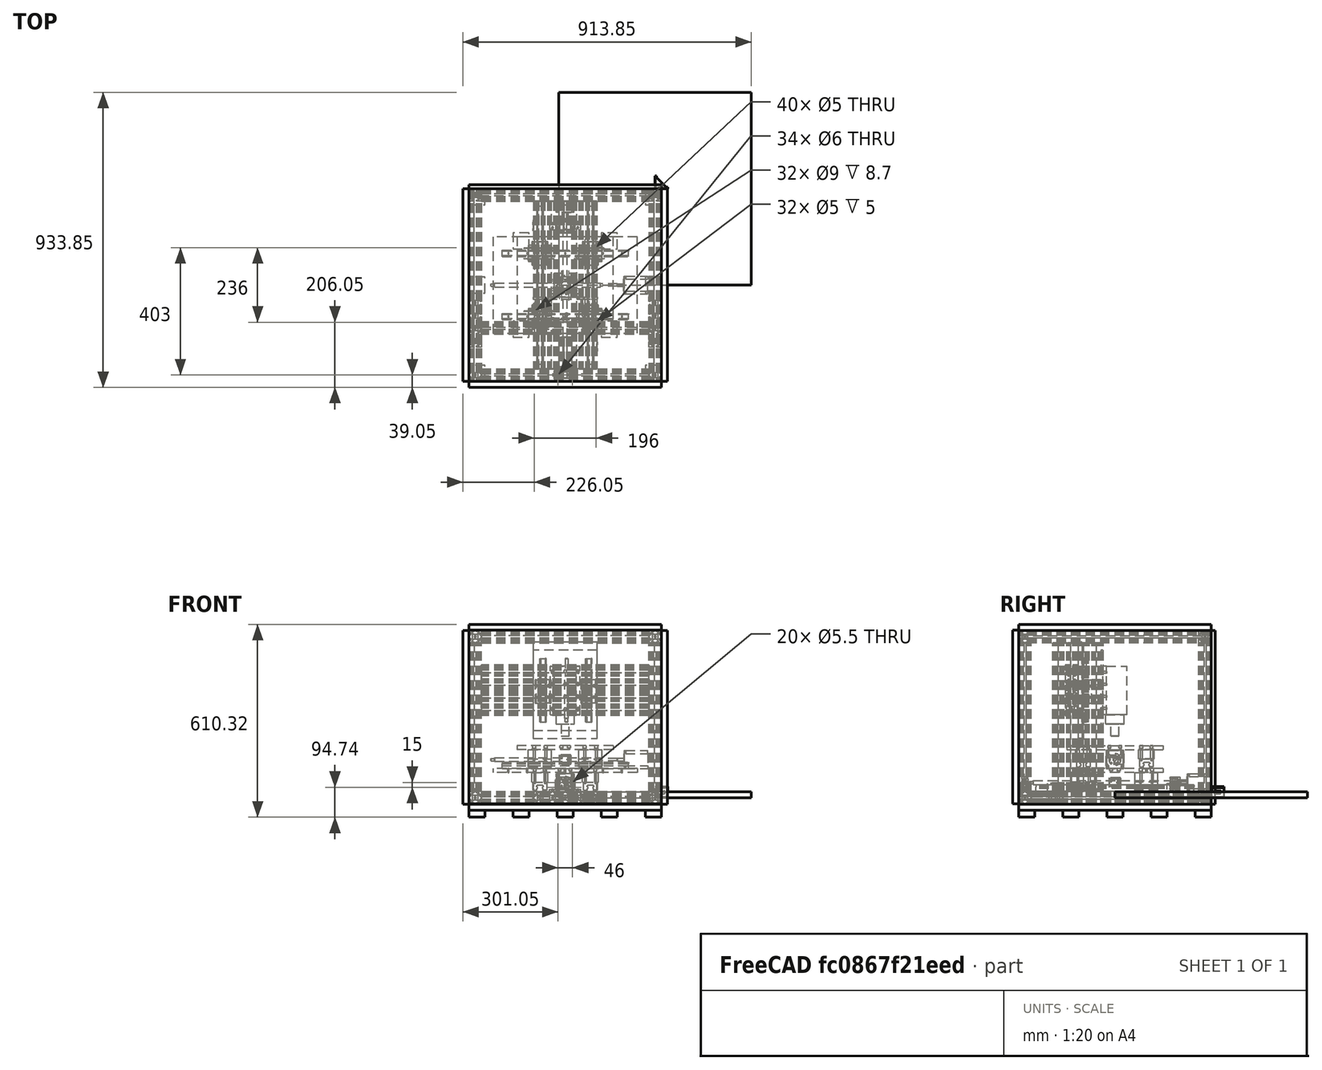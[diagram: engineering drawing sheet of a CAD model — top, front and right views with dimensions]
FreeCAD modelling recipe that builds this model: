
FCSTD DOCUMENT  (FreeCAD 1.0R39109 (Git))
Label: cnc
License: All rights reserved
LicenseURL: http://en.wikipedia.org/wiki/All_rights_reserved
objects: PartDesign::Body×118, PartDesign::FeatureBase×86, Sketcher::SketchObject×41, PartDesign::Pad×35, TechDraw::DrawViewDimension×35, PartDesign::Pocket×10, TechDraw::DrawViewBalloon×9, TechDraw::DrawProjGroupItem×8, App::DocumentObjectGroup×7, TechDraw::DrawViewAnnotation×5, Part::Extrusion×4, Part::Cut×4, TechDraw::DrawSVGTemplate×4, TechDraw::DrawPage×4, PartDesign::Revolution×3, Part::Box×1, Spreadsheet::Sheet×1, TechDraw::DrawProjGroup×1
note: 586 computed .brp shape members not serialized (recipe doc carries the construction recipe); baked Part::Feature solids carry a one-line shape summary decoded from their .brp

FEATURE [Sketcher::SketchObject] Sketch001
  ArcFitTolerance = 1e-06
  AttachmentSupport = -> [XY_Plane001]
  FullyConstrained = true
  MakeInternals = false
  MapMode = 5
  sketch-geometry (37):
    g0: LineSegment StartX=-20 StartY=4.065 StartZ=0 EndX=-20 EndY=20 EndZ=0
    g1: LineSegment StartX=-20 StartY=20 StartZ=0 EndX=-4.065 EndY=20 EndZ=0
    g2: LineSegment StartX=-4.065 StartY=20 StartZ=0 EndX=-4.065 EndY=15.68 EndZ=0
    g3: LineSegment StartX=-4.065 StartY=15.68 StartZ=0 EndX=-12.6253 EndY=15.68 EndZ=0
    g4: LineSegment StartX=-12.6253 StartY=15.68 StartZ=0 EndX=-5.22957 EndY=8.28427 EndZ=0
    g5: LineSegment StartX=-5.22957 StartY=8.28427 StartZ=0 EndX=5.22957 EndY=8.28427 EndZ=0
    g6: LineSegment StartX=5.22957 StartY=8.28427 StartZ=0 EndX=12.6253 EndY=15.68 EndZ=0
    g7: LineSegment StartX=12.6253 StartY=15.68 StartZ=0 EndX=4.065 EndY=15.68 EndZ=0
    g8: LineSegment StartX=4.065 StartY=15.68 StartZ=0 EndX=4.065 EndY=20 EndZ=0
    g9: LineSegment StartX=4.065 StartY=20 StartZ=0 EndX=20 EndY=20 EndZ=0
    g10: LineSegment StartX=20 StartY=20 StartZ=0 EndX=20 EndY=4.065 EndZ=0
    g11: LineSegment StartX=20 StartY=4.065 StartZ=0 EndX=15.68 EndY=4.065 EndZ=0
    g12: LineSegment StartX=15.68 StartY=4.065 StartZ=0 EndX=15.68 EndY=12.6253 EndZ=0
    g13: LineSegment StartX=15.68 StartY=12.6253 StartZ=0 EndX=8.28427 EndY=5.22957 EndZ=0
    g14: LineSegment StartX=8.28427 StartY=5.22957 StartZ=0 EndX=8.28427 EndY=-5.22957 EndZ=0
    g15: LineSegment StartX=8.28427 StartY=-5.22957 StartZ=0 EndX=15.68 EndY=-12.6253 EndZ=0
    g16: LineSegment StartX=15.68 StartY=-12.6253 StartZ=0 EndX=15.68 EndY=-4.065 EndZ=0
    g17: LineSegment StartX=15.68 StartY=-4.065 StartZ=0 EndX=20 EndY=-4.065 EndZ=0
    g18: LineSegment StartX=20 StartY=-4.065 StartZ=0 EndX=20 EndY=-20 EndZ=0
    g19: LineSegment StartX=20 StartY=-20 StartZ=0 EndX=4.065 EndY=-20 EndZ=0
    g20: LineSegment StartX=4.065 StartY=-20 StartZ=0 EndX=4.065 EndY=-15.68 EndZ=0
    g21: LineSegment StartX=4.065 StartY=-15.68 StartZ=0 EndX=12.6253 EndY=-15.68 EndZ=0
    g22: LineSegment StartX=12.6253 StartY=-15.68 StartZ=0 EndX=5.22957 EndY=-8.28427 EndZ=0
    g23: LineSegment StartX=5.22957 StartY=-8.28427 StartZ=0 EndX=-5.22957 EndY=-8.28427 EndZ=0
    g24: LineSegment StartX=-5.22957 StartY=-8.28427 StartZ=0 EndX=-12.6253 EndY=-15.68 EndZ=0
    g25: LineSegment StartX=-12.6253 StartY=-15.68 StartZ=0 EndX=-4.065 EndY=-15.68 EndZ=0
    g26: LineSegment StartX=-4.065 StartY=-15.68 StartZ=0 EndX=-4.065 EndY=-20 EndZ=0
    g27: LineSegment StartX=-4.065 StartY=-20 StartZ=0 EndX=-20 EndY=-20 EndZ=0
    g28: LineSegment StartX=-20 StartY=-20 StartZ=0 EndX=-20 EndY=-4.065 EndZ=0
    g29: LineSegment StartX=-20 StartY=-4.065 StartZ=0 EndX=-15.68 EndY=-4.065 EndZ=0
    g30: LineSegment StartX=-15.68 StartY=-4.065 StartZ=0 EndX=-15.68 EndY=-12.6253 EndZ=0
    g31: LineSegment StartX=-15.68 StartY=-12.6253 StartZ=0 EndX=-8.28427 EndY=-5.22957 EndZ=0
    g32: LineSegment StartX=-8.28427 StartY=-5.22957 StartZ=0 EndX=-8.28427 EndY=5.22957 EndZ=0
    g33: LineSegment StartX=-8.28427 StartY=5.22957 StartZ=0 EndX=-15.68 EndY=12.6253 EndZ=0
    g34: LineSegment StartX=-15.68 StartY=12.6253 StartZ=0 EndX=-15.68 EndY=4.065 EndZ=0
    g35: LineSegment StartX=-15.68 StartY=4.065 StartZ=0 EndX=-20 EndY=4.065 EndZ=0
    g36: Circle CenterX=0 CenterY=0 CenterZ=0 NormalX=0 NormalY=0 NormalZ=1 AngleXU=0 Radius=3.405
  constraints (100):
    c: Coincident(g24,g23)
    c: Coincident(g32,g31)
    c: Coincident(g30,g31)
    c: Coincident(g25,g24)
    c: Coincident(g25,g26)
    c: Coincident(g20,g21)
    c: Coincident(g19,g20)
    c: Coincident(g26,g27)
    c: Coincident(g28,g27)
    c: Coincident(g21,g22)
    c: Coincident(g19,g18)
    c: Coincident(g16,g15)
    c: Coincident(g14,g15)
    c: Coincident(g23,g22)
    c: Coincident(g16,g17)
    c: Coincident(g18,g17)
    c: Coincident(g12,g11)
    c: Coincident(g11,g10)
    c: Coincident(g10,g9)
    c: Coincident(g13,g12)
    c: Coincident(g13,g14)
    c: Coincident(g6,g5)
    c: Coincident(g7,g6)
    c: Coincident(g8,g7)
    c: Coincident(g9,g8)
    c: Coincident(g2,g1)
    c: Coincident(g2,g3)
    c: Coincident(g4,g3)
    c: Coincident(g34,g33)
    c: Coincident(g5,g4)
    c: Coincident(g33,g32)
    c: Coincident(g35,g34)
    c: Coincident(g35,g0)
    c: Coincident(g1,g0)
    c: Coincident(g30,g29)
    c: Coincident(g29,g28)
    c: Distance(g10,g0) = 40
    c: Distance(g27,g1) = 40
    c: Tangent(g1,g9)
    c: Tangent(g27,g19)
    c: Tangent(g0,g28)
    c: Tangent(g10,g18)
    c: Horizontal(g1)
    c: Vertical(g0)
    c: Equal(g2,g8)
    c: Equal(g8,g35)
    c: Equal(g35,g29)
    c: Equal(g29,g26)
    c: Equal(g26,g20)
    c: Equal(g20,g17)
    c: Equal(g17,g11)
    c: Vertical(g34)
    c: Vertical(g30)
    c: Vertical(g16)
    c: Vertical(g18)
    c: Vertical(g12)
    c: Vertical(g8)
    c: Vertical(g2)
    c: Vertical(g14)
    c: Vertical(g32)
    c: Horizontal(g35)
    c: Horizontal(g29)
    c: Horizontal(g23)
    c: Horizontal(g19)
    c: Horizontal(g25)
    c: Horizontal(g21)
    c: Horizontal(g7)
    c: Horizontal(g3)
    c: Parallel(g4,g33)
    c: Parallel(g33,g15)
    c: Parallel(g15,g22)
    c: Parallel(g6,g13)
    c: Parallel(g13,g24)
    c: Parallel(g24,g31)
    c: Equal(g23,g24)
    c: Equal(g24,g31)
    c: Equal(g4,g33)
    c: Equal(g6,g13)
    c: Equal(g15,g22)
    c: Angle(g25,g24) = 0.785398
    c: Distance(g8,g2) = 8.13
    c: Distance(g29,g35) = 8.13
    c: Tangent(g35,g11)
    c: Tangent(g17,g29)
    c: Tangent(g2,g26)
    c: Tangent(g8,g20)
    c: Distance(g22,g15) = 4.32
    c: Distance(g13,g6) = 4.32
    c: Distance(g33,g4) = 4.32
    c: Distance(g24,g31) = 4.32
    c: Equal(g32,g14)
    c: Equal(g5,g23)
    c: Equal(g25,g21)
    c: Equal(g34,g30)
    c: Distance(g35,g35) = 4.32
    c: Symmetric(g5,g22,g-1)
    c: Symmetric(g4,g5,g-2)
    c: Equal(g5,g32)
    c: Coincident(g36,g-1)
    c: Diameter(g36) = 6.81
FEATURE [Sketcher::SketchObject] Sketch002
  ArcFitTolerance = 1e-06
  AttachmentSupport = -> [XY_Plane003]
  FullyConstrained = true
  MakeInternals = false
  MapMode = 5
  sketch-geometry (37):
    g0: LineSegment StartX=-20 StartY=4.065 StartZ=0 EndX=-20 EndY=20 EndZ=0
    g1: LineSegment StartX=-20 StartY=20 StartZ=0 EndX=-4.065 EndY=20 EndZ=0
    g2: LineSegment StartX=-4.065 StartY=20 StartZ=0 EndX=-4.065 EndY=15.68 EndZ=0
    g3: LineSegment StartX=-4.065 StartY=15.68 StartZ=0 EndX=-12.6253 EndY=15.68 EndZ=0
    g4: LineSegment StartX=-12.6253 StartY=15.68 StartZ=0 EndX=-5.22957 EndY=8.28427 EndZ=0
    g5: LineSegment StartX=-5.22957 StartY=8.28427 StartZ=0 EndX=5.22957 EndY=8.28427 EndZ=0
    g6: LineSegment StartX=5.22957 StartY=8.28427 StartZ=0 EndX=12.6253 EndY=15.68 EndZ=0
    g7: LineSegment StartX=12.6253 StartY=15.68 StartZ=0 EndX=4.065 EndY=15.68 EndZ=0
    g8: LineSegment StartX=4.065 StartY=15.68 StartZ=0 EndX=4.065 EndY=20 EndZ=0
    g9: LineSegment StartX=4.065 StartY=20 StartZ=0 EndX=20 EndY=20 EndZ=0
    g10: LineSegment StartX=20 StartY=20 StartZ=0 EndX=20 EndY=4.065 EndZ=0
    g11: LineSegment StartX=20 StartY=4.065 StartZ=0 EndX=15.68 EndY=4.065 EndZ=0
    g12: LineSegment StartX=15.68 StartY=4.065 StartZ=0 EndX=15.68 EndY=12.6253 EndZ=0
    g13: LineSegment StartX=15.68 StartY=12.6253 StartZ=0 EndX=8.28427 EndY=5.22957 EndZ=0
    g14: LineSegment StartX=8.28427 StartY=5.22957 StartZ=0 EndX=8.28427 EndY=-5.22957 EndZ=0
    g15: LineSegment StartX=8.28427 StartY=-5.22957 StartZ=0 EndX=15.68 EndY=-12.6253 EndZ=0
    g16: LineSegment StartX=15.68 StartY=-12.6253 StartZ=0 EndX=15.68 EndY=-4.065 EndZ=0
    g17: LineSegment StartX=15.68 StartY=-4.065 StartZ=0 EndX=20 EndY=-4.065 EndZ=0
    g18: LineSegment StartX=20 StartY=-4.065 StartZ=0 EndX=20 EndY=-20 EndZ=0
    g19: LineSegment StartX=20 StartY=-20 StartZ=0 EndX=4.065 EndY=-20 EndZ=0
    g20: LineSegment StartX=4.065 StartY=-20 StartZ=0 EndX=4.065 EndY=-15.68 EndZ=0
    g21: LineSegment StartX=4.065 StartY=-15.68 StartZ=0 EndX=12.6253 EndY=-15.68 EndZ=0
    g22: LineSegment StartX=12.6253 StartY=-15.68 StartZ=0 EndX=5.22957 EndY=-8.28427 EndZ=0
    g23: LineSegment StartX=5.22957 StartY=-8.28427 StartZ=0 EndX=-5.22957 EndY=-8.28427 EndZ=0
    g24: LineSegment StartX=-5.22957 StartY=-8.28427 StartZ=0 EndX=-12.6253 EndY=-15.68 EndZ=0
    g25: LineSegment StartX=-12.6253 StartY=-15.68 StartZ=0 EndX=-4.065 EndY=-15.68 EndZ=0
    g26: LineSegment StartX=-4.065 StartY=-15.68 StartZ=0 EndX=-4.065 EndY=-20 EndZ=0
    g27: LineSegment StartX=-4.065 StartY=-20 StartZ=0 EndX=-20 EndY=-20 EndZ=0
    g28: LineSegment StartX=-20 StartY=-20 StartZ=0 EndX=-20 EndY=-4.065 EndZ=0
    g29: LineSegment StartX=-20 StartY=-4.065 StartZ=0 EndX=-15.68 EndY=-4.065 EndZ=0
    g30: LineSegment StartX=-15.68 StartY=-4.065 StartZ=0 EndX=-15.68 EndY=-12.6253 EndZ=0
    g31: LineSegment StartX=-15.68 StartY=-12.6253 StartZ=0 EndX=-8.28427 EndY=-5.22957 EndZ=0
    g32: LineSegment StartX=-8.28427 StartY=-5.22957 StartZ=0 EndX=-8.28427 EndY=5.22957 EndZ=0
    g33: LineSegment StartX=-8.28427 StartY=5.22957 StartZ=0 EndX=-15.68 EndY=12.6253 EndZ=0
    g34: LineSegment StartX=-15.68 StartY=12.6253 StartZ=0 EndX=-15.68 EndY=4.065 EndZ=0
    g35: LineSegment StartX=-15.68 StartY=4.065 StartZ=0 EndX=-20 EndY=4.065 EndZ=0
    g36: Circle CenterX=0 CenterY=0 CenterZ=0 NormalX=0 NormalY=0 NormalZ=1 AngleXU=0 Radius=3.405
  constraints (100):
    c: Coincident(g24,g23)
    c: Coincident(g32,g31)
    c: Coincident(g30,g31)
    c: Coincident(g25,g24)
    c: Coincident(g25,g26)
    c: Coincident(g20,g21)
    c: Coincident(g19,g20)
    c: Coincident(g26,g27)
    c: Coincident(g28,g27)
    c: Coincident(g21,g22)
    c: Coincident(g19,g18)
    c: Coincident(g16,g15)
    c: Coincident(g14,g15)
    c: Coincident(g23,g22)
    c: Coincident(g16,g17)
    c: Coincident(g18,g17)
    c: Coincident(g12,g11)
    c: Coincident(g11,g10)
    c: Coincident(g10,g9)
    c: Coincident(g13,g12)
    c: Coincident(g13,g14)
    c: Coincident(g6,g5)
    c: Coincident(g7,g6)
    c: Coincident(g8,g7)
    c: Coincident(g9,g8)
    c: Coincident(g2,g1)
    c: Coincident(g2,g3)
    c: Coincident(g4,g3)
    c: Coincident(g34,g33)
    c: Coincident(g5,g4)
    c: Coincident(g33,g32)
    c: Coincident(g35,g34)
    c: Coincident(g35,g0)
    c: Coincident(g1,g0)
    c: Coincident(g30,g29)
    c: Coincident(g29,g28)
    c: Distance(g10,g0) = 40
    c: Distance(g27,g1) = 40
    c: Tangent(g1,g9)
    c: Tangent(g27,g19)
    c: Tangent(g0,g28)
    c: Tangent(g10,g18)
    c: Horizontal(g1)
    c: Vertical(g0)
    c: Equal(g2,g8)
    c: Equal(g8,g35)
    c: Equal(g35,g29)
    c: Equal(g29,g26)
    c: Equal(g26,g20)
    c: Equal(g20,g17)
    c: Equal(g17,g11)
    c: Vertical(g34)
    c: Vertical(g30)
    c: Vertical(g16)
    c: Vertical(g18)
    c: Vertical(g12)
    c: Vertical(g8)
    c: Vertical(g2)
    c: Vertical(g14)
    c: Vertical(g32)
    c: Horizontal(g35)
    c: Horizontal(g29)
    c: Horizontal(g23)
    c: Horizontal(g19)
    c: Horizontal(g25)
    c: Horizontal(g21)
    c: Horizontal(g7)
    c: Horizontal(g3)
    c: Parallel(g4,g33)
    c: Parallel(g33,g15)
    c: Parallel(g15,g22)
    c: Parallel(g6,g13)
    c: Parallel(g13,g24)
    c: Parallel(g24,g31)
    c: Equal(g23,g24)
    c: Equal(g24,g31)
    c: Equal(g4,g33)
    c: Equal(g6,g13)
    c: Equal(g15,g22)
    c: Angle(g25,g24) = 0.785398
    c: Distance(g8,g2) = 8.13
    c: Distance(g29,g35) = 8.13
    c: Tangent(g35,g11)
    c: Tangent(g17,g29)
    c: Tangent(g2,g26)
    c: Tangent(g8,g20)
    c: Distance(g22,g15) = 4.32
    c: Distance(g13,g6) = 4.32
    c: Distance(g33,g4) = 4.32
    c: Distance(g24,g31) = 4.32
    c: Equal(g32,g14)
    c: Equal(g5,g23)
    c: Equal(g25,g21)
    c: Equal(g34,g30)
    c: Distance(g35,g35) = 4.32
    c: Symmetric(g5,g22,g-1)
    c: Symmetric(g4,g5,g-2)
    c: Equal(g5,g32)
    c: Coincident(g36,g-1)
    c: Diameter(g36) = 6.81
FEATURE [PartDesign::Pad] Pad
  Direction = (0,0,1)
  Length = 610
  Length2 = 10
  Profile = -> Sketch001
  ReferenceAxis = -> Sketch001 [N_Axis]
  Refine = true
  Suppressed = false
  Type = 0
FEATURE [PartDesign::Body] Body001  label="4040 extrusion @ 610"
  AllowCompound = false
  Group = -> [Sketch001,Pad]
  Origin = -> Origin001
  Tip = -> Pad
FEATURE [PartDesign::Pad] Pad001
  Direction = (0,0,1)
  Length = 530
  Length2 = 10
  Profile = -> Sketch002
  ReferenceAxis = -> Sketch002 [N_Axis]
  Refine = true
  Suppressed = false
  Type = 0
FEATURE [PartDesign::Body] Body002  label="4040 extrusion @ 530"
  AllowCompound = false
  Group = -> [Sketch002,Pad001]
  Origin = -> Origin003
  Tip = -> Pad001
FEATURE [Sketcher::SketchObject] Sketch003
  ArcFitTolerance = 1e-06
  AttachmentSupport = -> [XY_Plane005]
  FullyConstrained = true
  MakeInternals = false
  MapMode = 5
  sketch-geometry (37):
    g0: LineSegment StartX=-20 StartY=4.065 StartZ=0 EndX=-20 EndY=20 EndZ=0
    g1: LineSegment StartX=-20 StartY=20 StartZ=0 EndX=-4.065 EndY=20 EndZ=0
    g2: LineSegment StartX=-4.065 StartY=20 StartZ=0 EndX=-4.065 EndY=15.68 EndZ=0
    g3: LineSegment StartX=-4.065 StartY=15.68 StartZ=0 EndX=-12.6253 EndY=15.68 EndZ=0
    g4: LineSegment StartX=-12.6253 StartY=15.68 StartZ=0 EndX=-5.22957 EndY=8.28427 EndZ=0
    g5: LineSegment StartX=-5.22957 StartY=8.28427 StartZ=0 EndX=5.22957 EndY=8.28427 EndZ=0
    g6: LineSegment StartX=5.22957 StartY=8.28427 StartZ=0 EndX=12.6253 EndY=15.68 EndZ=0
    g7: LineSegment StartX=12.6253 StartY=15.68 StartZ=0 EndX=4.065 EndY=15.68 EndZ=0
    g8: LineSegment StartX=4.065 StartY=15.68 StartZ=0 EndX=4.065 EndY=20 EndZ=0
    g9: LineSegment StartX=4.065 StartY=20 StartZ=0 EndX=20 EndY=20 EndZ=0
    g10: LineSegment StartX=20 StartY=20 StartZ=0 EndX=20 EndY=4.065 EndZ=0
    g11: LineSegment StartX=20 StartY=4.065 StartZ=0 EndX=15.68 EndY=4.065 EndZ=0
    g12: LineSegment StartX=15.68 StartY=4.065 StartZ=0 EndX=15.68 EndY=12.6253 EndZ=0
    g13: LineSegment StartX=15.68 StartY=12.6253 StartZ=0 EndX=8.28427 EndY=5.22957 EndZ=0
    g14: LineSegment StartX=8.28427 StartY=5.22957 StartZ=0 EndX=8.28427 EndY=-5.22957 EndZ=0
    g15: LineSegment StartX=8.28427 StartY=-5.22957 StartZ=0 EndX=15.68 EndY=-12.6253 EndZ=0
    g16: LineSegment StartX=15.68 StartY=-12.6253 StartZ=0 EndX=15.68 EndY=-4.065 EndZ=0
    g17: LineSegment StartX=15.68 StartY=-4.065 StartZ=0 EndX=20 EndY=-4.065 EndZ=0
    g18: LineSegment StartX=20 StartY=-4.065 StartZ=0 EndX=20 EndY=-20 EndZ=0
    g19: LineSegment StartX=20 StartY=-20 StartZ=0 EndX=4.065 EndY=-20 EndZ=0
    g20: LineSegment StartX=4.065 StartY=-20 StartZ=0 EndX=4.065 EndY=-15.68 EndZ=0
    g21: LineSegment StartX=4.065 StartY=-15.68 StartZ=0 EndX=12.6253 EndY=-15.68 EndZ=0
    g22: LineSegment StartX=12.6253 StartY=-15.68 StartZ=0 EndX=5.22957 EndY=-8.28427 EndZ=0
    g23: LineSegment StartX=5.22957 StartY=-8.28427 StartZ=0 EndX=-5.22957 EndY=-8.28427 EndZ=0
    g24: LineSegment StartX=-5.22957 StartY=-8.28427 StartZ=0 EndX=-12.6253 EndY=-15.68 EndZ=0
    g25: LineSegment StartX=-12.6253 StartY=-15.68 StartZ=0 EndX=-4.065 EndY=-15.68 EndZ=0
    g26: LineSegment StartX=-4.065 StartY=-15.68 StartZ=0 EndX=-4.065 EndY=-20 EndZ=0
    g27: LineSegment StartX=-4.065 StartY=-20 StartZ=0 EndX=-20 EndY=-20 EndZ=0
    g28: LineSegment StartX=-20 StartY=-20 StartZ=0 EndX=-20 EndY=-4.065 EndZ=0
    g29: LineSegment StartX=-20 StartY=-4.065 StartZ=0 EndX=-15.68 EndY=-4.065 EndZ=0
    g30: LineSegment StartX=-15.68 StartY=-4.065 StartZ=0 EndX=-15.68 EndY=-12.6253 EndZ=0
    g31: LineSegment StartX=-15.68 StartY=-12.6253 StartZ=0 EndX=-8.28427 EndY=-5.22957 EndZ=0
    g32: LineSegment StartX=-8.28427 StartY=-5.22957 StartZ=0 EndX=-8.28427 EndY=5.22957 EndZ=0
    g33: LineSegment StartX=-8.28427 StartY=5.22957 StartZ=0 EndX=-15.68 EndY=12.6253 EndZ=0
    g34: LineSegment StartX=-15.68 StartY=12.6253 StartZ=0 EndX=-15.68 EndY=4.065 EndZ=0
    g35: LineSegment StartX=-15.68 StartY=4.065 StartZ=0 EndX=-20 EndY=4.065 EndZ=0
    g36: Circle CenterX=0 CenterY=0 CenterZ=0 NormalX=0 NormalY=0 NormalZ=1 AngleXU=0 Radius=3.405
  constraints (100):
    c: Coincident(g24,g23)
    c: Coincident(g32,g31)
    c: Coincident(g30,g31)
    c: Coincident(g25,g24)
    c: Coincident(g25,g26)
    c: Coincident(g20,g21)
    c: Coincident(g19,g20)
    c: Coincident(g26,g27)
    c: Coincident(g28,g27)
    c: Coincident(g21,g22)
    c: Coincident(g19,g18)
    c: Coincident(g16,g15)
    c: Coincident(g14,g15)
    c: Coincident(g23,g22)
    c: Coincident(g16,g17)
    c: Coincident(g18,g17)
    c: Coincident(g12,g11)
    c: Coincident(g11,g10)
    c: Coincident(g10,g9)
    c: Coincident(g13,g12)
    c: Coincident(g13,g14)
    c: Coincident(g6,g5)
    c: Coincident(g7,g6)
    c: Coincident(g8,g7)
    c: Coincident(g9,g8)
    c: Coincident(g2,g1)
    c: Coincident(g2,g3)
    c: Coincident(g4,g3)
    c: Coincident(g34,g33)
    c: Coincident(g5,g4)
    c: Coincident(g33,g32)
    c: Coincident(g35,g34)
    c: Coincident(g35,g0)
    c: Coincident(g1,g0)
    c: Coincident(g30,g29)
    c: Coincident(g29,g28)
    c: Distance(g10,g0) = 40
    c: Distance(g27,g1) = 40
    c: Tangent(g1,g9)
    c: Tangent(g27,g19)
    c: Tangent(g0,g28)
    c: Tangent(g10,g18)
    c: Horizontal(g1)
    c: Vertical(g0)
    c: Equal(g2,g8)
    c: Equal(g8,g35)
    c: Equal(g35,g29)
    c: Equal(g29,g26)
    c: Equal(g26,g20)
    c: Equal(g20,g17)
    c: Equal(g17,g11)
    c: Vertical(g34)
    c: Vertical(g30)
    c: Vertical(g16)
    c: Vertical(g18)
    c: Vertical(g12)
    c: Vertical(g8)
    c: Vertical(g2)
    c: Vertical(g14)
    c: Vertical(g32)
    c: Horizontal(g35)
    c: Horizontal(g29)
    c: Horizontal(g23)
    c: Horizontal(g19)
    c: Horizontal(g25)
    c: Horizontal(g21)
    c: Horizontal(g7)
    c: Horizontal(g3)
    c: Parallel(g4,g33)
    c: Parallel(g33,g15)
    c: Parallel(g15,g22)
    c: Parallel(g6,g13)
    c: Parallel(g13,g24)
    c: Parallel(g24,g31)
    c: Equal(g23,g24)
    c: Equal(g24,g31)
    c: Equal(g4,g33)
    c: Equal(g6,g13)
    c: Equal(g15,g22)
    c: Angle(g25,g24) = 0.785398
    c: Distance(g8,g2) = 8.13
    c: Distance(g29,g35) = 8.13
    c: Tangent(g35,g11)
    c: Tangent(g17,g29)
    c: Tangent(g2,g26)
    c: Tangent(g8,g20)
    c: Distance(g22,g15) = 4.32
    c: Distance(g13,g6) = 4.32
    c: Distance(g33,g4) = 4.32
    c: Distance(g24,g31) = 4.32
    c: Equal(g32,g14)
    c: Equal(g5,g23)
    c: Equal(g25,g21)
    c: Equal(g34,g30)
    c: Distance(g35,g35) = 4.32
    c: Symmetric(g5,g22,g-1)
    c: Symmetric(g4,g5,g-2)
    c: Equal(g5,g32)
    c: Coincident(g36,g-1)
    c: Diameter(g36) = 6.81
FEATURE [PartDesign::Pad] Pad002
  Direction = (0,0,1)
  Length = 470
  Length2 = 10
  Profile = -> Sketch003
  ReferenceAxis = -> Sketch003 [N_Axis]
  Refine = true
  Suppressed = false
  Type = 0
FEATURE [PartDesign::Body] Body003  label="4040 extrusion @ 470"
  AllowCompound = false
  Group = -> [Sketch003,Pad002]
  Origin = -> Origin005
  Tip = -> Pad002
FEATURE [Sketcher::SketchObject] Sketch004
  ArcFitTolerance = 1e-06
  AttachmentSupport = -> [XY_Plane006]
  FullyConstrained = true
  MakeInternals = false
  MapMode = 5
  sketch-geometry (70):
    g0: LineSegment StartX=-20 StartY=4.065 StartZ=0 EndX=-20 EndY=20 EndZ=0
    g1: LineSegment StartX=-20 StartY=20 StartZ=0 EndX=-4.065 EndY=20 EndZ=0
    g2: LineSegment StartX=-4.065 StartY=20 StartZ=0 EndX=-4.065 EndY=15.68 EndZ=0
    g3: LineSegment StartX=-4.065 StartY=15.68 StartZ=0 EndX=-12.6253 EndY=15.68 EndZ=0
    g4: LineSegment StartX=-12.6253 StartY=15.68 StartZ=0 EndX=-5.22957 EndY=8.28427 EndZ=0
    g5: LineSegment StartX=-5.22957 StartY=8.28427 StartZ=0 EndX=5.22957 EndY=8.28427 EndZ=0
    g6: LineSegment StartX=5.22957 StartY=8.28427 StartZ=0 EndX=12.6253 EndY=15.68 EndZ=0
    g7: LineSegment StartX=12.6253 StartY=15.68 StartZ=0 EndX=4.065 EndY=15.68 EndZ=0
    g8: LineSegment StartX=4.065 StartY=15.68 StartZ=0 EndX=4.065 EndY=20 EndZ=0
    g9: LineSegment StartX=4.065 StartY=20 StartZ=0 EndX=20 EndY=20 EndZ=0
    g10: LineSegment StartX=20 StartY=4.065 StartZ=0 EndX=15.68 EndY=4.065 EndZ=0
    g11: LineSegment StartX=15.68 StartY=4.065 StartZ=0 EndX=15.68 EndY=12.6253 EndZ=0
    g12: LineSegment StartX=15.68 StartY=12.6253 StartZ=0 EndX=8.28427 EndY=5.22957 EndZ=0
    g13: LineSegment StartX=8.28427 StartY=5.22957 StartZ=0 EndX=8.28427 EndY=-5.22957 EndZ=0
    g14: LineSegment StartX=8.28427 StartY=-5.22957 StartZ=0 EndX=15.68 EndY=-12.6253 EndZ=0
    g15: LineSegment StartX=15.68 StartY=-12.6253 StartZ=0 EndX=15.68 EndY=-4.065 EndZ=0
    g16: LineSegment StartX=15.68 StartY=-4.065 StartZ=0 EndX=20 EndY=-4.065 EndZ=0
    g17: LineSegment StartX=20 StartY=-20 StartZ=0 EndX=4.065 EndY=-20 EndZ=0
    g18: LineSegment StartX=4.065 StartY=-20 StartZ=0 EndX=4.065 EndY=-15.68 EndZ=0
    g19: LineSegment StartX=4.065 StartY=-15.68 StartZ=0 EndX=12.6253 EndY=-15.68 EndZ=0
    g20: LineSegment StartX=12.6253 StartY=-15.68 StartZ=0 EndX=5.22957 EndY=-8.28427 EndZ=0
    g21: LineSegment StartX=5.22957 StartY=-8.28427 StartZ=0 EndX=-5.22957 EndY=-8.28427 EndZ=0
    g22: LineSegment StartX=-5.22957 StartY=-8.28427 StartZ=0 EndX=-12.6253 EndY=-15.68 EndZ=0
    g23: LineSegment StartX=-12.6253 StartY=-15.68 StartZ=0 EndX=-4.065 EndY=-15.68 EndZ=0
    g24: LineSegment StartX=-4.065 StartY=-15.68 StartZ=0 EndX=-4.065 EndY=-20 EndZ=0
    g25: LineSegment StartX=-4.065 StartY=-20 StartZ=0 EndX=-20 EndY=-20 EndZ=0
    g26: LineSegment StartX=-20 StartY=-20 StartZ=0 EndX=-20 EndY=-4.065 EndZ=0
    g27: LineSegment StartX=-20 StartY=-4.065 StartZ=0 EndX=-15.68 EndY=-4.065 EndZ=0
    g28: LineSegment StartX=-15.68 StartY=-4.065 StartZ=0 EndX=-15.68 EndY=-12.6253 EndZ=0
    g29: LineSegment StartX=-15.68 StartY=-12.6253 StartZ=0 EndX=-8.28427 EndY=-5.22957 EndZ=0
    g30: LineSegment StartX=-8.28427 StartY=-5.22957 StartZ=0 EndX=-8.28427 EndY=5.22957 EndZ=0
    g31: LineSegment StartX=-8.28427 StartY=5.22957 StartZ=0 EndX=-15.68 EndY=12.6253 EndZ=0
    g32: LineSegment StartX=-15.68 StartY=12.6253 StartZ=0 EndX=-15.68 EndY=4.065 EndZ=0
    g33: LineSegment StartX=-15.68 StartY=4.065 StartZ=0 EndX=-20 EndY=4.065 EndZ=0
    g34: Circle CenterX=0 CenterY=0 CenterZ=0 NormalX=0 NormalY=0 NormalZ=1 AngleXU=0 Radius=3.405
    g35: LineSegment StartX=20 StartY=20 StartZ=0 EndX=35.935 EndY=20 EndZ=0
    g36: LineSegment StartX=35.935 StartY=20 StartZ=0 EndX=35.935 EndY=15.68 EndZ=0
    g37: LineSegment StartX=35.935 StartY=15.68 StartZ=0 EndX=27.3747 EndY=15.68 EndZ=0
    g38: LineSegment StartX=27.3747 StartY=15.68 StartZ=0 EndX=34.7704 EndY=8.28427 EndZ=0
    g39: LineSegment StartX=34.7704 StartY=8.28427 StartZ=0 EndX=45.2296 EndY=8.28427 EndZ=0
    g40: LineSegment StartX=45.2296 StartY=8.28427 StartZ=0 EndX=52.6253 EndY=15.68 EndZ=0
    g41: LineSegment StartX=52.6253 StartY=15.68 StartZ=0 EndX=44.065 EndY=15.68 EndZ=0
    g42: LineSegment StartX=44.065 StartY=15.68 StartZ=0 EndX=44.065 EndY=20 EndZ=0
    g43: LineSegment StartX=44.065 StartY=20 StartZ=0 EndX=60 EndY=20 EndZ=0
    g44: LineSegment StartX=60 StartY=20 StartZ=0 EndX=60 EndY=4.065 EndZ=0
    g45: LineSegment StartX=60 StartY=4.065 StartZ=0 EndX=55.68 EndY=4.065 EndZ=0
    g46: LineSegment StartX=55.68 StartY=4.065 StartZ=0 EndX=55.68 EndY=12.6253 EndZ=0
    g47: LineSegment StartX=55.68 StartY=12.6253 StartZ=0 EndX=48.2843 EndY=5.22957 EndZ=0
    g48: LineSegment StartX=48.2843 StartY=5.22957 StartZ=0 EndX=48.2843 EndY=-5.22957 EndZ=0
    g49: LineSegment StartX=48.2843 StartY=-5.22957 StartZ=0 EndX=55.68 EndY=-12.6253 EndZ=0
    g50: LineSegment StartX=55.68 StartY=-12.6253 StartZ=0 EndX=55.68 EndY=-4.065 EndZ=0
    g51: LineSegment StartX=55.68 StartY=-4.065 StartZ=0 EndX=60 EndY=-4.065 EndZ=0
    g52: LineSegment StartX=60 StartY=-4.065 StartZ=0 EndX=60 EndY=-20 EndZ=0
    g53: LineSegment StartX=60 StartY=-20 StartZ=0 EndX=44.065 EndY=-20 EndZ=0
    g54: LineSegment StartX=44.065 StartY=-20 StartZ=0 EndX=44.065 EndY=-15.68 EndZ=0
    g55: LineSegment StartX=44.065 StartY=-15.68 StartZ=0 EndX=52.6253 EndY=-15.68 EndZ=0
    g56: LineSegment StartX=52.6253 StartY=-15.68 StartZ=0 EndX=45.2296 EndY=-8.28427 EndZ=0
    g57: LineSegment StartX=45.2296 StartY=-8.28427 StartZ=0 EndX=34.7704 EndY=-8.28427 EndZ=0
    g58: LineSegment StartX=34.7704 StartY=-8.28427 StartZ=0 EndX=27.3747 EndY=-15.68 EndZ=0
    g59: LineSegment StartX=27.3747 StartY=-15.68 StartZ=0 EndX=35.935 EndY=-15.68 EndZ=0
    g60: LineSegment StartX=35.935 StartY=-15.68 StartZ=0 EndX=35.935 EndY=-20 EndZ=0
    g61: LineSegment StartX=35.935 StartY=-20 StartZ=0 EndX=20 EndY=-20 EndZ=0
    g62: LineSegment StartX=24.32 StartY=12.6253 StartZ=0 EndX=24.32 EndY=4.065 EndZ=0
    g63: LineSegment StartX=24.32 StartY=4.065 StartZ=0 EndX=20 EndY=4.065 EndZ=0
    g64: LineSegment StartX=20 StartY=-4.065 StartZ=0 EndX=24.32 EndY=-4.065 EndZ=0
    g65: LineSegment StartX=24.32 StartY=-4.065 StartZ=0 EndX=24.32 EndY=-12.6253 EndZ=0
    g66: LineSegment StartX=24.32 StartY=-12.6253 StartZ=0 EndX=31.7157 EndY=-5.22957 EndZ=0
    g67: LineSegment StartX=31.7157 StartY=-5.22957 StartZ=0 EndX=31.7157 EndY=5.22957 EndZ=0
    g68: LineSegment StartX=31.7157 StartY=5.22957 StartZ=0 EndX=24.32 EndY=12.6253 EndZ=0
    g69: Circle CenterX=40 CenterY=0 CenterZ=0 NormalX=0 NormalY=0 NormalZ=1 AngleXU=0 Radius=3.405
  constraints (200):
    c: Coincident(g22,g21)
    c: Coincident(g30,g29)
    c: Coincident(g28,g29)
    c: Coincident(g23,g22)
    c: Coincident(g23,g24)
    c: Coincident(g18,g19)
    c: Coincident(g17,g18)
    c: Coincident(g24,g25)
    c: Coincident(g26,g25)
    c: Coincident(g19,g20)
    c: Coincident(g15,g14)
    c: Coincident(g13,g14)
    c: Coincident(g21,g20)
    c: Coincident(g15,g16)
    c: Coincident(g11,g10)
    c: Coincident(g12,g11)
    c: Coincident(g12,g13)
    c: Coincident(g6,g5)
    c: Coincident(g7,g6)
    c: Coincident(g8,g7)
    c: Coincident(g9,g8)
    c: Coincident(g2,g1)
    c: Coincident(g2,g3)
    c: Coincident(g4,g3)
    c: Coincident(g32,g31)
    c: Coincident(g5,g4)
    c: Coincident(g31,g30)
    c: Coincident(g33,g32)
    c: Coincident(g33,g0)
    c: Coincident(g1,g0)
    c: Coincident(g28,g27)
    c: Coincident(g27,g26)
    c: Distance(g9,g0) = 40
    c: Distance(g25,g1) = 40
    c: Tangent(g1,g9)
    c: Tangent(g25,g17)
    c: Tangent(g0,g26)
    c: Horizontal(g1)
    c: Vertical(g0)
    c: Equal(g2,g8)
    c: Equal(g8,g33)
    c: Equal(g33,g27)
    c: Equal(g27,g24)
    c: Equal(g24,g18)
    c: Equal(g18,g16)
    c: Equal(g16,g10)
    c: Vertical(g32)
    c: Vertical(g28)
    c: Vertical(g15)
    c: Vertical(g11)
    c: Vertical(g8)
    c: Vertical(g2)
    c: Vertical(g13)
    c: Vertical(g30)
    c: Horizontal(g33)
    c: Horizontal(g27)
    c: Horizontal(g21)
    c: Horizontal(g17)
    c: Horizontal(g23)
    c: Horizontal(g19)
    c: Horizontal(g7)
    c: Horizontal(g3)
    c: Parallel(g4,g31)
    c: Parallel(g31,g14)
    c: Parallel(g14,g20)
    c: Parallel(g6,g12)
    c: Parallel(g12,g22)
    c: Parallel(g22,g29)
    c: Equal(g21,g22)
    c: Equal(g22,g29)
    c: Equal(g4,g31)
    c: Equal(g6,g12)
    c: Equal(g14,g20)
    c: Angle(g23,g22) = 0.785398
    c: Distance(g8,g2) = 8.13
    c: Distance(g27,g33) = 8.13
    c: Tangent(g33,g10)
    c: Tangent(g16,g27)
    c: Tangent(g2,g24)
    c: Tangent(g8,g18)
    c: Distance(g20,g14) = 4.32
    c: Distance(g12,g6) = 4.32
    c: Distance(g31,g4) = 4.32
    c: Distance(g22,g29) = 4.32
    c: Equal(g30,g13)
    c: Equal(g5,g21)
    c: Equal(g23,g19)
    c: Equal(g32,g28)
    c: Distance(g33,g33) = 4.32
    c: Symmetric(g5,g20,g-1)
    c: Symmetric(g4,g5,g-2)
    c: Equal(g5,g30)
    c: Coincident(g34,g-1)
    c: Diameter(g34) = 6.81
    c: Coincident(g35,g9)
    c: Coincident(g36,g35)
    c: Coincident(g37,g36)
    c: Horizontal(g37)
    c: Coincident(g38,g37)
    c: Coincident(g39,g38)
    c: Horizontal(g39)
    c: Coincident(g41,g40)
    c: Vertical(g44)
    c: Coincident(g45,g44)
    c: Coincident(g48,g47)
    c: Vertical(g48)
    c: Coincident(g49,g48)
    c: Vertical(g50)
    c: Horizontal(g51)
    c: Coincident(g52,g51)
    c: Vertical(g52)
    c: Coincident(g53,g52)
    c: Coincident(g55,g54)
    c: Coincident(g57,g56)
    c: Horizontal(g57)
    c: Coincident(g58,g57)
    c: Coincident(g59,g58)
    c: Horizontal(g59)
    c: Coincident(g61,g60)
    c: Coincident(g61,g17)
    c: Coincident(g63,g10)
    c: Coincident(g64,g16)
    c: Coincident(g65,g64)
    c: Coincident(g66,g65)
    c: Coincident(g67,g66)
    c: Coincident(g68,g67)
    c: Coincident(g68,g62)
    c: PointOnObject(g69,g-1)
    c: Coincident(g43,g42)
    c: Coincident(g43,g44)
    c: Coincident(g41,g42)
    c: Coincident(g39,g40)
    c: Coincident(g46,g47)
    c: Coincident(g46,g45)
    c: Coincident(g50,g51)
    c: Coincident(g49,g50)
    c: Coincident(g54,g53)
    c: Coincident(g56,g55)
    c: Coincident(g59,g60)
    c: Coincident(g62,g63)
    c: Equal(g34,g69)
    c: Equal(g39,g67)
    c: Equal(g67,g57)
    c: Equal(g57,g48)
    c: Equal(g48,g13)
    c: Equal(g38,g68)
    c: Equal(g68,g66)
    c: Equal(g66,g58)
    c: Equal(g58,g56)
    c: Equal(g56,g49)
    c: Equal(g49,g47)
    c: Equal(g47,g40)
    c: Equal(g40,g12)
    c: Equal(g10,g63)
    c: Equal(g16,g64)
    c: Equal(g64,g45)
    c: Equal(g45,g51)
    c: Equal(g51,g42)
    c: Equal(g42,g36)
    c: Equal(g36,g60)
    c: Equal(g60,g54)
    c: Parallel(g47,g40)
    c: Parallel(g38,g68)
    c: Parallel(g66,g58)
    c: Parallel(g49,g56)
    c: Parallel(g56,g68)
    c: Parallel(g40,g66)
    c: Horizontal(g35)
    c: Horizontal(g43)
    c: Horizontal(g45)
    c: Horizontal(g53)
    c: Horizontal(g61)
    c: Horizontal(g64)
    c: Horizontal(g63)
    c: Horizontal(g41)
    c: Vertical(g42)
    c: Vertical(g36)
    c: Vertical(g62)
    c: Vertical(g65)
    c: Vertical(g60)
    c: Vertical(g54)
    c: Vertical(g46)
    c: Horizontal(g55)
    c: Vertical(g67)
    c: Equal(g7,g37)
    c: Equal(g37,g41)
    c: Equal(g41,g46)
    c: Equal(g46,g55)
    c: Equal(g55,g59)
    c: Equal(g59,g65)
    c: Equal(g65,g62)
    c: Equal(g55,g50)
    c: Parallel(g40,g6)
    c: Distance(g9,g44) = 40
    c: DistanceX(g34,g69) = 40
    c: Equal(g35,g43)
    c: Equal(g43,g9)
    c: Equal(g44,g52)
    c: Equal(g53,g61)
    c: Equal(g61,g17)
FEATURE [PartDesign::Pad] Pad003
  Direction = (0,0,1)
  Length = 530
  Length2 = 10
  Profile = -> Sketch004
  ReferenceAxis = -> Sketch004 [N_Axis]
  Refine = true
  Suppressed = false
  Type = 0
FEATURE [PartDesign::Body] Body004  label="8040 extrusion @ 530"
  AllowCompound = false
  Group = -> [Sketch004,Pad003]
  Origin = -> Origin006
  Tip = -> Pad003
FEATURE [Sketcher::SketchObject] Sketch005
  ArcFitTolerance = 1e-06
  AttachmentSupport = -> [XY_Plane007]
  FullyConstrained = true
  MakeInternals = false
  MapMode = 5
  sketch-geometry (70):
    g0: LineSegment StartX=-20 StartY=4.065 StartZ=0 EndX=-20 EndY=20 EndZ=0
    g1: LineSegment StartX=-20 StartY=20 StartZ=0 EndX=-4.065 EndY=20 EndZ=0
    g2: LineSegment StartX=-4.065 StartY=20 StartZ=0 EndX=-4.065 EndY=15.68 EndZ=0
    g3: LineSegment StartX=-4.065 StartY=15.68 StartZ=0 EndX=-12.6253 EndY=15.68 EndZ=0
    g4: LineSegment StartX=-12.6253 StartY=15.68 StartZ=0 EndX=-5.22957 EndY=8.28427 EndZ=0
    g5: LineSegment StartX=-5.22957 StartY=8.28427 StartZ=0 EndX=5.22957 EndY=8.28427 EndZ=0
    g6: LineSegment StartX=5.22957 StartY=8.28427 StartZ=0 EndX=12.6253 EndY=15.68 EndZ=0
    g7: LineSegment StartX=12.6253 StartY=15.68 StartZ=0 EndX=4.065 EndY=15.68 EndZ=0
    g8: LineSegment StartX=4.065 StartY=15.68 StartZ=0 EndX=4.065 EndY=20 EndZ=0
    g9: LineSegment StartX=4.065 StartY=20 StartZ=0 EndX=20 EndY=20 EndZ=0
    g10: LineSegment StartX=20 StartY=4.065 StartZ=0 EndX=15.68 EndY=4.065 EndZ=0
    g11: LineSegment StartX=15.68 StartY=4.065 StartZ=0 EndX=15.68 EndY=12.6253 EndZ=0
    g12: LineSegment StartX=15.68 StartY=12.6253 StartZ=0 EndX=8.28427 EndY=5.22957 EndZ=0
    g13: LineSegment StartX=8.28427 StartY=5.22957 StartZ=0 EndX=8.28427 EndY=-5.22957 EndZ=0
    g14: LineSegment StartX=8.28427 StartY=-5.22957 StartZ=0 EndX=15.68 EndY=-12.6253 EndZ=0
    g15: LineSegment StartX=15.68 StartY=-12.6253 StartZ=0 EndX=15.68 EndY=-4.065 EndZ=0
    g16: LineSegment StartX=15.68 StartY=-4.065 StartZ=0 EndX=20 EndY=-4.065 EndZ=0
    g17: LineSegment StartX=20 StartY=-20 StartZ=0 EndX=4.065 EndY=-20 EndZ=0
    g18: LineSegment StartX=4.065 StartY=-20 StartZ=0 EndX=4.065 EndY=-15.68 EndZ=0
    g19: LineSegment StartX=4.065 StartY=-15.68 StartZ=0 EndX=12.6253 EndY=-15.68 EndZ=0
    g20: LineSegment StartX=12.6253 StartY=-15.68 StartZ=0 EndX=5.22957 EndY=-8.28427 EndZ=0
    g21: LineSegment StartX=5.22957 StartY=-8.28427 StartZ=0 EndX=-5.22957 EndY=-8.28427 EndZ=0
    g22: LineSegment StartX=-5.22957 StartY=-8.28427 StartZ=0 EndX=-12.6253 EndY=-15.68 EndZ=0
    g23: LineSegment StartX=-12.6253 StartY=-15.68 StartZ=0 EndX=-4.065 EndY=-15.68 EndZ=0
    g24: LineSegment StartX=-4.065 StartY=-15.68 StartZ=0 EndX=-4.065 EndY=-20 EndZ=0
    g25: LineSegment StartX=-4.065 StartY=-20 StartZ=0 EndX=-20 EndY=-20 EndZ=0
    g26: LineSegment StartX=-20 StartY=-20 StartZ=0 EndX=-20 EndY=-4.065 EndZ=0
    g27: LineSegment StartX=-20 StartY=-4.065 StartZ=0 EndX=-15.68 EndY=-4.065 EndZ=0
    g28: LineSegment StartX=-15.68 StartY=-4.065 StartZ=0 EndX=-15.68 EndY=-12.6253 EndZ=0
    g29: LineSegment StartX=-15.68 StartY=-12.6253 StartZ=0 EndX=-8.28427 EndY=-5.22957 EndZ=0
    g30: LineSegment StartX=-8.28427 StartY=-5.22957 StartZ=0 EndX=-8.28427 EndY=5.22957 EndZ=0
    g31: LineSegment StartX=-8.28427 StartY=5.22957 StartZ=0 EndX=-15.68 EndY=12.6253 EndZ=0
    g32: LineSegment StartX=-15.68 StartY=12.6253 StartZ=0 EndX=-15.68 EndY=4.065 EndZ=0
    g33: LineSegment StartX=-15.68 StartY=4.065 StartZ=0 EndX=-20 EndY=4.065 EndZ=0
    g34: Circle CenterX=0 CenterY=0 CenterZ=0 NormalX=0 NormalY=0 NormalZ=1 AngleXU=0 Radius=3.405
    g35: LineSegment StartX=20 StartY=20 StartZ=0 EndX=35.935 EndY=20 EndZ=0
    g36: LineSegment StartX=35.935 StartY=20 StartZ=0 EndX=35.935 EndY=15.68 EndZ=0
    g37: LineSegment StartX=35.935 StartY=15.68 StartZ=0 EndX=27.3747 EndY=15.68 EndZ=0
    g38: LineSegment StartX=27.3747 StartY=15.68 StartZ=0 EndX=34.7704 EndY=8.28427 EndZ=0
    g39: LineSegment StartX=34.7704 StartY=8.28427 StartZ=0 EndX=45.2296 EndY=8.28427 EndZ=0
    g40: LineSegment StartX=45.2296 StartY=8.28427 StartZ=0 EndX=52.6253 EndY=15.68 EndZ=0
    g41: LineSegment StartX=52.6253 StartY=15.68 StartZ=0 EndX=44.065 EndY=15.68 EndZ=0
    g42: LineSegment StartX=44.065 StartY=15.68 StartZ=0 EndX=44.065 EndY=20 EndZ=0
    g43: LineSegment StartX=44.065 StartY=20 StartZ=0 EndX=60 EndY=20 EndZ=0
    g44: LineSegment StartX=60 StartY=20 StartZ=0 EndX=60 EndY=4.065 EndZ=0
    g45: LineSegment StartX=60 StartY=4.065 StartZ=0 EndX=55.68 EndY=4.065 EndZ=0
    g46: LineSegment StartX=55.68 StartY=4.065 StartZ=0 EndX=55.68 EndY=12.6253 EndZ=0
    g47: LineSegment StartX=55.68 StartY=12.6253 StartZ=0 EndX=48.2843 EndY=5.22957 EndZ=0
    g48: LineSegment StartX=48.2843 StartY=5.22957 StartZ=0 EndX=48.2843 EndY=-5.22957 EndZ=0
    g49: LineSegment StartX=48.2843 StartY=-5.22957 StartZ=0 EndX=55.68 EndY=-12.6253 EndZ=0
    g50: LineSegment StartX=55.68 StartY=-12.6253 StartZ=0 EndX=55.68 EndY=-4.065 EndZ=0
    g51: LineSegment StartX=55.68 StartY=-4.065 StartZ=0 EndX=60 EndY=-4.065 EndZ=0
    g52: LineSegment StartX=60 StartY=-4.065 StartZ=0 EndX=60 EndY=-20 EndZ=0
    g53: LineSegment StartX=60 StartY=-20 StartZ=0 EndX=44.065 EndY=-20 EndZ=0
    g54: LineSegment StartX=44.065 StartY=-20 StartZ=0 EndX=44.065 EndY=-15.68 EndZ=0
    g55: LineSegment StartX=44.065 StartY=-15.68 StartZ=0 EndX=52.6253 EndY=-15.68 EndZ=0
    g56: LineSegment StartX=52.6253 StartY=-15.68 StartZ=0 EndX=45.2296 EndY=-8.28427 EndZ=0
    g57: LineSegment StartX=45.2296 StartY=-8.28427 StartZ=0 EndX=34.7704 EndY=-8.28427 EndZ=0
    g58: LineSegment StartX=34.7704 StartY=-8.28427 StartZ=0 EndX=27.3747 EndY=-15.68 EndZ=0
    g59: LineSegment StartX=27.3747 StartY=-15.68 StartZ=0 EndX=35.935 EndY=-15.68 EndZ=0
    g60: LineSegment StartX=35.935 StartY=-15.68 StartZ=0 EndX=35.935 EndY=-20 EndZ=0
    g61: LineSegment StartX=35.935 StartY=-20 StartZ=0 EndX=20 EndY=-20 EndZ=0
    g62: LineSegment StartX=24.32 StartY=12.6253 StartZ=0 EndX=24.32 EndY=4.065 EndZ=0
    g63: LineSegment StartX=24.32 StartY=4.065 StartZ=0 EndX=20 EndY=4.065 EndZ=0
    g64: LineSegment StartX=20 StartY=-4.065 StartZ=0 EndX=24.32 EndY=-4.065 EndZ=0
    g65: LineSegment StartX=24.32 StartY=-4.065 StartZ=0 EndX=24.32 EndY=-12.6253 EndZ=0
    g66: LineSegment StartX=24.32 StartY=-12.6253 StartZ=0 EndX=31.7157 EndY=-5.22957 EndZ=0
    g67: LineSegment StartX=31.7157 StartY=-5.22957 StartZ=0 EndX=31.7157 EndY=5.22957 EndZ=0
    g68: LineSegment StartX=31.7157 StartY=5.22957 StartZ=0 EndX=24.32 EndY=12.6253 EndZ=0
    g69: Circle CenterX=40 CenterY=0 CenterZ=0 NormalX=0 NormalY=0 NormalZ=1 AngleXU=0 Radius=3.405
  constraints (200):
    c: Coincident(g22,g21)
    c: Coincident(g30,g29)
    c: Coincident(g28,g29)
    c: Coincident(g23,g22)
    c: Coincident(g23,g24)
    c: Coincident(g18,g19)
    c: Coincident(g17,g18)
    c: Coincident(g24,g25)
    c: Coincident(g26,g25)
    c: Coincident(g19,g20)
    c: Coincident(g15,g14)
    c: Coincident(g13,g14)
    c: Coincident(g21,g20)
    c: Coincident(g15,g16)
    c: Coincident(g11,g10)
    c: Coincident(g12,g11)
    c: Coincident(g12,g13)
    c: Coincident(g6,g5)
    c: Coincident(g7,g6)
    c: Coincident(g8,g7)
    c: Coincident(g9,g8)
    c: Coincident(g2,g1)
    c: Coincident(g2,g3)
    c: Coincident(g4,g3)
    c: Coincident(g32,g31)
    c: Coincident(g5,g4)
    c: Coincident(g31,g30)
    c: Coincident(g33,g32)
    c: Coincident(g33,g0)
    c: Coincident(g1,g0)
    c: Coincident(g28,g27)
    c: Coincident(g27,g26)
    c: Distance(g9,g0) = 40
    c: Distance(g25,g1) = 40
    c: Tangent(g1,g9)
    c: Tangent(g25,g17)
    c: Tangent(g0,g26)
    c: Horizontal(g1)
    c: Vertical(g0)
    c: Equal(g2,g8)
    c: Equal(g8,g33)
    c: Equal(g33,g27)
    c: Equal(g27,g24)
    c: Equal(g24,g18)
    c: Equal(g18,g16)
    c: Equal(g16,g10)
    c: Vertical(g32)
    c: Vertical(g28)
    c: Vertical(g15)
    c: Vertical(g11)
    c: Vertical(g8)
    c: Vertical(g2)
    c: Vertical(g13)
    c: Vertical(g30)
    c: Horizontal(g33)
    c: Horizontal(g27)
    c: Horizontal(g21)
    c: Horizontal(g17)
    c: Horizontal(g23)
    c: Horizontal(g19)
    c: Horizontal(g7)
    c: Horizontal(g3)
    c: Parallel(g4,g31)
    c: Parallel(g31,g14)
    c: Parallel(g14,g20)
    c: Parallel(g6,g12)
    c: Parallel(g12,g22)
    c: Parallel(g22,g29)
    c: Equal(g21,g22)
    c: Equal(g22,g29)
    c: Equal(g4,g31)
    c: Equal(g6,g12)
    c: Equal(g14,g20)
    c: Angle(g23,g22) = 0.785398
    c: Distance(g8,g2) = 8.13
    c: Distance(g27,g33) = 8.13
    c: Tangent(g33,g10)
    c: Tangent(g16,g27)
    c: Tangent(g2,g24)
    c: Tangent(g8,g18)
    c: Distance(g20,g14) = 4.32
    c: Distance(g12,g6) = 4.32
    c: Distance(g31,g4) = 4.32
    c: Distance(g22,g29) = 4.32
    c: Equal(g30,g13)
    c: Equal(g5,g21)
    c: Equal(g23,g19)
    c: Equal(g32,g28)
    c: Distance(g33,g33) = 4.32
    c: Symmetric(g5,g20,g-1)
    c: Symmetric(g4,g5,g-2)
    c: Equal(g5,g30)
    c: Coincident(g34,g-1)
    c: Diameter(g34) = 6.81
    c: Coincident(g35,g9)
    c: Coincident(g36,g35)
    c: Coincident(g37,g36)
    c: Horizontal(g37)
    c: Coincident(g38,g37)
    c: Coincident(g39,g38)
    c: Horizontal(g39)
    c: Coincident(g41,g40)
    c: Vertical(g44)
    c: Coincident(g45,g44)
    c: Coincident(g48,g47)
    c: Vertical(g48)
    c: Coincident(g49,g48)
    c: Vertical(g50)
    c: Horizontal(g51)
    c: Coincident(g52,g51)
    c: Vertical(g52)
    c: Coincident(g53,g52)
    c: Coincident(g55,g54)
    c: Coincident(g57,g56)
    c: Horizontal(g57)
    c: Coincident(g58,g57)
    c: Coincident(g59,g58)
    c: Horizontal(g59)
    c: Coincident(g61,g60)
    c: Coincident(g61,g17)
    c: Coincident(g63,g10)
    c: Coincident(g64,g16)
    c: Coincident(g65,g64)
    c: Coincident(g66,g65)
    c: Coincident(g67,g66)
    c: Coincident(g68,g67)
    c: Coincident(g68,g62)
    c: PointOnObject(g69,g-1)
    c: Coincident(g43,g42)
    c: Coincident(g43,g44)
    c: Coincident(g41,g42)
    c: Coincident(g39,g40)
    c: Coincident(g46,g47)
    c: Coincident(g46,g45)
    c: Coincident(g50,g51)
    c: Coincident(g49,g50)
    c: Coincident(g54,g53)
    c: Coincident(g56,g55)
    c: Coincident(g59,g60)
    c: Coincident(g62,g63)
    c: Equal(g34,g69)
    c: Equal(g39,g67)
    c: Equal(g67,g57)
    c: Equal(g57,g48)
    c: Equal(g48,g13)
    c: Equal(g38,g68)
    c: Equal(g68,g66)
    c: Equal(g66,g58)
    c: Equal(g58,g56)
    c: Equal(g56,g49)
    c: Equal(g49,g47)
    c: Equal(g47,g40)
    c: Equal(g40,g12)
    c: Equal(g10,g63)
    c: Equal(g16,g64)
    c: Equal(g64,g45)
    c: Equal(g45,g51)
    c: Equal(g51,g42)
    c: Equal(g42,g36)
    c: Equal(g36,g60)
    c: Equal(g60,g54)
    c: Parallel(g47,g40)
    c: Parallel(g38,g68)
    c: Parallel(g66,g58)
    c: Parallel(g49,g56)
    c: Parallel(g56,g68)
    c: Parallel(g40,g66)
    c: Horizontal(g35)
    c: Horizontal(g43)
    c: Horizontal(g45)
    c: Horizontal(g53)
    c: Horizontal(g61)
    c: Horizontal(g64)
    c: Horizontal(g63)
    c: Horizontal(g41)
    c: Vertical(g42)
    c: Vertical(g36)
    c: Vertical(g62)
    c: Vertical(g65)
    c: Vertical(g60)
    c: Vertical(g54)
    c: Vertical(g46)
    c: Horizontal(g55)
    c: Vertical(g67)
    c: Equal(g7,g37)
    c: Equal(g37,g41)
    c: Equal(g41,g46)
    c: Equal(g46,g55)
    c: Equal(g55,g59)
    c: Equal(g59,g65)
    c: Equal(g65,g62)
    c: Equal(g55,g50)
    c: Parallel(g40,g6)
    c: Distance(g9,g44) = 40
    c: DistanceX(g34,g69) = 40
    c: Equal(g35,g43)
    c: Equal(g43,g9)
    c: Equal(g44,g52)
    c: Equal(g53,g61)
    c: Equal(g61,g17)
FEATURE [PartDesign::Pad] Pad004
  Direction = (0,0,1)
  Length = 470
  Length2 = 10
  Profile = -> Sketch005
  ReferenceAxis = -> Sketch005 [N_Axis]
  Refine = true
  Suppressed = false
  Type = 0
FEATURE [PartDesign::Body] Body005  label="8040 extrusion @ 470"
  AllowCompound = false
  Group = -> [Sketch005,Pad004]
  Origin = -> Origin007
  Tip = -> Pad004
FEATURE [Sketcher::SketchObject] Sketch006
  ArcFitTolerance = 1e-06
  AttachmentSupport = -> [XY_Plane008]
  FullyConstrained = true
  MakeInternals = false
  MapMode = 5
  sketch-geometry (37):
    g0: LineSegment StartX=-20 StartY=4.065 StartZ=0 EndX=-20 EndY=20 EndZ=0
    g1: LineSegment StartX=-20 StartY=20 StartZ=0 EndX=-4.065 EndY=20 EndZ=0
    g2: LineSegment StartX=-4.065 StartY=20 StartZ=0 EndX=-4.065 EndY=15.68 EndZ=0
    g3: LineSegment StartX=-4.065 StartY=15.68 StartZ=0 EndX=-12.6253 EndY=15.68 EndZ=0
    g4: LineSegment StartX=-12.6253 StartY=15.68 StartZ=0 EndX=-5.22957 EndY=8.28427 EndZ=0
    g5: LineSegment StartX=-5.22957 StartY=8.28427 StartZ=0 EndX=5.22957 EndY=8.28427 EndZ=0
    g6: LineSegment StartX=5.22957 StartY=8.28427 StartZ=0 EndX=12.6253 EndY=15.68 EndZ=0
    g7: LineSegment StartX=12.6253 StartY=15.68 StartZ=0 EndX=4.065 EndY=15.68 EndZ=0
    g8: LineSegment StartX=4.065 StartY=15.68 StartZ=0 EndX=4.065 EndY=20 EndZ=0
    g9: LineSegment StartX=4.065 StartY=20 StartZ=0 EndX=20 EndY=20 EndZ=0
    g10: LineSegment StartX=20 StartY=20 StartZ=0 EndX=20 EndY=4.065 EndZ=0
    g11: LineSegment StartX=20 StartY=4.065 StartZ=0 EndX=15.68 EndY=4.065 EndZ=0
    g12: LineSegment StartX=15.68 StartY=4.065 StartZ=0 EndX=15.68 EndY=12.6253 EndZ=0
    g13: LineSegment StartX=15.68 StartY=12.6253 StartZ=0 EndX=8.28427 EndY=5.22957 EndZ=0
    g14: LineSegment StartX=8.28427 StartY=5.22957 StartZ=0 EndX=8.28427 EndY=-5.22957 EndZ=0
    g15: LineSegment StartX=8.28427 StartY=-5.22957 StartZ=0 EndX=15.68 EndY=-12.6253 EndZ=0
    g16: LineSegment StartX=15.68 StartY=-12.6253 StartZ=0 EndX=15.68 EndY=-4.065 EndZ=0
    g17: LineSegment StartX=15.68 StartY=-4.065 StartZ=0 EndX=20 EndY=-4.065 EndZ=0
    g18: LineSegment StartX=20 StartY=-4.065 StartZ=0 EndX=20 EndY=-20 EndZ=0
    g19: LineSegment StartX=20 StartY=-20 StartZ=0 EndX=4.065 EndY=-20 EndZ=0
    g20: LineSegment StartX=4.065 StartY=-20 StartZ=0 EndX=4.065 EndY=-15.68 EndZ=0
    g21: LineSegment StartX=4.065 StartY=-15.68 StartZ=0 EndX=12.6253 EndY=-15.68 EndZ=0
    g22: LineSegment StartX=12.6253 StartY=-15.68 StartZ=0 EndX=5.22957 EndY=-8.28427 EndZ=0
    g23: LineSegment StartX=5.22957 StartY=-8.28427 StartZ=0 EndX=-5.22957 EndY=-8.28427 EndZ=0
    g24: LineSegment StartX=-5.22957 StartY=-8.28427 StartZ=0 EndX=-12.6253 EndY=-15.68 EndZ=0
    g25: LineSegment StartX=-12.6253 StartY=-15.68 StartZ=0 EndX=-4.065 EndY=-15.68 EndZ=0
    g26: LineSegment StartX=-4.065 StartY=-15.68 StartZ=0 EndX=-4.065 EndY=-20 EndZ=0
    g27: LineSegment StartX=-4.065 StartY=-20 StartZ=0 EndX=-20 EndY=-20 EndZ=0
    g28: LineSegment StartX=-20 StartY=-20 StartZ=0 EndX=-20 EndY=-4.065 EndZ=0
    g29: LineSegment StartX=-20 StartY=-4.065 StartZ=0 EndX=-15.68 EndY=-4.065 EndZ=0
    g30: LineSegment StartX=-15.68 StartY=-4.065 StartZ=0 EndX=-15.68 EndY=-12.6253 EndZ=0
    g31: LineSegment StartX=-15.68 StartY=-12.6253 StartZ=0 EndX=-8.28427 EndY=-5.22957 EndZ=0
    g32: LineSegment StartX=-8.28427 StartY=-5.22957 StartZ=0 EndX=-8.28427 EndY=5.22957 EndZ=0
    g33: LineSegment StartX=-8.28427 StartY=5.22957 StartZ=0 EndX=-15.68 EndY=12.6253 EndZ=0
    g34: LineSegment StartX=-15.68 StartY=12.6253 StartZ=0 EndX=-15.68 EndY=4.065 EndZ=0
    g35: LineSegment StartX=-15.68 StartY=4.065 StartZ=0 EndX=-20 EndY=4.065 EndZ=0
    g36: Circle CenterX=0 CenterY=0 CenterZ=0 NormalX=0 NormalY=0 NormalZ=1 AngleXU=0 Radius=3.405
  constraints (100):
    c: Coincident(g24,g23)
    c: Coincident(g32,g31)
    c: Coincident(g30,g31)
    c: Coincident(g25,g24)
    c: Coincident(g25,g26)
    c: Coincident(g20,g21)
    c: Coincident(g19,g20)
    c: Coincident(g26,g27)
    c: Coincident(g28,g27)
    c: Coincident(g21,g22)
    c: Coincident(g19,g18)
    c: Coincident(g16,g15)
    c: Coincident(g14,g15)
    c: Coincident(g23,g22)
    c: Coincident(g16,g17)
    c: Coincident(g18,g17)
    c: Coincident(g12,g11)
    c: Coincident(g11,g10)
    c: Coincident(g10,g9)
    c: Coincident(g13,g12)
    c: Coincident(g13,g14)
    c: Coincident(g6,g5)
    c: Coincident(g7,g6)
    c: Coincident(g8,g7)
    c: Coincident(g9,g8)
    c: Coincident(g2,g1)
    c: Coincident(g2,g3)
    c: Coincident(g4,g3)
    c: Coincident(g34,g33)
    c: Coincident(g5,g4)
    c: Coincident(g33,g32)
    c: Coincident(g35,g34)
    c: Coincident(g35,g0)
    c: Coincident(g1,g0)
    c: Coincident(g30,g29)
    c: Coincident(g29,g28)
    c: Distance(g10,g0) = 40
    c: Distance(g27,g1) = 40
    c: Tangent(g1,g9)
    c: Tangent(g27,g19)
    c: Tangent(g0,g28)
    c: Tangent(g10,g18)
    c: Horizontal(g1)
    c: Vertical(g0)
    c: Equal(g2,g8)
    c: Equal(g8,g35)
    c: Equal(g35,g29)
    c: Equal(g29,g26)
    c: Equal(g26,g20)
    c: Equal(g20,g17)
    c: Equal(g17,g11)
    c: Vertical(g34)
    c: Vertical(g30)
    c: Vertical(g16)
    c: Vertical(g18)
    c: Vertical(g12)
    c: Vertical(g8)
    c: Vertical(g2)
    c: Vertical(g14)
    c: Vertical(g32)
    c: Horizontal(g35)
    c: Horizontal(g29)
    c: Horizontal(g23)
    c: Horizontal(g19)
    c: Horizontal(g25)
    c: Horizontal(g21)
    c: Horizontal(g7)
    c: Horizontal(g3)
    c: Parallel(g4,g33)
    c: Parallel(g33,g15)
    c: Parallel(g15,g22)
    c: Parallel(g6,g13)
    c: Parallel(g13,g24)
    c: Parallel(g24,g31)
    c: Equal(g23,g24)
    c: Equal(g24,g31)
    c: Equal(g4,g33)
    c: Equal(g6,g13)
    c: Equal(g15,g22)
    c: Angle(g25,g24) = 0.785398
    c: Distance(g8,g2) = 8.13
    c: Distance(g29,g35) = 8.13
    c: Tangent(g35,g11)
    c: Tangent(g17,g29)
    c: Tangent(g2,g26)
    c: Tangent(g8,g20)
    c: Distance(g22,g15) = 4.32
    c: Distance(g13,g6) = 4.32
    c: Distance(g33,g4) = 4.32
    c: Distance(g24,g31) = 4.32
    c: Equal(g32,g14)
    c: Equal(g5,g23)
    c: Equal(g25,g21)
    c: Equal(g34,g30)
    c: Distance(g35,g35) = 4.32
    c: Symmetric(g5,g22,g-1)
    c: Symmetric(g4,g5,g-2)
    c: Equal(g5,g32)
    c: Coincident(g36,g-1)
    c: Diameter(g36) = 6.81
FEATURE [PartDesign::Pad] Pad005
  Direction = (0,0,1)
  Length = 100
  Length2 = 10
  Profile = -> Sketch006
  ReferenceAxis = -> Sketch006 [N_Axis]
  Refine = true
  Suppressed = false
  Type = 0
FEATURE [PartDesign::Body] Body006  label="4040 extrusion @ 100"
  AllowCompound = false
  Group = -> [Sketch006,Pad005]
  Origin = -> Origin008
  Tip = -> Pad005
FEATURE [Sketcher::SketchObject] Sketch010
  ArcFitTolerance = 1e-06
  AttachmentSupport = -> [XY_Plane]
  FullyConstrained = true
  MakeInternals = false
  MapMode = 5
  sketch-geometry (10):
    g0: LineSegment StartX=-10 StartY=0 StartZ=0 EndX=10 EndY=0 EndZ=0
    g1: LineSegment StartX=10 StartY=0 StartZ=0 EndX=10 EndY=8.5 EndZ=0
    g2: LineSegment StartX=-10 StartY=0 StartZ=0 EndX=-10 EndY=8.5 EndZ=0
    g3: LineSegment StartX=-10 StartY=14.5 StartZ=0 EndX=-10 EndY=17.7218 EndZ=0
    g4: LineSegment StartX=-10 StartY=17.7218 StartZ=0 EndX=-7.72183 EndY=20 EndZ=0
    g5: LineSegment StartX=-7.72183 StartY=20 StartZ=0 EndX=7.72183 EndY=20 EndZ=0
    g6: LineSegment StartX=7.72183 StartY=20 StartZ=0 EndX=10 EndY=17.7218 EndZ=0
    g7: LineSegment StartX=10 StartY=17.7218 StartZ=0 EndX=10 EndY=14.5 EndZ=0
    g8: ArcOfCircle CenterX=-10 CenterY=11.5 CenterZ=0 NormalX=0 NormalY=0 NormalZ=1 AngleXU=0 Radius=3 StartAngle=4.71239 EndAngle=7.85398
    g9: ArcOfCircle CenterX=9.99998 CenterY=11.5 CenterZ=0 NormalX=0 NormalY=0 NormalZ=1 AngleXU=0 Radius=3 StartAngle=1.57079 EndAngle=4.7124
  constraints (30):
    c: Coincident(g1,g0)
    c: Coincident(g2,g0)
    c: Coincident(g4,g3)
    c: Coincident(g5,g4)
    c: Horizontal(g5)
    c: Coincident(g6,g5)
    c: Coincident(g7,g6)
    c: Vertical(g7)
    c: Coincident(g8,g3)
    c: Coincident(g8,g2)
    c: Coincident(g9,g1)
    c: Coincident(g9,g7)
    c: Equal(g8,g9)
    c: Equal(g1,g2)
    c: Equal(g3,g7)
    c: Equal(g6,g4)
    c: Distance(g0,g0) = 20
    c: Symmetric(g0,g0,g-2)
    c: Vertical(g2)
    c: Vertical(g1)
    c: Tangent(g3,g2)
    c: PointOnObject(g7,g1)
    c: Radius(g8) = 3
    c: Angle(g4,g3) = 0.785398
    c: Angle(g6,g7) = 2.35619
    c: Distance(g0,g5) = 20
    c: PointOnObject(g8,g3)
    c: Distance(g8,g5) = 8.5
    c: PointOnObject(g-1,g0)
    c: Equal(g4,g3)
FEATURE [PartDesign::Pad] Pad006
  Direction = (0,0,1)
  Length = 500
  Length2 = 10
  Profile = -> Sketch010
  ReferenceAxis = -> Sketch010 [N_Axis]
  Refine = true
  Suppressed = false
  Type = 0
FEATURE [PartDesign::Body] Body  label="HGR20x500"
  AllowCompound = false
  Group = -> [Sketch010,Pad006]
  Origin = -> Origin
  Tip = -> Pad006
FEATURE [Sketcher::SketchObject] Sketch011
  ArcFitTolerance = 1e-06
  AttachmentSupport = -> [XY_Plane009]
  FullyConstrained = true
  MakeInternals = false
  MapMode = 5
  sketch-geometry (14):
    g0: LineSegment StartX=10 StartY=0 StartZ=0 EndX=10 EndY=3.9 EndZ=0
    g1: LineSegment StartX=-10 StartY=0 StartZ=0 EndX=-10 EndY=3.9 EndZ=0
    g2: LineSegment StartX=-10 StartY=9.9 StartZ=0 EndX=-10 EndY=13.1218 EndZ=0
    g3: LineSegment StartX=-10 StartY=13.1218 StartZ=0 EndX=-7.72183 EndY=15.4 EndZ=0
    g4: LineSegment StartX=-7.72183 StartY=15.4 StartZ=0 EndX=7.72183 EndY=15.4 EndZ=0
    g5: LineSegment StartX=7.72183 StartY=15.4 StartZ=0 EndX=10 EndY=13.1218 EndZ=0
    g6: LineSegment StartX=10 StartY=13.1218 StartZ=0 EndX=10 EndY=9.9 EndZ=0
    g7: ArcOfCircle CenterX=-10 CenterY=6.9 CenterZ=0 NormalX=0 NormalY=0 NormalZ=1 AngleXU=0 Radius=3 StartAngle=4.71239 EndAngle=7.85398
    g8: ArcOfCircle CenterX=10 CenterY=6.9 CenterZ=0 NormalX=0 NormalY=0 NormalZ=1 AngleXU=0 Radius=3 StartAngle=1.5708 EndAngle=4.71238
    g9: LineSegment StartX=-21 StartY=0 StartZ=0 EndX=-21 EndY=25.4 EndZ=0
    g10: LineSegment StartX=-21 StartY=25.4 StartZ=0 EndX=21 EndY=25.4 EndZ=0
    g11: LineSegment StartX=21 StartY=25.4 StartZ=0 EndX=21 EndY=0 EndZ=0
    g12: LineSegment StartX=21 StartY=0 StartZ=0 EndX=10 EndY=0 EndZ=0
    g13: LineSegment StartX=-21 StartY=0 StartZ=0 EndX=-10 EndY=0 EndZ=0
  constraints (42):
    c: Coincident(g3,g2)
    c: Coincident(g4,g3)
    c: Horizontal(g4)
    c: Coincident(g5,g4)
    c: Coincident(g6,g5)
    c: Vertical(g6)
    c: Coincident(g7,g2)
    c: Coincident(g7,g1)
    c: Coincident(g8,g0)
    c: Coincident(g8,g6)
    c: Equal(g7,g8)
    c: Equal(g0,g1)
    c: Equal(g2,g6)
    c: Equal(g5,g3)
    c: Distance(g1,g0) = 20
    c: Symmetric(g1,g0,g-2)
    c: Vertical(g1)
    c: Vertical(g0)
    c: Tangent(g2,g1)
    c: PointOnObject(g6,g0)
    c: Radius(g7) = 3
    c: Angle(g3,g2) = 0.785398
    c: Angle(g5,g6) = 2.35619
    c: PointOnObject(g7,g2)
    c: Distance(g7,g4) = 8.5
    c: Equal(g3,g2)
    c: Vertical(g9)
    c: Coincident(g10,g9)
    c: Horizontal(g10)
    c: Coincident(g11,g10)
    c: PointOnObject(g11,g-1)
    c: Vertical(g11)
    c: Coincident(g12,g11)
    c: DistanceX(g10,g10) = 42
    c: Coincident(g12,g0)
    c: DistanceY(g9,g9) = 25.4
    c: Coincident(g13,g9)
    c: Coincident(g13,g1)
    c: Horizontal(g13)
    c: Equal(g13,g12)
    c: Horizontal(g12)
    c: Distance(g10,g4) = 10
FEATURE [PartDesign::Pad] Pad007
  Direction = (0,0,1)
  Length = 73
  Length2 = 10
  Profile = -> Sketch011
  ReferenceAxis = -> Sketch011 [N_Axis]
  Refine = true
  Suppressed = false
  Type = 0
FEATURE [Sketcher::SketchObject] Sketch012
  ArcFitTolerance = 1e-06
  AttachmentSupport = -> [Pad007]
  FullyConstrained = true
  MakeInternals = false
  MapMode = 5
  Placement = pos=(0,25.4,0) rot=(0,0.707107,0.707107;3.14159rad)
  sketch-geometry (8):
    g0: Circle CenterX=-16 CenterY=54.5 CenterZ=0 NormalX=0 NormalY=0 NormalZ=1 AngleXU=0 Radius=2.5
    g1: Circle CenterX=16 CenterY=54.5 CenterZ=0 NormalX=0 NormalY=0 NormalZ=1 AngleXU=0 Radius=2.5
    g2: Circle CenterX=-16 CenterY=18.5 CenterZ=0 NormalX=0 NormalY=0 NormalZ=1 AngleXU=0 Radius=2.5
    g3: Circle CenterX=16 CenterY=18.5 CenterZ=0 NormalX=0 NormalY=0 NormalZ=1 AngleXU=0 Radius=2.5
    g4: LineSegment [constr] StartX=-16 StartY=54.5 StartZ=0 EndX=16 EndY=54.5 EndZ=0
    g5: LineSegment [constr] StartX=-16 StartY=18.5 StartZ=0 EndX=16 EndY=18.5 EndZ=0
    g6: LineSegment [constr] StartX=16 StartY=54.5 StartZ=0 EndX=16 EndY=18.5 EndZ=0
    g7: LineSegment [constr] StartX=-16 StartY=54.5 StartZ=0 EndX=-16 EndY=18.5 EndZ=0
  constraints (19):
    c: Equal(g1,g0)
    c: Equal(g0,g3)
    c: Equal(g3,g2)
    c: Diameter(g0) = 5
    c: DistanceY(g3,g1) = 36
    c: Coincident(g4,g0)
    c: Coincident(g4,g1)
    c: Coincident(g5,g2)
    c: Coincident(g5,g3)
    c: Horizontal(g5)
    c: Coincident(g6,g1)
    c: Coincident(g6,g3)
    c: Vertical(g6)
    c: Coincident(g7,g0)
    c: Coincident(g7,g2)
    c: Vertical(g7)
    c: DistanceX(g4,g4) = 32
    c: Symmetric(g0,g1,g-2)
    c: Distance(g-1,g5) = 18.5
FEATURE [Sketcher::SketchObject] Sketch013
  ArcFitTolerance = 1e-06
  AttachmentSupport = -> [XY_Plane010]
  FullyConstrained = true
  MakeInternals = false
  MapMode = 5
  sketch-geometry (56):
    g0: LineSegment StartX=-152.4 StartY=152.4 StartZ=0 EndX=-152.4 EndY=-152.4 EndZ=0
    g1: LineSegment StartX=-152.4 StartY=-152.4 StartZ=0 EndX=152.4 EndY=-152.4 EndZ=0
    g2: LineSegment StartX=152.4 StartY=-152.4 StartZ=0 EndX=152.4 EndY=152.4 EndZ=0
    g3: LineSegment StartX=152.4 StartY=152.4 StartZ=0 EndX=-152.4 EndY=152.4 EndZ=0
    g4: Circle CenterX=-98 CenterY=116 CenterZ=0 NormalX=0 NormalY=0 NormalZ=1 AngleXU=0 Radius=2.5
    g5: Circle CenterX=-62 CenterY=116 CenterZ=0 NormalX=0 NormalY=0 NormalZ=1 AngleXU=0 Radius=2.5
    g6: Circle CenterX=-98 CenterY=84 CenterZ=0 NormalX=0 NormalY=0 NormalZ=1 AngleXU=0 Radius=2.5
    g7: Circle CenterX=-62 CenterY=84 CenterZ=0 NormalX=0 NormalY=0 NormalZ=1 AngleXU=0 Radius=2.5
    g8: Circle CenterX=-98 CenterY=-84 CenterZ=0 NormalX=0 NormalY=0 NormalZ=1 AngleXU=0 Radius=2.5
    g9: Circle CenterX=-62 CenterY=-84 CenterZ=0 NormalX=0 NormalY=0 NormalZ=1 AngleXU=0 Radius=2.5
    g10: Circle CenterX=-98 CenterY=-116 CenterZ=0 NormalX=0 NormalY=0 NormalZ=1 AngleXU=0 Radius=2.5
    g11: Circle CenterX=-62 CenterY=-116 CenterZ=0 NormalX=0 NormalY=0 NormalZ=1 AngleXU=0 Radius=2.5
    g12: Circle CenterX=62 CenterY=116 CenterZ=0 NormalX=0 NormalY=0 NormalZ=1 AngleXU=0 Radius=2.5
    g13: Circle CenterX=98 CenterY=116 CenterZ=0 NormalX=0 NormalY=0 NormalZ=1 AngleXU=0 Radius=2.5
    g14: Circle CenterX=62 CenterY=84 CenterZ=0 NormalX=0 NormalY=0 NormalZ=1 AngleXU=0 Radius=2.5
    g15: Circle CenterX=98 CenterY=84 CenterZ=0 NormalX=0 NormalY=0 NormalZ=1 AngleXU=0 Radius=2.5
    g16: Circle CenterX=62 CenterY=-84 CenterZ=0 NormalX=0 NormalY=0 NormalZ=1 AngleXU=0 Radius=2.5
    g17: Circle CenterX=98 CenterY=-84 CenterZ=0 NormalX=0 NormalY=0 NormalZ=1 AngleXU=0 Radius=2.5
    g18: Circle CenterX=62 CenterY=-116 CenterZ=0 NormalX=0 NormalY=0 NormalZ=1 AngleXU=0 Radius=2.5
    g19: Circle CenterX=98 CenterY=-116 CenterZ=0 NormalX=0 NormalY=0 NormalZ=1 AngleXU=0 Radius=2.5
    g20: LineSegment [constr] StartX=-98 StartY=116 StartZ=0 EndX=98 EndY=116 EndZ=0
    g21: LineSegment [constr] StartX=98 StartY=116 StartZ=0 EndX=98 EndY=-116 EndZ=0
    g22: LineSegment [constr] StartX=98 StartY=-116 StartZ=0 EndX=-98 EndY=-116 EndZ=0
    g23: LineSegment [constr] StartX=-98 StartY=-116 StartZ=0 EndX=-98 EndY=116 EndZ=0
    g24: LineSegment [constr] StartX=-98 StartY=84 StartZ=0 EndX=98 EndY=84 EndZ=0
    g25: LineSegment [constr] StartX=-98 StartY=-84 StartZ=0 EndX=98 EndY=-84 EndZ=0
    g26: LineSegment [constr] StartX=62 StartY=116 StartZ=0 EndX=62 EndY=-116 EndZ=0
    g27: LineSegment [constr] StartX=-62 StartY=-116 StartZ=0 EndX=-62 EndY=116 EndZ=0
    g28: LineSegment [constr] StartX=-12 StartY=17.5 StartZ=0 EndX=-12 EndY=-17.5 EndZ=0
    g29: LineSegment [constr] StartX=-12 StartY=-17.5 StartZ=0 EndX=12 EndY=-17.5 EndZ=0
    g30: LineSegment [constr] StartX=12 StartY=-17.5 StartZ=0 EndX=12 EndY=17.5 EndZ=0
    g31: LineSegment [constr] StartX=12 StartY=17.5 StartZ=0 EndX=-12 EndY=17.5 EndZ=0
    g32: Circle CenterX=-12 CenterY=17.5 CenterZ=0 NormalX=0 NormalY=0 NormalZ=1 AngleXU=0 Radius=2.5
    g33: Circle CenterX=12 CenterY=17.5 CenterZ=0 NormalX=0 NormalY=0 NormalZ=1 AngleXU=0 Radius=2.5
    g34: Circle CenterX=12 CenterY=-17.5 CenterZ=0 NormalX=0 NormalY=0 NormalZ=1 AngleXU=0 Radius=2.5
    g35: Circle CenterX=-12 CenterY=-17.5 CenterZ=0 NormalX=0 NormalY=0 NormalZ=1 AngleXU=0 Radius=2.5
    g36: Circle CenterX=-98 CenterY=116 CenterZ=0 NormalX=0 NormalY=0 NormalZ=1 AngleXU=0 Radius=4.5
    g37: Circle CenterX=-62 CenterY=116 CenterZ=0 NormalX=0 NormalY=0 NormalZ=1 AngleXU=0 Radius=4.5
    g38: Circle CenterX=-62 CenterY=84 CenterZ=0 NormalX=0 NormalY=0 NormalZ=1 AngleXU=0 Radius=4.5
    g39: Circle CenterX=-98 CenterY=84 CenterZ=0 NormalX=0 NormalY=0 NormalZ=1 AngleXU=0 Radius=4.5
    g40: Circle CenterX=-98 CenterY=-84 CenterZ=0 NormalX=0 NormalY=0 NormalZ=1 AngleXU=0 Radius=4.5
    g41: Circle CenterX=-62 CenterY=-84 CenterZ=0 NormalX=0 NormalY=0 NormalZ=1 AngleXU=0 Radius=4.5
    g42: Circle CenterX=-62 CenterY=-116 CenterZ=0 NormalX=0 NormalY=0 NormalZ=1 AngleXU=0 Radius=4.5
    g43: Circle CenterX=-98 CenterY=-116 CenterZ=0 NormalX=0 NormalY=0 NormalZ=1 AngleXU=0 Radius=4.5
    g44: Circle CenterX=62 CenterY=-116 CenterZ=0 NormalX=0 NormalY=0 NormalZ=1 AngleXU=0 Radius=4.5
    g45: Circle CenterX=62 CenterY=-84 CenterZ=0 NormalX=0 NormalY=0 NormalZ=1 AngleXU=0 Radius=4.5
    g46: Circle CenterX=98 CenterY=-84 CenterZ=0 NormalX=0 NormalY=0 NormalZ=1 AngleXU=0 Radius=4.5
    g47: Circle CenterX=98 CenterY=-116 CenterZ=0 NormalX=0 NormalY=0 NormalZ=1 AngleXU=0 Radius=4.5
    g48: Circle CenterX=98 CenterY=116 CenterZ=0 NormalX=0 NormalY=0 NormalZ=1 AngleXU=0 Radius=4.5
    g49: Circle CenterX=98 CenterY=84 CenterZ=0 NormalX=0 NormalY=0 NormalZ=1 AngleXU=0 Radius=4.5
    g50: Circle CenterX=62 CenterY=116 CenterZ=0 NormalX=0 NormalY=0 NormalZ=1 AngleXU=0 Radius=4.5
    g51: Circle CenterX=62 CenterY=84 CenterZ=0 NormalX=0 NormalY=0 NormalZ=1 AngleXU=0 Radius=4.5
    g52: Circle CenterX=-12 CenterY=17.5 CenterZ=0 NormalX=0 NormalY=0 NormalZ=1 AngleXU=0 Radius=4.5
    g53: Circle CenterX=12 CenterY=17.5 CenterZ=0 NormalX=0 NormalY=0 NormalZ=1 AngleXU=0 Radius=4.5
    g54: Circle CenterX=-12 CenterY=-17.5 CenterZ=0 NormalX=0 NormalY=0 NormalZ=1 AngleXU=0 Radius=4.5
    g55: Circle CenterX=12 CenterY=-17.5 CenterZ=0 NormalX=0 NormalY=0 NormalZ=1 AngleXU=0 Radius=4.5
  constraints (130):
    c: Coincident(g0,g1)
    c: Coincident(g1,g2)
    c: Coincident(g2,g3)
    c: Coincident(g3,g0)
    c: Vertical(g2)
    c: Horizontal(g1)
    c: Equal(g17,g16)
    c: Equal(g16,g18)
    c: Equal(g18,g19)
    c: Equal(g19,g14)
    c: Equal(g14,g15)
    c: Equal(g15,g13)
    c: Equal(g13,g12)
    c: Equal(g12,g5)
    c: Equal(g5,g4)
    c: Equal(g4,g6)
    c: Equal(g6,g7)
    c: Equal(g7,g8)
    c: Equal(g8,g9)
    c: Equal(g9,g11)
    c: Equal(g11,g10)
    c: Diameter(g4) = 5
    c: Coincident(g20,g4)
    c: Coincident(g20,g13)
    c: Coincident(g21,g13)
    c: Coincident(g21,g19)
    c: Coincident(g22,g19)
    c: Coincident(g22,g10)
    c: Coincident(g23,g10)
    c: Coincident(g23,g4)
    c: PointOnObject(g6,g23)
    c: PointOnObject(g8,g23)
    c: PointOnObject(g11,g22)
    c: PointOnObject(g18,g22)
    c: PointOnObject(g17,g21)
    c: PointOnObject(g15,g21)
    c: PointOnObject(g12,g20)
    c: PointOnObject(g5,g20)
    c: Vertical(g21)
    c: Horizontal(g22)
    c: Coincident(g24,g6)
    c: Horizontal(g24)
    c: Coincident(g25,g8)
    c: Coincident(g25,g17)
    c: Coincident(g26,g12)
    c: Coincident(g26,g18)
    c: Vertical(g26)
    c: Coincident(g27,g11)
    c: Coincident(g27,g5)
    c: Vertical(g27)
    c: Horizontal(g25)
    c: PointOnObject(g9,g25)
    c: PointOnObject(g9,g27)
    c: PointOnObject(g7,g24)
    c: PointOnObject(g7,g27)
    c: PointOnObject(g14,g24)
    c: PointOnObject(g14,g26)
    c: Coincident(g15,g24)
    c: PointOnObject(g16,g26)
    c: PointOnObject(g16,g25)
    c: Distance(g24,g20) = 32
    c: Distance(g25,g22) = 32
    c: Distance(g27,g23) = 36
    c: Distance(g21,g26) = 36
    c: Distance(g1,g3) = 304.8
    c: Distance(g2,g0) = 304.8
    c: Symmetric(g5,g12,g-2)
    c: Symmetric(g10,g4,g-1)
    c: Symmetric(g0,g0,g-1)
    c: Symmetric(g0,g2,g-2)
    c: DistanceY(g9,g5) = 200
    c: Distance(g26,g23) = 160
    c: Coincident(g28,g29)
    c: Coincident(g29,g30)
    c: Coincident(g30,g31)
    c: Coincident(g31,g28)
    c: Vertical(g30)
    c: Horizontal(g29)
    c: DistanceY(g30,g30) = 35
    c: DistanceX(g31,g31) = 24
    c: Symmetric(g28,g30,g-2)
    c: Symmetric(g28,g28,g-1)
    c: Coincident(g32,g28)
    c: Coincident(g33,g30)
    c: Coincident(g34,g29)
    c: Coincident(g35,g28)
    c: Equal(g32,g33)
    c: Equal(g33,g35)
    c: Equal(g35,g34)
    c: Diameter(g32) = 5
    c: Coincident(g36,g4)
    c: Coincident(g37,g5)
    c: Coincident(g38,g7)
    c: Coincident(g39,g6)
    c: Coincident(g40,g8)
    c: Coincident(g41,g9)
    c: Coincident(g42,g11)
    c: Coincident(g43,g10)
    c: Coincident(g44,g18)
    c: Coincident(g45,g16)
    c: Coincident(g46,g17)
    c: Coincident(g47,g19)
    c: Coincident(g48,g13)
    c: Coincident(g49,g15)
    c: Coincident(g50,g12)
    c: Coincident(g51,g14)
    c: Coincident(g52,g28)
    c: Coincident(g53,g30)
    c: Coincident(g54,g28)
    c: Coincident(g55,g29)
    c: Equal(g55,g54)
    c: Equal(g54,g52)
    c: Equal(g52,g53)
    c: Equal(g53,g36)
    c: Equal(g36,g37)
    c: Equal(g37,g38)
    c: Equal(g38,g39)
    c: Equal(g39,g50)
    c: Equal(g50,g48)
    c: Equal(g48,g49)
    c: Equal(g49,g51)
    c: Equal(g51,g46)
    c: Equal(g46,g47)
    c: Equal(g47,g44)
    c: Equal(g44,g45)
    c: Equal(g45,g40)
    c: Equal(g40,g41)
    c: Equal(g41,g43)
    c: Equal(g43,g42)
    c: Diameter(g37) = 9
FEATURE [PartDesign::Pocket] Pocket
  BaseFeature = -> Pad007
  Direction = (0,-1,2e-16)
  Length = 5
  Length2 = 5
  Profile = -> Sketch012
  ReferenceAxis = -> Sketch012 [N_Axis]
  Refine = true
  Suppressed = false
  Type = 0
FEATURE [PartDesign::Body] Body007  label="HGR20 carriage"
  AllowCompound = false
  Group = -> [Sketch011,Pad007,Sketch012,Pocket]
  Origin = -> Origin009
  Tip = -> Pocket
FEATURE [Part::Box] Box001  label="gusset bracket001"
  AttacherType = Attacher::AttachEngine3D
  Height = 35
  Length = 40
  Width = 40
FEATURE [Sketcher::SketchObject] Sketch014
  ArcFitTolerance = 1e-06
  AttachmentSupport = -> [Box001]
  FullyConstrained = true
  MakeInternals = false
  MapMode = 5
  Placement = pos=(0,0,35) rot=(0,0,1;0rad)
  sketch-geometry (5):
    g0: LineSegment StartX=5 StartY=50 StartZ=0 EndX=5 EndY=35 EndZ=0
    g1: LineSegment StartX=5 StartY=35 StartZ=0 EndX=35 EndY=5 EndZ=0
    g2: LineSegment StartX=35 StartY=5 StartZ=0 EndX=50 EndY=5 EndZ=0
    g3: LineSegment StartX=50 StartY=5 StartZ=0 EndX=50 EndY=50 EndZ=0
    g4: LineSegment StartX=50 StartY=50 StartZ=0 EndX=5 EndY=50 EndZ=0
  constraints (15):
    c: Vertical(g0)
    c: Coincident(g0,g1)
    c: Coincident(g1,g2)
    c: Horizontal(g2)
    c: Coincident(g2,g3)
    c: Vertical(g3)
    c: Coincident(g3,g4)
    c: Coincident(g4,g0)
    c: Horizontal(g4)
    c: Distance(g-2,g0) = 5
    c: Distance(g-1,g2) = 5
    c: DistanceY(g-1,g0) = 35
    c: DistanceX(g-1,g1) = 35
    c: DistanceX(g1,g2) = 15
    c: Distance(g0,g4) = 15
FEATURE [Part::Extrusion] Extrude004
  Base = -> Sketch014
  Dir = (0,0,1)
  DirMode = 2
  FaceMakerClass = Part::FaceMakerBullseye
  FaceMakerMode = 3
  LengthFwd = 10
  LengthRev = 50
  Solid = true
  Symmetric = false
FEATURE [Part::Cut] Cut004
  Base = -> Box001
  Tool = -> Extrude004
FEATURE [Sketcher::SketchObject] Sketch021
  ArcFitTolerance = 1e-06
  AttachmentSupport = -> [Cut004]
  FullyConstrained = true
  MakeInternals = false
  MapMode = 5
  Placement = pos=(0,40,0) rot=(0,0.707107,0.707107;3.14159rad)
  sketch-geometry (4):
    g0: LineSegment StartX=-3 StartY=32 StartZ=0 EndX=-60 EndY=32 EndZ=0
    g1: LineSegment StartX=-60 StartY=32 StartZ=0 EndX=-60 EndY=3 EndZ=0
    g2: LineSegment StartX=-60 StartY=3 StartZ=0 EndX=-3 EndY=3 EndZ=0
    g3: LineSegment StartX=-3 StartY=3 StartZ=0 EndX=-3 EndY=32 EndZ=0
  constraints (12):
    c: Coincident(g0,g1)
    c: Coincident(g1,g2)
    c: Coincident(g2,g3)
    c: Coincident(g3,g0)
    c: Horizontal(g0)
    c: Horizontal(g2)
    c: Vertical(g1)
    c: Vertical(g3)
    c: Distance(g-1,g2) = 3
    c: Distance(g-1,g0) = 32
    c: Distance(g-2,g3) = 3
    c: Distance(g-2,g1) = 60
FEATURE [Part::Extrusion] Extrude005
  Base = -> Sketch021
  Dir = (0,1,-2e-16)
  DirMode = 2
  FaceMakerClass = Part::FaceMakerBullseye
  FaceMakerMode = 3
  LengthFwd = 5
  LengthRev = 37
  Solid = true
  Symmetric = false
FEATURE [Part::Cut] Cut005
  Base = -> Cut004
  Tool = -> Extrude005
FEATURE [Sketcher::SketchObject] Sketch022
  ArcFitTolerance = 1e-06
  AttachmentSupport = -> [Cut005]
  FullyConstrained = true
  MakeInternals = false
  MapMode = 5
  Placement = pos=(0,0,0) rot=(0.57735,-0.57735,-0.57735;2.0944rad)
  sketch-geometry (4):
    g0: ArcOfCircle CenterX=-12.5 CenterY=17.5 CenterZ=0 NormalX=0 NormalY=0 NormalZ=1 AngleXU=0 Radius=4.5 StartAngle=4.71239 EndAngle=7.85398
    g1: ArcOfCircle CenterX=-27.5 CenterY=17.5 CenterZ=0 NormalX=0 NormalY=0 NormalZ=1 AngleXU=0 Radius=4.5 StartAngle=1.5708 EndAngle=4.71239
    g2: LineSegment StartX=-12.5 StartY=13 StartZ=0 EndX=-27.5 EndY=13 EndZ=0
    g3: LineSegment StartX=-12.5 StartY=22 StartZ=0 EndX=-27.5 EndY=22 EndZ=0
  constraints (10):
    c: Tangent(g0,g2) = 1.5708
    c: Tangent(g0,g3) = -1.5708
    c: Tangent(g1,g2) = 1.5708
    c: Tangent(g1,g3) = -1.5708
    c: Equal(g0,g1)
    c: Horizontal(g2)
    c: DistanceX(g1,g0) = 15
    c: Distance(g2,g3) = 9
    c: Distance(g0,g-1) = 13
    c: Distance(g0,g-2) = 8
FEATURE [Part::Extrusion] Extrude006
  Base = -> Sketch022
  Dir = (-1,0,0)
  DirMode = 2
  FaceMakerClass = Part::FaceMakerBullseye
  FaceMakerMode = 3
  LengthFwd = 10
  LengthRev = 10
  Solid = true
  Symmetric = false
FEATURE [Part::Cut] Cut006
  Base = -> Cut005
  Tool = -> Extrude006
FEATURE [Sketcher::SketchObject] Sketch023
  ArcFitTolerance = 1e-06
  AttachmentSupport = -> [Cut006]
  FullyConstrained = true
  MakeInternals = false
  MapMode = 5
  Placement = pos=(0,0,0) rot=(1,0,0;1.5708rad)
  sketch-geometry (4):
    g0: ArcOfCircle CenterX=12.5 CenterY=17.5 CenterZ=0 NormalX=0 NormalY=0 NormalZ=1 AngleXU=0 Radius=4.5 StartAngle=1.5708 EndAngle=4.71239
    g1: ArcOfCircle CenterX=27.5 CenterY=17.5 CenterZ=0 NormalX=0 NormalY=0 NormalZ=1 AngleXU=0 Radius=4.5 StartAngle=4.71239 EndAngle=7.85398
    g2: LineSegment StartX=12.5 StartY=22 StartZ=0 EndX=27.5 EndY=22 EndZ=0
    g3: LineSegment StartX=12.5 StartY=13 StartZ=0 EndX=27.5 EndY=13 EndZ=0
  constraints (10):
    c: Tangent(g0,g2) = 1.5708
    c: Tangent(g0,g3) = -1.5708
    c: Tangent(g1,g2) = 1.5708
    c: Tangent(g1,g3) = -1.5708
    c: Equal(g0,g1)
    c: Horizontal(g2)
    c: Distance(g3,g2) = 9
    c: DistanceX(g0,g1) = 15
    c: Distance(g0,g-2) = 8
    c: Distance(g-1,g3) = 13
FEATURE [Part::Extrusion] Extrude007
  Base = -> Sketch023
  Dir = (0,-1,2e-16)
  DirMode = 2
  FaceMakerClass = Part::FaceMakerBullseye
  FaceMakerMode = 3
  LengthFwd = 10
  LengthRev = 10
  Solid = true
  Symmetric = false
FEATURE [Part::Cut] Cut007  label="corner gusset"
  Base = -> Cut006
  Tool = -> Extrude007
FEATURE [Sketcher::SketchObject] Sketch028
  ArcFitTolerance = 1e-06
  AttachmentSupport = -> [XY_Plane023]
  FullyConstrained = true
  MakeInternals = false
  MapMode = 5
  sketch-geometry (17):
    g0: LineSegment StartX=30 StartY=-35.75 StartZ=0 EndX=-30 EndY=-35.75 EndZ=0
    g1: LineSegment StartX=-30 StartY=-35.75 StartZ=0 EndX=-30 EndY=-3.25 EndZ=0
    g2: LineSegment StartX=-30 StartY=-3.25 StartZ=0 EndX=-18 EndY=-3.25 EndZ=0
    g3: LineSegment StartX=-18 StartY=-3.25 StartZ=0 EndX=-18 EndY=3.25 EndZ=0
    g4: LineSegment StartX=-18 StartY=3.25 StartZ=0 EndX=18 EndY=3.25 EndZ=0
    g5: LineSegment StartX=18 StartY=3.25 StartZ=0 EndX=18 EndY=-3.25 EndZ=0
    g6: LineSegment StartX=18 StartY=-3.25 StartZ=0 EndX=30 EndY=-3.25 EndZ=0
    g7: LineSegment StartX=30 StartY=-3.25 StartZ=0 EndX=30 EndY=-35.75 EndZ=0
    g8: Circle CenterX=-23 CenterY=-28.75 CenterZ=0 NormalX=0 NormalY=0 NormalZ=1 AngleXU=0 Radius=2.75
    g9: Circle CenterX=-23 CenterY=-13.75 CenterZ=0 NormalX=0 NormalY=0 NormalZ=1 AngleXU=0 Radius=2.75
    g10: Circle CenterX=23 CenterY=-13.75 CenterZ=0 NormalX=0 NormalY=0 NormalZ=1 AngleXU=0 Radius=2.75
    g11: Circle CenterX=23 CenterY=-28.75 CenterZ=0 NormalX=0 NormalY=0 NormalZ=1 AngleXU=0 Radius=2.75
    g12: LineSegment [constr] StartX=-23 StartY=-13.75 StartZ=0 EndX=23 EndY=-13.75 EndZ=0
    g13: LineSegment [constr] StartX=-23 StartY=-28.75 StartZ=0 EndX=23 EndY=-28.75 EndZ=0
    g14: LineSegment [constr] StartX=-23 StartY=-13.75 StartZ=0 EndX=-23 EndY=-28.75 EndZ=0
    g15: LineSegment [constr] StartX=23 StartY=-13.75 StartZ=0 EndX=23 EndY=-28.75 EndZ=0
    g16: Circle CenterX=-7e-16 CenterY=-13.75 CenterZ=0 NormalX=0 NormalY=0 NormalZ=1 AngleXU=0 Radius=5
  constraints (41):
    c: Horizontal(g0)
    c: Coincident(g1,g0)
    c: Coincident(g2,g1)
    c: Coincident(g3,g2)
    c: Vertical(g3)
    c: Coincident(g4,g3)
    c: Coincident(g5,g4)
    c: Coincident(g7,g0)
    c: Coincident(g6,g7)
    c: Coincident(g5,g6)
    c: Horizontal(g6)
    c: Vertical(g1)
    c: Vertical(g7)
    c: Tangent(g2,g6)
    c: Equal(g2,g6)
    c: DistanceX(g0,g0) = 60
    c: Symmetric(g3,g4,g-2)
    c: Symmetric(g5,g4,g-1)
    c: DistanceY(g7,g7) = 32.5
    c: Distance(g0,g4) = 39
    c: DistanceX(g2,g2) = 12
    c: Equal(g11,g10)
    c: Equal(g10,g9)
    c: Equal(g9,g8)
    c: Diameter(g8) = 5.5
    c: DistanceY(g8,g9) = 15
    c: Coincident(g12,g9)
    c: Coincident(g12,g10)
    c: Coincident(g13,g8)
    c: Coincident(g13,g11)
    c: Symmetric(g9,g10,g-2)
    c: Symmetric(g8,g11,g-2)
    c: Coincident(g14,g9)
    c: Coincident(g14,g8)
    c: Vertical(g14)
    c: Coincident(g15,g10)
    c: Coincident(g15,g11)
    c: Distance(g15,g14) = 46
    c: Symmetric(g12,g12,g16)
    c: Diameter(g16) = 10
    c: Distance(g0,g12) = 22
FEATURE [PartDesign::Pad] Pad018
  Direction = (0,0,1)
  Length = 20
  Length2 = 10
  Profile = -> Sketch028
  ReferenceAxis = -> Sketch028 [N_Axis]
  Refine = true
  Suppressed = false
  Type = 0
FEATURE [Sketcher::SketchObject] Sketch029
  ArcFitTolerance = 1e-06
  AttachmentSupport = -> [Pad018]
  FullyConstrained = true
  MakeInternals = false
  MapMode = 5
  Placement = pos=(-1.2316e-12,-3.25,0) rot=(0,0.707107,0.707107;3.14159rad)
  sketch-geometry (2):
    g0: Circle CenterX=-23 CenterY=10 CenterZ=0 NormalX=0 NormalY=0 NormalZ=1 AngleXU=0 Radius=3.3
    g1: Circle CenterX=23 CenterY=10 CenterZ=0 NormalX=0 NormalY=0 NormalZ=1 AngleXU=0 Radius=3.3
  constraints (5):
    c: Equal(g1,g0)
    c: Diameter(g0) = 6.6
    c: Symmetric(g0,g1,g-2)
    c: Distance(g0,g-1) = 10
    c: DistanceX(g0,g1) = 46
FEATURE [PartDesign::Pocket] Pocket002
  BaseFeature = -> Pad018
  Direction = (-3.79e-13,-1,2e-16)
  Length = 5
  Length2 = 5
  Profile = -> Sketch029
  ReferenceAxis = -> Sketch029 [N_Axis]
  Refine = true
  Suppressed = false
  Type = 1
FEATURE [PartDesign::Body] Body018  label="BF10"
  AllowCompound = false
  Group = -> [Sketch028,Pad018,Sketch029,Pocket002]
  Origin = -> Origin023
  Tip = -> Pocket002
FEATURE [Sketcher::SketchObject] Sketch030
  ArcFitTolerance = 1e-06
  AttachmentSupport = -> [XY_Plane024]
  FullyConstrained = true
  MakeInternals = false
  MapMode = 5
  sketch-geometry (18):
    g0: LineSegment StartX=0 StartY=0 StartZ=0 EndX=50 EndY=0 EndZ=0
    g1: LineSegment StartX=50 StartY=0 StartZ=0 EndX=50 EndY=73 EndZ=0
    g2: LineSegment StartX=50 StartY=73 StartZ=0 EndX=0 EndY=73 EndZ=0
    g3: LineSegment StartX=0 StartY=73 StartZ=0 EndX=0 EndY=0 EndZ=0
    g4: Circle CenterX=9 CenterY=54.5 CenterZ=0 NormalX=0 NormalY=0 NormalZ=1 AngleXU=0 Radius=3
    g5: Circle CenterX=9 CenterY=18.5 CenterZ=0 NormalX=0 NormalY=0 NormalZ=1 AngleXU=0 Radius=3
    g6: Circle CenterX=41 CenterY=54.5 CenterZ=0 NormalX=0 NormalY=0 NormalZ=1 AngleXU=0 Radius=3
    g7: Circle CenterX=41 CenterY=18.5 CenterZ=0 NormalX=0 NormalY=0 NormalZ=1 AngleXU=0 Radius=3
    g8: LineSegment [constr] StartX=9 StartY=54.5 StartZ=0 EndX=41 EndY=54.5 EndZ=0
    g9: LineSegment [constr] StartX=9 StartY=18.5 StartZ=0 EndX=41 EndY=18.5 EndZ=0
    g10: LineSegment [constr] StartX=9 StartY=54.5 StartZ=0 EndX=9 EndY=18.5 EndZ=0
    g11: LineSegment [constr] StartX=41 StartY=54.5 StartZ=0 EndX=41 EndY=18.5 EndZ=0
    g12: GeomPoint X=25 Y=54.5 Z=0
    g13: GeomPoint X=41 Y=36.5 Z=0
    g14: GeomPoint X=9 Y=36.5 Z=0
    g15: GeomPoint X=25 Y=18.5 Z=0
    g16: LineSegment [constr] StartX=9 StartY=36.5 StartZ=0 EndX=41 EndY=36.5 EndZ=0
    g17: LineSegment [constr] StartX=25 StartY=54.5 StartZ=0 EndX=25 EndY=18.5 EndZ=0
  constraints (37):
    c: Coincident(g0,g1)
    c: Coincident(g1,g2)
    c: Coincident(g2,g3)
    c: Coincident(g3,g0)
    c: Horizontal(g0)
    c: Horizontal(g2)
    c: Vertical(g1)
    c: Vertical(g3)
    c: Coincident(g0,g-1)
    c: DistanceY(g1,g1) = 73
    c: DistanceX(g2,g2) = 50
    c: Equal(g4,g6)
    c: Equal(g6,g7)
    c: Equal(g7,g5)
    c: Coincident(g8,g4)
    c: Coincident(g8,g6)
    c: Horizontal(g8)
    c: Coincident(g9,g5)
    c: Coincident(g9,g7)
    c: Coincident(g10,g4)
    c: Coincident(g10,g5)
    c: Vertical(g10)
    c: Coincident(g11,g6)
    c: Coincident(g11,g7)
    c: Diameter(g6) = 6
    c: DistanceY(g11,g11) = 36
    c: Distance(g8,g8) = 32
    c: Symmetric(g8,g8,g12)
    c: Symmetric(g11,g11,g13)
    c: Symmetric(g10,g10,g14)
    c: Symmetric(g9,g9,g15)
    c: Coincident(g16,g14)
    c: Coincident(g16,g13)
    c: Coincident(g17,g12)
    c: Coincident(g17,g15)
    c: Symmetric(g1,g0,g16)
    c: Symmetric(g2,g1,g17)
FEATURE [PartDesign::Pad] Pad019
  Direction = (0,0,1)
  Length = 30
  Length2 = 10
  Profile = -> Sketch030
  ReferenceAxis = -> Sketch030 [N_Axis]
  Refine = true
  Suppressed = false
  Type = 0
FEATURE [PartDesign::Body] Body019  label="hgr carriage spacer"
  AllowCompound = false
  Group = -> [Sketch030,Pad019]
  Origin = -> Origin024
  Tip = -> Pad019
FEATURE [Sketcher::SketchObject] Sketch031
  ArcFitTolerance = 1e-06
  AttachmentSupport = -> [XY_Plane025]
  FullyConstrained = true
  MakeInternals = false
  MapMode = 5
  sketch-geometry (8):
    g0: LineSegment StartX=0 StartY=0 StartZ=0 EndX=500 EndY=0 EndZ=0
    g1: LineSegment StartX=0 StartY=0 StartZ=0 EndX=0 EndY=4 EndZ=0
    g2: LineSegment StartX=0 StartY=4 StartZ=0 EndX=54 EndY=4 EndZ=0
    g3: LineSegment StartX=54 StartY=4 StartZ=0 EndX=54 EndY=6 EndZ=0
    g4: LineSegment StartX=500 StartY=0 StartZ=0 EndX=500 EndY=4 EndZ=0
    g5: LineSegment StartX=500 StartY=4 StartZ=0 EndX=489 EndY=4 EndZ=0
    g6: LineSegment StartX=489 StartY=4 StartZ=0 EndX=489 EndY=6 EndZ=0
    g7: LineSegment StartX=489 StartY=6 StartZ=0 EndX=54 EndY=6 EndZ=0
  constraints (23):
    c: Coincident(g0,g-1)
    c: Horizontal(g0)
    c: DistanceX(g0,g0) = 500
    c: Coincident(g1,g0)
    c: PointOnObject(g1,g-2)
    c: Distance(g1,g1) = 4
    c: Coincident(g2,g1)
    c: Horizontal(g2)
    c: DistanceX(g2,g2) = 54
    c: Coincident(g3,g2)
    c: Vertical(g3)
    c: Distance(g3,g3) = 2
    c: Coincident(g4,g0)
    c: Vertical(g4)
    c: DistanceY(g4,g4) = 4
    c: Coincident(g5,g4)
    c: Horizontal(g5)
    c: DistanceX(g5,g5) = 11
    c: Coincident(g6,g5)
    c: Vertical(g6)
    c: DistanceY(g6,g6) = 2
    c: Coincident(g7,g6)
    c: Coincident(g7,g3)
FEATURE [PartDesign::Revolution] Revolution
  Angle = 360
  Angle2 = 60
  Axis = (1,0,0)
  Base = (0,0,0)
  Profile = -> Sketch031
  ReferenceAxis = -> Sketch031 [H_Axis]
  Refine = true
  Suppressed = false
  Type = 0
FEATURE [PartDesign::Body] Body020  label="sfu1204x500mm"
  AllowCompound = false
  Group = -> [Sketch031,Revolution]
  Origin = -> Origin025
  Tip = -> Revolution
FEATURE [PartDesign::FeatureBase] Clone
  BaseFeature = -> Body001
  Suppressed = false
FEATURE [PartDesign::Body] Body021  label="4040@610 bottom left"
  AllowCompound = false
  Group = -> [Clone]
  Origin = -> Origin026
  Placement = pos=(0,0,0) rot=(1,0,0;1.5708rad)
  Tip = -> Clone
FEATURE [PartDesign::FeatureBase] Clone001
  BaseFeature = -> Body001
  Suppressed = false
FEATURE [PartDesign::Body] Body022  label="4040@610 bottom right"
  AllowCompound = false
  Group = -> [Clone001]
  Origin = -> Origin027
  Placement = pos=(-570,0,0) rot=(1,0,0;1.5708rad)
  Tip = -> Clone001
FEATURE [PartDesign::FeatureBase] Clone002
  BaseFeature = -> Body001
  Suppressed = false
FEATURE [PartDesign::Body] Body023  label="4040@610 top left"
  AllowCompound = false
  Group = -> [Clone002]
  Origin = -> Origin028
  Placement = pos=(0,0,510) rot=(1,0,0;1.5708rad)
  Tip = -> Clone002
FEATURE [PartDesign::FeatureBase] Clone003
  BaseFeature = -> Body001
  Suppressed = false
FEATURE [PartDesign::Body] Body024  label="4040@610 top right"
  AllowCompound = false
  Group = -> [Clone003]
  Origin = -> Origin029
  Placement = pos=(-570,0,510) rot=(1,0,0;1.5708rad)
  Tip = -> Clone003
FEATURE [PartDesign::FeatureBase] Clone004
  BaseFeature = -> Body002
  Suppressed = false
FEATURE [PartDesign::Body] Body025  label="4040@530 bottom front"
  AllowCompound = false
  Group = -> [Clone004]
  Origin = -> Origin030
  Placement = pos=(-550,-20,0) rot=(0,1,0;1.5708rad)
  Tip = -> Clone004
FEATURE [PartDesign::FeatureBase] Clone005
  BaseFeature = -> Body002
  Suppressed = false
FEATURE [PartDesign::Body] Body026  label="4040@530 top front"
  AllowCompound = false
  Group = -> [Clone005]
  Origin = -> Origin031
  Placement = pos=(-550,-20,510) rot=(0,1,0;1.5708rad)
  Tip = -> Clone005
FEATURE [PartDesign::FeatureBase] Clone006
  BaseFeature = -> Body002
  Suppressed = false
FEATURE [PartDesign::Body] Body027  label="4040@530 bottom back"
  AllowCompound = false
  Group = -> [Clone006]
  Origin = -> Origin032
  Placement = pos=(-550,-590,0) rot=(0,1,0;1.5708rad)
  Tip = -> Clone006
FEATURE [PartDesign::FeatureBase] Clone007
  BaseFeature = -> Body002
  Suppressed = false
FEATURE [PartDesign::Body] Body028  label="4040@530 top back"
  AllowCompound = false
  Group = -> [Clone007]
  Origin = -> Origin033
  Placement = pos=(-550,-590,510) rot=(0,1,0;1.5708rad)
  Tip = -> Clone007
FEATURE [PartDesign::FeatureBase] Clone008
  BaseFeature = -> Body003
  Suppressed = false
FEATURE [PartDesign::Body] Body029  label="4040@470 front left"
  AllowCompound = false
  Group = -> [Clone008]
  Origin = -> Origin034
  Placement = pos=(0,-20,20) rot=(0,0,1;0rad)
  Tip = -> Clone008
FEATURE [PartDesign::FeatureBase] Clone009
  BaseFeature = -> Body003
  Suppressed = false
FEATURE [PartDesign::Body] Body030  label="4040@470 front right"
  AllowCompound = false
  Group = -> [Clone009]
  Origin = -> Origin035
  Placement = pos=(-570,-20,20) rot=(0,0,1;0rad)
  Tip = -> Clone009
FEATURE [PartDesign::FeatureBase] Clone010
  BaseFeature = -> Body003
  Suppressed = false
FEATURE [PartDesign::Body] Body031  label="4040@470 back left"
  AllowCompound = false
  Group = -> [Clone010]
  Origin = -> Origin036
  Placement = pos=(0,-590,20) rot=(0,0,1;0rad)
  Tip = -> Clone010
FEATURE [PartDesign::FeatureBase] Clone011
  BaseFeature = -> Body003
  Suppressed = false
FEATURE [PartDesign::Body] Body032  label="4040@470 back right"
  AllowCompound = false
  Group = -> [Clone011]
  Origin = -> Origin037
  Placement = pos=(-570,-590,20) rot=(0,0,1;0rad)
  Tip = -> Clone011
FEATURE [PartDesign::FeatureBase] Clone012
  BaseFeature = -> Body004
  Suppressed = false
FEATURE [PartDesign::Body] Body033  label="8040@530 bottom left"
  AllowCompound = false
  Group = -> [Clone012]
  Origin = -> Origin038
  Placement = pos=(-245,-40,0) rot=(1,0,0;1.5708rad)
  Tip = -> Clone012
FEATURE [PartDesign::FeatureBase] Clone013
  BaseFeature = -> Body004
  Suppressed = false
FEATURE [PartDesign::Body] Body034  label="8040@530 bottom right"
  AllowCompound = false
  Group = -> [Clone013]
  Origin = -> Origin039
  Placement = pos=(-365,-40,0) rot=(1,0,0;1.5708rad)
  Tip = -> Clone013
FEATURE [PartDesign::FeatureBase] Clone014
  BaseFeature = -> Body006
  Placement = pos=(-290,0,0) rot=(0,0,1;0rad)
  Suppressed = false
FEATURE [PartDesign::Body] Body035  label="4040@100 bottom front"
  AllowCompound = false
  Group = -> [Clone014]
  Origin = -> Origin040
  Placement = pos=(5,-40,0) rot=(1,0,0;1.5708rad)
  Tip = -> Clone014
FEATURE [PartDesign::FeatureBase] Clone015
  BaseFeature = -> Body006
  Suppressed = false
FEATURE [PartDesign::Body] Body036  label="4040@100 bottom back"
  AllowCompound = false
  Group = -> [Clone015]
  Origin = -> Origin041
  Placement = pos=(-285,-470,0) rot=(1,0,0;1.5708rad)
  Tip = -> Clone015
FEATURE [PartDesign::FeatureBase] Clone016
  BaseFeature = -> Body005
  Suppressed = false
FEATURE [PartDesign::Body] Body037  label="8040@470 back left"
  AllowCompound = false
  Group = -> [Clone016]
  Origin = -> Origin042
  Placement = pos=(0,-481.84,20) rot=(0,0,1;1.5708rad)
  Tip = -> Clone016
  expr: .Placement.Base.y = -Group001.Base_Z_gantry_depth - 40 mm
FEATURE [PartDesign::FeatureBase] Clone017
  BaseFeature = -> Body005
  Suppressed = false
FEATURE [PartDesign::Body] Body038  label="8040@470 front left"
  AllowCompound = false
  Group = -> [Clone017]
  Origin = -> Origin043
  Placement = pos=(0,-401.84,20) rot=(0,0,1;1.5708rad)
  Tip = -> Clone017
  expr: .Placement.Base.y = -Group001.Base_Z_gantry_depth + 40 mm
FEATURE [PartDesign::FeatureBase] Clone018
  BaseFeature = -> Body005
  Suppressed = false
FEATURE [PartDesign::Body] Body039  label="8040@470 back right"
  AllowCompound = false
  Group = -> [Clone018]
  Origin = -> Origin044
  Placement = pos=(-570,-481.84,20) rot=(0,0,1;1.5708rad)
  Tip = -> Clone018
  expr: .Placement.Base.y = -Group001.Base_Z_gantry_depth - 40 mm
FEATURE [PartDesign::FeatureBase] Clone019
  BaseFeature = -> Body005
  Suppressed = false
FEATURE [PartDesign::Body] Body040  label="8040@470 front right"
  AllowCompound = false
  Group = -> [Clone019]
  Origin = -> Origin045
  Placement = pos=(-570,-401.84,20) rot=(0,0,1;1.5708rad)
  Tip = -> Clone019
  expr: .Placement.Base.y = -Group001.Base_Z_gantry_depth + 40 mm
FEATURE [PartDesign::FeatureBase] Clone020
  BaseFeature = -> Body004
  Suppressed = false
FEATURE [PartDesign::Body] Body041  label="8040@530 top middle"
  AllowCompound = false
  Group = -> [Clone020]
  Origin = -> Origin046
  Placement = pos=(-20,-441.84,360) rot=(0,1,0;-1.5708rad)
  Tip = -> Clone020
  expr: .Placement.Base.y = -Group001.Base_Z_gantry_depth
FEATURE [PartDesign::FeatureBase] Clone021
  BaseFeature = -> Body004
  Suppressed = false
FEATURE [PartDesign::Body] Body042  label="8040@530 bottom middle"
  AllowCompound = false
  Group = -> [Clone021]
  Origin = -> Origin047
  Placement = pos=(-20,-441.84,280) rot=(0,1,0;-1.5708rad)
  Tip = -> Clone021
  expr: .Placement.Base.y = -Group001.Base_Z_gantry_depth
FEATURE [App::DocumentObjectGroup] Group001  label="Parameters"
  Base_Z_gantry_depth = 441.84
  Base_x_coord = 0
  Base_y_coord = 0
  Base_z_coord = 0
FEATURE [Sketcher::SketchObject] Sketch
  ArcFitTolerance = 1e-06
  AttachmentSupport = -> [XZ_Plane048]
  FullyConstrained = true
  MakeInternals = false
  MapMode = 5
  Placement = pos=(0,0,0) rot=(1,0,0;1.5708rad)
  sketch-geometry (22):
    g0: LineSegment StartX=-101.6 StartY=152.4 StartZ=0 EndX=-101.6 EndY=-152.4 EndZ=0
    g1: LineSegment StartX=-101.6 StartY=-152.4 StartZ=0 EndX=101.6 EndY=-152.4 EndZ=0
    g2: LineSegment StartX=101.6 StartY=-152.4 StartZ=0 EndX=101.6 EndY=152.4 EndZ=0
    g3: LineSegment StartX=101.6 StartY=152.4 StartZ=0 EndX=-101.6 EndY=152.4 EndZ=0
    g4: LineSegment [constr] StartX=-40 StartY=60 StartZ=0 EndX=-40 EndY=-60 EndZ=0
    g5: LineSegment [constr] StartX=-40 StartY=-60 StartZ=0 EndX=40 EndY=-60 EndZ=0
    g6: LineSegment [constr] StartX=40 StartY=-60 StartZ=0 EndX=40 EndY=60 EndZ=0
    g7: LineSegment [constr] StartX=40 StartY=60 StartZ=0 EndX=-40 EndY=60 EndZ=0
    g8: LineSegment [constr] StartX=-40 StartY=20 StartZ=0 EndX=40 EndY=20 EndZ=0
    g9: LineSegment [constr] StartX=-40 StartY=-20 StartZ=0 EndX=40 EndY=-20 EndZ=0
    g10: Circle CenterX=-40 CenterY=60 CenterZ=0 NormalX=0 NormalY=0 NormalZ=1 AngleXU=0 Radius=4.5
    g11: Circle CenterX=40 CenterY=60 CenterZ=0 NormalX=0 NormalY=0 NormalZ=1 AngleXU=0 Radius=4.5
    g12: Circle CenterX=40 CenterY=20 CenterZ=0 NormalX=0 NormalY=0 NormalZ=1 AngleXU=0 Radius=4.5
    g13: Circle CenterX=40 CenterY=-20 CenterZ=0 NormalX=0 NormalY=0 NormalZ=1 AngleXU=0 Radius=4.5
    g14: Circle CenterX=40 CenterY=-60 CenterZ=0 NormalX=0 NormalY=0 NormalZ=1 AngleXU=0 Radius=4.5
    g15: Circle CenterX=-40 CenterY=-60 CenterZ=0 NormalX=0 NormalY=0 NormalZ=1 AngleXU=0 Radius=4.5
    g16: Circle CenterX=-40 CenterY=-20 CenterZ=0 NormalX=0 NormalY=0 NormalZ=1 AngleXU=0 Radius=4.5
    g17: Circle CenterX=-40 CenterY=20 CenterZ=0 NormalX=0 NormalY=0 NormalZ=1 AngleXU=0 Radius=4.5
    g18: Circle CenterX=0 CenterY=60 CenterZ=0 NormalX=0 NormalY=0 NormalZ=1 AngleXU=0 Radius=4.5
    g19: Circle CenterX=0 CenterY=20 CenterZ=0 NormalX=0 NormalY=0 NormalZ=1 AngleXU=0 Radius=4.5
    g20: Circle CenterX=0 CenterY=-20 CenterZ=0 NormalX=0 NormalY=0 NormalZ=1 AngleXU=0 Radius=4.5
    g21: Circle CenterX=0 CenterY=-60 CenterZ=0 NormalX=0 NormalY=0 NormalZ=1 AngleXU=0 Radius=4.5
  constraints (55):
    c: Coincident(g0,g1)
    c: Coincident(g1,g2)
    c: Coincident(g2,g3)
    c: Coincident(g3,g0)
    c: Vertical(g2)
    c: Horizontal(g1)
    c: Symmetric(g0,g0,g-1)
    c: Symmetric(g0,g2,g-2)
    c: DistanceY(g0,g0) = 304.8
    c: DistanceX(g3,g3) = 203.2
    c: Coincident(g4,g5)
    c: Coincident(g5,g6)
    c: Coincident(g6,g7)
    c: Coincident(g7,g4)
    c: Vertical(g6)
    c: Horizontal(g5)
    c: Symmetric(g4,g4,g-1)
    c: Symmetric(g4,g6,g-2)
    c: PointOnObject(g8,g4)
    c: PointOnObject(g8,g6)
    c: Horizontal(g8)
    c: PointOnObject(g9,g4)
    c: PointOnObject(g9,g6)
    c: Horizontal(g9)
    c: Distance(g8,g7) = 40
    c: Distance(g9,g8) = 40
    c: Distance(g5,g9) = 40
    c: DistanceX(g7,g7) = 80
    c: Coincident(g10,g4)
    c: Coincident(g11,g6)
    c: Coincident(g12,g8)
    c: Coincident(g13,g9)
    c: Coincident(g14,g5)
    c: Coincident(g15,g4)
    c: Coincident(g16,g9)
    c: Coincident(g17,g8)
    c: Symmetric(g7,g7,g18)
    c: PointOnObject(g19,g8)
    c: PointOnObject(g20,g9)
    c: PointOnObject(g21,g5)
    c: Equal(g15,g21)
    c: Equal(g21,g20)
    c: Equal(g20,g16)
    c: Equal(g16,g17)
    c: Equal(g17,g19)
    c: Equal(g19,g18)
    c: Equal(g18,g10)
    c: Equal(g10,g12)
    c: Equal(g12,g11)
    c: Equal(g11,g13)
    c: Equal(g13,g14)
    c: Diameter(g11) = 9
    c: PointOnObject(g19,g-2)
    c: PointOnObject(g20,g-2)
    c: PointOnObject(g21,g-2)
FEATURE [PartDesign::Pad] Pad020
  Direction = (0,-1,2e-16)
  Length = 12.7
  Length2 = 10
  Placement = pos=(0,0,0) rot=(1,0,0;1.5708rad)
  Profile = -> Sketch
  ReferenceAxis = -> Sketch [N_Axis]
  Refine = true
  Suppressed = false
  Type = 0
FEATURE [PartDesign::Body] Body043  label="Z-axis mount"
  AllowCompound = false
  Group = -> [Sketch,Pad020]
  Origin = -> Origin048
  Tip = -> Pad020
FEATURE [Sketcher::SketchObject] Sketch032
  ArcFitTolerance = 1e-06
  AttachmentSupport = -> [XY_Plane049]
  FullyConstrained = true
  MakeInternals = false
  MapMode = 5
  sketch-geometry (72):
    g0: LineSegment StartX=-152.4 StartY=228.6 StartZ=0 EndX=-152.4 EndY=-228.6 EndZ=0
    g1: LineSegment StartX=-152.4 StartY=-228.6 StartZ=0 EndX=152.4 EndY=-228.6 EndZ=0
    g2: LineSegment StartX=152.4 StartY=-228.6 StartZ=0 EndX=152.4 EndY=228.6 EndZ=0
    g3: LineSegment StartX=152.4 StartY=228.6 StartZ=0 EndX=-152.4 EndY=228.6 EndZ=0
    g4: Circle CenterX=-118 CenterY=96 CenterZ=0 NormalX=0 NormalY=0 NormalZ=1 AngleXU=0 Radius=2.5
    g5: Circle CenterX=-82 CenterY=96 CenterZ=0 NormalX=0 NormalY=0 NormalZ=1 AngleXU=0 Radius=2.5
    g6: Circle CenterX=-118 CenterY=64 CenterZ=0 NormalX=0 NormalY=0 NormalZ=1 AngleXU=0 Radius=2.5
    g7: Circle CenterX=-82 CenterY=64 CenterZ=0 NormalX=0 NormalY=0 NormalZ=1 AngleXU=0 Radius=2.5
    g8: Circle CenterX=-118 CenterY=-64 CenterZ=0 NormalX=0 NormalY=0 NormalZ=1 AngleXU=0 Radius=2.5
    g9: Circle CenterX=-82 CenterY=-64 CenterZ=0 NormalX=0 NormalY=0 NormalZ=1 AngleXU=0 Radius=2.5
    g10: Circle CenterX=-118 CenterY=-96 CenterZ=0 NormalX=0 NormalY=0 NormalZ=1 AngleXU=0 Radius=2.5
    g11: Circle CenterX=-82 CenterY=-96 CenterZ=0 NormalX=0 NormalY=0 NormalZ=1 AngleXU=0 Radius=2.5
    g12: Circle CenterX=82 CenterY=96 CenterZ=0 NormalX=0 NormalY=0 NormalZ=1 AngleXU=0 Radius=2.5
    g13: Circle CenterX=118 CenterY=96 CenterZ=0 NormalX=0 NormalY=0 NormalZ=1 AngleXU=0 Radius=2.5
    g14: Circle CenterX=82 CenterY=64 CenterZ=0 NormalX=0 NormalY=0 NormalZ=1 AngleXU=0 Radius=2.5
    g15: Circle CenterX=118 CenterY=64 CenterZ=0 NormalX=0 NormalY=0 NormalZ=1 AngleXU=0 Radius=2.5
    g16: Circle CenterX=82 CenterY=-64 CenterZ=0 NormalX=0 NormalY=0 NormalZ=1 AngleXU=0 Radius=2.5
    g17: Circle CenterX=118 CenterY=-64 CenterZ=0 NormalX=0 NormalY=0 NormalZ=1 AngleXU=0 Radius=2.5
    g18: Circle CenterX=82 CenterY=-96 CenterZ=0 NormalX=0 NormalY=0 NormalZ=1 AngleXU=0 Radius=2.5
    g19: Circle CenterX=118 CenterY=-96 CenterZ=0 NormalX=0 NormalY=0 NormalZ=1 AngleXU=0 Radius=2.5
    g20: LineSegment [constr] StartX=-118 StartY=96 StartZ=0 EndX=118 EndY=96 EndZ=0
    g21: LineSegment [constr] StartX=118 StartY=96 StartZ=0 EndX=118 EndY=-96 EndZ=0
    g22: LineSegment [constr] StartX=118 StartY=-96 StartZ=0 EndX=-118 EndY=-96 EndZ=0
    g23: LineSegment [constr] StartX=-118 StartY=-96 StartZ=0 EndX=-118 EndY=96 EndZ=0
    g24: LineSegment [constr] StartX=-118 StartY=64 StartZ=0 EndX=118 EndY=64 EndZ=0
    g25: LineSegment [constr] StartX=-118 StartY=-64 StartZ=0 EndX=118 EndY=-64 EndZ=0
    g26: LineSegment [constr] StartX=82 StartY=96 StartZ=0 EndX=82 EndY=-96 EndZ=0
    g27: LineSegment [constr] StartX=-82 StartY=-96 StartZ=0 EndX=-82 EndY=96 EndZ=0
    g28: LineSegment [constr] StartX=-12 StartY=-17.5 StartZ=0 EndX=12 EndY=-17.5 EndZ=0
    g29: LineSegment [constr] StartX=12 StartY=-17.5 StartZ=0 EndX=12 EndY=17.5 EndZ=0
    g30: LineSegment [constr] StartX=12 StartY=17.5 StartZ=0 EndX=-12 EndY=17.5 EndZ=0
    g31: LineSegment [constr] StartX=-12 StartY=17.5 StartZ=0 EndX=-12 EndY=-17.5 EndZ=0
    g32: Circle CenterX=-12 CenterY=17.5 CenterZ=0 NormalX=0 NormalY=0 NormalZ=1 AngleXU=0 Radius=2.5
    g33: Circle CenterX=12 CenterY=17.5 CenterZ=0 NormalX=0 NormalY=0 NormalZ=1 AngleXU=0 Radius=2.5
    g34: Circle CenterX=12 CenterY=-17.5 CenterZ=0 NormalX=0 NormalY=0 NormalZ=1 AngleXU=0 Radius=2.5
    g35: Circle CenterX=-12 CenterY=-17.5 CenterZ=0 NormalX=0 NormalY=0 NormalZ=1 AngleXU=0 Radius=2.5
    g36: LineSegment [constr] StartX=100 StartY=-200 StartZ=0 EndX=100 EndY=200 EndZ=0
    g37: LineSegment [constr] StartX=-100 StartY=-200 StartZ=0 EndX=-100 EndY=200 EndZ=0
    g38: Circle CenterX=100 CenterY=180 CenterZ=0 NormalX=0 NormalY=0 NormalZ=1 AngleXU=0 Radius=2
    g39: Circle CenterX=100 CenterY=120 CenterZ=0 NormalX=0 NormalY=0 NormalZ=1 AngleXU=0 Radius=2
    g40: Circle CenterX=100 CenterY=-120 CenterZ=0 NormalX=0 NormalY=0 NormalZ=1 AngleXU=0 Radius=2
    g41: Circle CenterX=100 CenterY=-60 CenterZ=0 NormalX=0 NormalY=0 NormalZ=1 AngleXU=0 Radius=2
    g42: Circle CenterX=100 CenterY=60 CenterZ=0 NormalX=0 NormalY=0 NormalZ=1 AngleXU=0 Radius=2
    g43: Circle CenterX=100 CenterY=-9e-16 CenterZ=0 NormalX=0 NormalY=0 NormalZ=1 AngleXU=0 Radius=2
    g44: Circle CenterX=100 CenterY=-180 CenterZ=0 NormalX=0 NormalY=0 NormalZ=1 AngleXU=0 Radius=2
    g45: Circle CenterX=-100 CenterY=-180 CenterZ=0 NormalX=0 NormalY=0 NormalZ=1 AngleXU=0 Radius=2
    g46: Circle CenterX=-100 CenterY=-120 CenterZ=0 NormalX=0 NormalY=0 NormalZ=1 AngleXU=0 Radius=2
    g47: Circle CenterX=-100 CenterY=-60 CenterZ=0 NormalX=0 NormalY=0 NormalZ=1 AngleXU=0 Radius=2
    g48: Circle CenterX=-100 CenterY=-9e-16 CenterZ=0 NormalX=0 NormalY=0 NormalZ=1 AngleXU=0 Radius=2
    g49: Circle CenterX=-100 CenterY=60 CenterZ=0 NormalX=0 NormalY=0 NormalZ=1 AngleXU=0 Radius=2
    g50: Circle CenterX=-100 CenterY=120 CenterZ=0 NormalX=0 NormalY=0 NormalZ=1 AngleXU=0 Radius=2
    g51: Circle CenterX=-100 CenterY=180 CenterZ=0 NormalX=0 NormalY=0 NormalZ=1 AngleXU=0 Radius=2
    g52: Circle CenterX=-82 CenterY=96 CenterZ=0 NormalX=0 NormalY=0 NormalZ=1 AngleXU=0 Radius=4.5
    g53: Circle CenterX=-118 CenterY=96 CenterZ=0 NormalX=0 NormalY=0 NormalZ=1 AngleXU=0 Radius=4.5
    g54: Circle CenterX=-118 CenterY=64 CenterZ=0 NormalX=0 NormalY=0 NormalZ=1 AngleXU=0 Radius=4.5
    g55: Circle CenterX=-82 CenterY=64 CenterZ=0 NormalX=0 NormalY=0 NormalZ=1 AngleXU=0 Radius=4.5
    g56: Circle CenterX=-118 CenterY=-64 CenterZ=0 NormalX=0 NormalY=0 NormalZ=1 AngleXU=0 Radius=4.5
    g57: Circle CenterX=-82 CenterY=-64 CenterZ=0 NormalX=0 NormalY=0 NormalZ=1 AngleXU=0 Radius=4.5
    g58: Circle CenterX=-118 CenterY=-96 CenterZ=0 NormalX=0 NormalY=0 NormalZ=1 AngleXU=0 Radius=4.5
    g59: Circle CenterX=-82 CenterY=-96 CenterZ=0 NormalX=0 NormalY=0 NormalZ=1 AngleXU=0 Radius=4.5
    g60: Circle CenterX=82 CenterY=-96 CenterZ=0 NormalX=0 NormalY=0 NormalZ=1 AngleXU=0 Radius=4.5
    g61: Circle CenterX=82 CenterY=-64 CenterZ=0 NormalX=0 NormalY=0 NormalZ=1 AngleXU=0 Radius=4.5
    g62: Circle CenterX=118 CenterY=-96 CenterZ=0 NormalX=0 NormalY=0 NormalZ=1 AngleXU=0 Radius=4.5
    g63: Circle CenterX=118 CenterY=-64 CenterZ=0 NormalX=0 NormalY=0 NormalZ=1 AngleXU=0 Radius=4.5
    g64: Circle CenterX=118 CenterY=64 CenterZ=0 NormalX=0 NormalY=0 NormalZ=1 AngleXU=0 Radius=4.5
    g65: Circle CenterX=118 CenterY=96 CenterZ=0 NormalX=0 NormalY=0 NormalZ=1 AngleXU=0 Radius=4.5
    g66: Circle CenterX=82 CenterY=96 CenterZ=0 NormalX=0 NormalY=0 NormalZ=1 AngleXU=0 Radius=4.5
    g67: Circle CenterX=82 CenterY=64 CenterZ=0 NormalX=0 NormalY=0 NormalZ=1 AngleXU=0 Radius=4.5
    g68: Circle CenterX=12 CenterY=17.5 CenterZ=0 NormalX=0 NormalY=0 NormalZ=1 AngleXU=0 Radius=4.5
    g69: Circle CenterX=-12 CenterY=17.5 CenterZ=0 NormalX=0 NormalY=0 NormalZ=1 AngleXU=0 Radius=4.5
    g70: Circle CenterX=-12 CenterY=-17.5 CenterZ=0 NormalX=0 NormalY=0 NormalZ=1 AngleXU=0 Radius=4.5
    g71: Circle CenterX=12 CenterY=-17.5 CenterZ=0 NormalX=0 NormalY=0 NormalZ=1 AngleXU=0 Radius=4.5
  constraints (176):
    c: Coincident(g0,g1)
    c: Coincident(g1,g2)
    c: Coincident(g2,g3)
    c: Coincident(g3,g0)
    c: Vertical(g2)
    c: Horizontal(g1)
    c: Equal(g17,g16)
    c: Equal(g16,g18)
    c: Equal(g18,g19)
    c: Equal(g19,g14)
    c: Equal(g14,g15)
    c: Equal(g15,g13)
    c: Equal(g13,g12)
    c: Equal(g12,g5)
    c: Equal(g5,g4)
    c: Equal(g4,g6)
    c: Equal(g6,g7)
    c: Equal(g7,g8)
    c: Equal(g8,g9)
    c: Equal(g9,g11)
    c: Equal(g11,g10)
    c: Diameter(g4) = 5
    c: Coincident(g20,g4)
    c: Coincident(g20,g13)
    c: Coincident(g21,g13)
    c: Coincident(g21,g19)
    c: Coincident(g22,g19)
    c: Coincident(g22,g10)
    c: Coincident(g23,g10)
    c: Coincident(g23,g4)
    c: PointOnObject(g6,g23)
    c: PointOnObject(g8,g23)
    c: PointOnObject(g11,g22)
    c: PointOnObject(g18,g22)
    c: PointOnObject(g17,g21)
    c: PointOnObject(g15,g21)
    c: PointOnObject(g12,g20)
    c: PointOnObject(g5,g20)
    c: Vertical(g21)
    c: Coincident(g24,g6)
    c: Horizontal(g24)
    c: Coincident(g25,g8)
    c: Coincident(g25,g17)
    c: Coincident(g26,g12)
    c: Coincident(g26,g18)
    c: Vertical(g26)
    c: Coincident(g27,g11)
    c: Coincident(g27,g5)
    c: Vertical(g27)
    c: Horizontal(g25)
    c: PointOnObject(g9,g25)
    c: PointOnObject(g9,g27)
    c: PointOnObject(g7,g27)
    c: PointOnObject(g14,g24)
    c: PointOnObject(g14,g26)
    c: Coincident(g15,g24)
    c: PointOnObject(g16,g26)
    c: PointOnObject(g16,g25)
    c: Distance(g24,g20) = 32
    c: Distance(g25,g22) = 32
    c: Distance(g27,g23) = 36
    c: Distance(g21,g26) = 36
    c: Distance(g1,g3) = 457.2
    c: Distance(g2,g0) = 304.8
    c: Symmetric(g5,g12,g-2)
    c: Symmetric(g10,g4,g-1)
    c: Symmetric(g0,g0,g-1)
    c: Symmetric(g0,g2,g-2)
    c: DistanceY(g9,g5) = 160
    c: Distance(g26,g23) = 200
    c: Coincident(g28,g29)
    c: Coincident(g29,g30)
    c: Coincident(g30,g31)
    c: Coincident(g31,g28)
    c: Horizontal(g28)
    c: Vertical(g31)
    c: DistanceY(g29,g29) = 35
    c: DistanceX(g30,g30) = 24
    c: Symmetric(g30,g29,g-2)
    c: Symmetric(g29,g28,g-1)
    c: Coincident(g32,g30)
    c: Coincident(g33,g29)
    c: Coincident(g34,g28)
    c: Coincident(g35,g28)
    c: Equal(g35,g32)
    c: Equal(g32,g33)
    c: Equal(g33,g34)
    c: Diameter(g32) = 5
    c: Symmetric(g6,g7,g37)
    c: Symmetric(g18,g19,g36)
    c: DistanceY(g37,g37) = 400
    c: DistanceY(g36,g36) = 400
    c: Symmetric(g36,g36,g-1)
    c: Symmetric(g37,g37,g-1)
    c: PointOnObject(g38,g36)
    c: PointOnObject(g39,g36)
    c: PointOnObject(g40,g36)
    c: PointOnObject(g41,g36)
    c: PointOnObject(g42,g36)
    c: PointOnObject(g43,g36)
    c: DistanceY(g39,g38) = 60
    c: DistanceY(g38,g36) = 20
    c: DistanceY(g42,g39) = 60
    c: DistanceY(g43,g42) = 60
    c: DistanceY(g41,g43) = 60
    c: DistanceY(g40,g41) = 60
    c: PointOnObject(g44,g36)
    c: DistanceY(g44,g40) = 60
    c: Equal(g38,g39)
    c: Equal(g39,g42)
    c: Equal(g42,g43)
    c: Equal(g43,g41)
    c: Equal(g41,g40)
    c: Equal(g40,g44)
    c: Diameter(g44) = 4
    c: PointOnObject(g45,g37)
    c: PointOnObject(g46,g37)
    c: PointOnObject(g47,g37)
    c: PointOnObject(g48,g37)
    c: PointOnObject(g49,g37)
    c: PointOnObject(g50,g37)
    c: PointOnObject(g51,g37)
    c: Equal(g45,g46)
    c: Equal(g47,g48)
    c: Equal(g48,g49)
    c: Equal(g49,g50)
    c: Equal(g50,g51)
    c: Equal(g51,g38)
    c: Horizontal(g51,g38)
    c: Horizontal(g50,g39)
    c: Horizontal(g49,g42)
    c: Horizontal(g48,g43)
    c: Horizontal(g47,g41)
    c: Horizontal(g46,g40)
    c: Horizontal(g45,g44)
    c: Equal(g46,g47)
    c: Coincident(g52,g5)
    c: Coincident(g53,g4)
    c: Coincident(g54,g6)
    c: Coincident(g55,g7)
    c: Coincident(g56,g8)
    c: Coincident(g57,g9)
    c: Coincident(g58,g10)
    c: Coincident(g59,g11)
    c: Coincident(g60,g18)
    c: Coincident(g61,g16)
    c: Coincident(g62,g19)
    c: Coincident(g63,g17)
    c: Coincident(g64,g15)
    c: Coincident(g65,g13)
    c: Coincident(g66,g12)
    c: Coincident(g67,g14)
    c: Coincident(g68,g29)
    c: Coincident(g69,g30)
    c: Coincident(g70,g28)
    c: Coincident(g71,g28)
    c: Equal(g53,g52)
    c: Equal(g52,g54)
    c: Equal(g54,g55)
    c: Equal(g55,g56)
    c: Equal(g56,g57)
    c: Equal(g57,g58)
    c: Equal(g58,g59)
    c: Equal(g59,g70)
    c: Equal(g70,g69)
    c: Equal(g69,g68)
    c: Equal(g68,g71)
    c: Equal(g71,g61)
    c: Equal(g61,g63)
    c: Equal(g63,g60)
    c: Equal(g60,g62)
    c: Equal(g62,g67)
    c: Equal(g67,g64)
    c: Equal(g64,g65)
    c: Equal(g65,g66)
    c: Diameter(g52) = 9
FEATURE [PartDesign::FeatureBase] Clone023
  BaseFeature = -> Body
  Suppressed = false
FEATURE [PartDesign::Body] Body046  label="hgr20x500mm left"
  AllowCompound = false
  Group = -> [Clone023]
  Origin = -> Origin051
  Placement = pos=(-205,-55,20) rot=(1,0,0;1.5708rad)
  Tip = -> Clone023
FEATURE [PartDesign::FeatureBase] Clone024
  BaseFeature = -> Body
  Suppressed = false
FEATURE [PartDesign::Body] Body047  label="hgr20x500mm right"
  AllowCompound = false
  Group = -> [Clone024]
  Origin = -> Origin052
  Placement = pos=(-365,-55,20) rot=(1,0,0;1.5708rad)
  Tip = -> Clone024
FEATURE [PartDesign::FeatureBase] Clone025
  BaseFeature = -> Body007
  Suppressed = false
FEATURE [PartDesign::Body] Body048  label="hgr20 carriage back left"
  AllowCompound = false
  Group = -> [Clone025]
  Origin = -> Origin053
  Placement = pos=(-205,-368.5,24.6) rot=(1,0,0;1.5708rad)
  Tip = -> Clone025
  expr: .Placement.Base.y = -368.5 mm + Group001.Base_x_coord
FEATURE [PartDesign::FeatureBase] Clone026
  BaseFeature = -> Body007
  Suppressed = false
FEATURE [PartDesign::Body] Body049  label="hgr20 carriage front left"
  AllowCompound = false
  Group = -> [Clone026]
  Origin = -> Origin054
  Placement = pos=(-205,-168.5,24.6) rot=(1,0,0;1.5708rad)
  Tip = -> Clone026
  expr: .Placement.Base.y = -168.5 mm + Group001.Base_x_coord
FEATURE [PartDesign::FeatureBase] Clone027
  BaseFeature = -> Body007
  Suppressed = false
FEATURE [PartDesign::Body] Body050  label="hgr20 carriage back right"
  AllowCompound = false
  Group = -> [Clone027]
  Origin = -> Origin055
  Placement = pos=(-365,-368.5,24.6) rot=(1,0,0;1.5708rad)
  Tip = -> Clone027
  expr: .Placement.Base.y = -368.5 mm + Group001.Base_x_coord
FEATURE [PartDesign::FeatureBase] Clone028
  BaseFeature = -> Body007
  Suppressed = false
FEATURE [PartDesign::Body] Body051  label="hgr20 carriage front right"
  AllowCompound = false
  Group = -> [Clone028]
  Origin = -> Origin056
  Placement = pos=(-365,-168.5,24.6) rot=(1,0,0;1.5708rad)
  Tip = -> Clone028
  expr: .Placement.Base.y = -168.5 mm + Group001.Base_x_coord
FEATURE [PartDesign::FeatureBase] Clone029
  BaseFeature = -> Body019
  Suppressed = false
FEATURE [PartDesign::Body] Body052  label="hgr20 carriage spacer back left"
  AllowCompound = false
  Group = -> [Clone029]
  Origin = -> Origin057
  Placement = pos=(-230,-441.5,50) rot=(0,0,1;0rad)
  Tip = -> Clone029
  expr: .Placement.Base.y = -441.5 mm + Group001.Base_x_coord
FEATURE [PartDesign::FeatureBase] Clone030
  BaseFeature = -> Body019
  Suppressed = false
FEATURE [PartDesign::Body] Body053  label="hgr20 carriage spacer front left"
  AllowCompound = false
  Group = -> [Clone030]
  Origin = -> Origin058
  Placement = pos=(-230,-241.5,50) rot=(0,0,1;0rad)
  Tip = -> Clone030
  expr: .Placement.Base.y = -241.5 mm + Group001.Base_x_coord
FEATURE [PartDesign::FeatureBase] Clone031
  BaseFeature = -> Body019
  Suppressed = false
FEATURE [PartDesign::Body] Body054  label="hgr20 carriage spacer back right"
  AllowCompound = false
  Group = -> [Clone031]
  Origin = -> Origin059
  Placement = pos=(-390,-441.5,50) rot=(0,0,1;0rad)
  Tip = -> Clone031
  expr: .Placement.Base.y = -441.5 mm + Group001.Base_x_coord
FEATURE [PartDesign::FeatureBase] Clone032
  BaseFeature = -> Body019
  Suppressed = false
FEATURE [PartDesign::Body] Body055  label="hgr20 carriage spacer front right"
  AllowCompound = false
  Group = -> [Clone032]
  Origin = -> Origin060
  Placement = pos=(-390,-241.5,50) rot=(0,0,1;0rad)
  Tip = -> Clone032
  expr: .Placement.Base.y = -241.5 mm + Group001.Base_x_coord
FEATURE [Sketcher::SketchObject] Sketch035
  ArcFitTolerance = 1e-06
  AttachmentSupport = -> [XY_Plane064]
  FullyConstrained = false
  MakeInternals = false
  MapMode = 5
  sketch-geometry (12):
    g0: LineSegment StartX=-46.7614 StartY=0 StartZ=0 EndX=46.7614 EndY=0 EndZ=0
    g1: LineSegment StartX=46.7614 StartY=0 StartZ=0 EndX=46.7614 EndY=-10.9474 EndZ=0
    g2: LineSegment StartX=46.7614 StartY=-10.9474 StartZ=0 EndX=34.925 EndY=-10.9474 EndZ=0
    g3: LineSegment StartX=34.925 StartY=-10.9474 StartZ=0 EndX=34.925 EndY=-75.565 EndZ=0
    g4: LineSegment StartX=34.925 StartY=-75.565 StartZ=0 EndX=-34.925 EndY=-75.565 EndZ=0
    g5: LineSegment StartX=-34.925 StartY=-75.565 StartZ=0 EndX=-34.925 EndY=-10.9474 EndZ=0
    g6: LineSegment StartX=-34.925 StartY=-10.9474 StartZ=0 EndX=-46.7614 EndY=-10.9474 EndZ=0
    g7: LineSegment StartX=-46.7614 StartY=-10.9474 StartZ=0 EndX=-46.7614 EndY=0 EndZ=0
    g8: Circle CenterX=0 CenterY=-37.7825 CenterZ=0 NormalX=0 NormalY=0 NormalZ=1 AngleXU=0 Radius=29.4005
    g9: LineSegment [constr] StartX=0 StartY=-37.7825 StartZ=0 EndX=44.1357 EndY=-37.7825 EndZ=0
    g10: GeomPoint X=0 Y=-75.565 Z=0
    g11: Circle CenterX=0 CenterY=-37.7825 CenterZ=0 NormalX=0 NormalY=0 NormalZ=1 AngleXU=0 Radius=12.3825
  constraints (30):
    c: Coincident(g1,g0)
    c: Vertical(g1)
    c: Coincident(g2,g1)
    c: Horizontal(g2)
    c: Coincident(g3,g2)
    c: Vertical(g3)
    c: Horizontal(g4)
    c: Coincident(g5,g4)
    c: Coincident(g6,g5)
    c: Horizontal(g6)
    c: Coincident(g7,g0)
    c: Coincident(g6,g7)
    c: Coincident(g4,g3)
    c: Vertical(g5)
    c: Vertical(g7)
    c: Equal(g6,g2)
    c: Equal(g7,g1)
    c: PointOnObject(g-1,g0)
    c: Symmetric(g0,g0,g-2)
    c: DistanceX(g0,g0) = 93.5228
    c: DistanceY(g7,g7) = 10.9474
    c: Distance(g4,g0) = 75.565
    c: Distance(g3,g5) = 69.85
    c: PointOnObject(g8,g-2)
    c: Coincident(g9,g8)
    c: Symmetric(g4,g4,g10)
    c: Symmetric(g10,g-1,g9)
    c: Diameter(g8) = 58.801
    c: Coincident(g11,g8)
    c: Diameter(g11) = 24.765
FEATURE [PartDesign::Pad] Pad025
  Direction = (0,0,1)
  Length = 153.97
  Length2 = 10
  Profile = -> Sketch035 [Edge1,Edge8,Edge7,Edge6,Edge5,Edge4,Edge3,Edge2]
  ReferenceAxis = -> Sketch035 [N_Axis]
  Refine = true
  Suppressed = false
  Type = 0
FEATURE [PartDesign::Pad] Pad026
  BaseFeature = -> Pad025
  Direction = (0,0,1)
  Length = 30.07
  Length2 = 10
  Profile = -> Sketch035 [Edge9]
  ReferenceAxis = -> Sketch035 [N_Axis]
  Refine = true
  Reversed = true
  Suppressed = false
  Type = 0
FEATURE [PartDesign::Pad] Pad027
  BaseFeature = -> Pad026
  Direction = (0,0,1)
  Length = 68.07
  Length2 = 10
  Profile = -> Sketch035 [Edge10]
  ReferenceAxis = -> Sketch035 [N_Axis]
  Refine = true
  Reversed = true
  Suppressed = false
  Type = 0
FEATURE [Sketcher::SketchObject] Sketch036
  ArcFitTolerance = 1e-06
  AttachmentSupport = -> [XZ_Plane064]
  FullyConstrained = false
  MakeInternals = false
  MapMode = 5
  Placement = pos=(0,0,0) rot=(1,0,0;1.5708rad)
  expr: Constraints[26] = 153.97 / 2
  sketch-geometry (12):
    g0: Circle CenterX=-41.275 CenterY=19.835 CenterZ=0 NormalX=0 NormalY=0 NormalZ=1 AngleXU=0 Radius=3
    g1: Circle CenterX=-41.275 CenterY=96.035 CenterZ=0 NormalX=0 NormalY=0 NormalZ=1 AngleXU=0 Radius=3
    g2: Circle CenterX=41.275 CenterY=19.835 CenterZ=0 NormalX=0 NormalY=0 NormalZ=1 AngleXU=0 Radius=3
    g3: Circle CenterX=41.275 CenterY=96.035 CenterZ=0 NormalX=0 NormalY=0 NormalZ=1 AngleXU=0 Radius=3
    g4: Circle CenterX=41.275 CenterY=57.935 CenterZ=0 NormalX=0 NormalY=0 NormalZ=1 AngleXU=0 Radius=3
    g5: LineSegment [constr] StartX=41.275 StartY=19.835 StartZ=0 EndX=41.275 EndY=-158.572 EndZ=0
    g6: LineSegment [constr] StartX=-41.275 StartY=19.835 StartZ=0 EndX=-41.275 EndY=96.035 EndZ=0
    g7: Circle CenterX=-41.275 CenterY=57.935 CenterZ=0 NormalX=0 NormalY=0 NormalZ=1 AngleXU=0 Radius=3
    g8: Circle CenterX=41.275 CenterY=134.135 CenterZ=0 NormalX=0 NormalY=0 NormalZ=1 AngleXU=0 Radius=3
    g9: Circle CenterX=-41.275 CenterY=134.135 CenterZ=0 NormalX=0 NormalY=0 NormalZ=1 AngleXU=0 Radius=3
    g10: GeomPoint [constr] X=40.7257 Y=76.985 Z=0
    g11: LineSegment [constr] StartX=40.7257 StartY=76.985 StartZ=0 EndX=0 EndY=76.985 EndZ=0
  constraints (27):
    c: Coincident(g6,g0)
    c: Vertical(g6)
    c: Coincident(g5,g2)
    c: PointOnObject(g1,g6)
    c: Equal(g3,g2)
    c: Equal(g2,g4)
    c: Equal(g1,g0)
    c: Symmetric(g6,g6,g7)
    c: Equal(g7,g1)
    c: Diameter(g0) = 6
    c: Symmetric(g0,g2,g-2)
    c: Symmetric(g1,g3,g-2)
    c: Symmetric(g7,g4,g-2)
    c: PointOnObject(g8,g5)
    c: PointOnObject(g9,g6)
    c: Symmetric(g9,g8,g-2)
    c: Equal(g8,g9)
    c: Equal(g9,g7)
    c: Coincident(g11,g10)
    c: PointOnObject(g11,g-2)
    c: Symmetric(g2,g8,g11)
    c: Equal(g4,g8)
    c: DistanceY(g3,g8) = 38.1
    c: DistanceY(g4,g3) = 38.1
    c: DistanceY(g2,g4) = 38.1
    c: Distance(g6,g5) = 82.55
    c: Distance(g-1,g11) = 76.985
FEATURE [PartDesign::Pocket] Pocket004
  BaseFeature = -> Pad027
  Direction = (0,1,-2e-16)
  Length = 5
  Length2 = 5
  Profile = -> Sketch036
  ReferenceAxis = -> Sketch036 [N_Axis]
  Refine = true
  Reversed = true
  Suppressed = false
  Type = 1
FEATURE [PartDesign::Body] Body058  label="spindle motor"
  AllowCompound = false
  Group = -> [Sketch035,Pad025,Pad026,Pad027,Sketch036,Pocket004]
  Origin = -> Origin064
  Tip = -> Pocket004
FEATURE [PartDesign::FeatureBase] Clone033
  BaseFeature = -> Body058
  Suppressed = false
FEATURE [PartDesign::Body] Body059  label="spindle motor001"
  AllowCompound = false
  Group = -> [Clone033]
  Origin = -> Origin065
  Placement = pos=(-285,-342.79,263.02) rot=(0,0,1;3.14159rad)
  Tip = -> Clone033
  expr: .Placement.Base.y = -Group001.Base_Z_gantry_depth + 92.7 mm + 0.25 in
  expr: .Placement.Base.z = 263.02 mm
FEATURE [Sketcher::SketchObject] Sketch037
  ArcFitTolerance = 1e-06
  AttachmentSupport = -> [XY_Plane066]
  FullyConstrained = true
  MakeInternals = false
  MapMode = 5
  expr: Constraints[13] = <<nema spreadsheet>>.shaft_diameter
  expr: Constraints[1] = <<nema spreadsheet>>.face_diameter
  expr: Constraints[2] = <<nema spreadsheet>>.mounting_hole_diameter
  expr: Constraints[33] = (<<nema spreadsheet>>.width - <<nema spreadsheet>>.arm_thickness) / 2
  expr: Constraints[64] = <<nema spreadsheet>>.width
  expr: Constraints[6] = <<nema spreadsheet>>.hole_gap
  expr: Constraints[7] = <<nema spreadsheet>>.hole_gap
  sketch-geometry (26):
    g0: Circle CenterX=0 CenterY=0 CenterZ=0 NormalX=0 NormalY=0 NormalZ=1 AngleXU=0 Radius=19.05
    g1: Circle CenterX=-23.57 CenterY=23.57 CenterZ=0 NormalX=0 NormalY=0 NormalZ=1 AngleXU=0 Radius=2.5
    g2: Circle CenterX=23.57 CenterY=23.57 CenterZ=0 NormalX=0 NormalY=0 NormalZ=1 AngleXU=0 Radius=2.5
    g3: Circle CenterX=23.57 CenterY=-23.57 CenterZ=0 NormalX=0 NormalY=0 NormalZ=1 AngleXU=0 Radius=2.5
    g4: Circle CenterX=-23.57 CenterY=-23.57 CenterZ=0 NormalX=0 NormalY=0 NormalZ=1 AngleXU=0 Radius=2.5
    g5: Circle CenterX=0 CenterY=0 CenterZ=0 NormalX=0 NormalY=0 NormalZ=1 AngleXU=0 Radius=4.0005
    g6: LineSegment StartX=-19.05 StartY=28.2 StartZ=0 EndX=-19.05 EndY=19.05 EndZ=0
    g7: LineSegment StartX=-19.05 StartY=19.05 StartZ=0 EndX=-28.2 EndY=19.05 EndZ=0
    g8: LineSegment StartX=-28.2 StartY=-19.05 StartZ=0 EndX=-19.05 EndY=-19.05 EndZ=0
    g9: LineSegment StartX=-19.05 StartY=-19.05 StartZ=0 EndX=-19.05 EndY=-28.2 EndZ=0
    g10: LineSegment StartX=19.05 StartY=-28.2 StartZ=0 EndX=19.05 EndY=-19.05 EndZ=0
    g11: LineSegment StartX=19.05 StartY=-19.05 StartZ=0 EndX=28.2 EndY=-19.05 EndZ=0
    g12: LineSegment StartX=19.05 StartY=28.2 StartZ=0 EndX=19.05 EndY=19.05 EndZ=0
    g13: LineSegment StartX=19.05 StartY=19.05 StartZ=0 EndX=28.2 EndY=19.05 EndZ=0
    g14: LineSegment StartX=-28.2 StartY=19.05 StartZ=0 EndX=-28.2 EndY=-19.05 EndZ=0
    g15: LineSegment StartX=-19.05 StartY=-28.2 StartZ=0 EndX=19.05 EndY=-28.2 EndZ=0
    g16: LineSegment StartX=28.2 StartY=-19.05 StartZ=0 EndX=28.2 EndY=19.05 EndZ=0
    g17: LineSegment StartX=19.05 StartY=28.2 StartZ=0 EndX=-19.05 EndY=28.2 EndZ=0
    g18: LineSegment StartX=-28.2 StartY=19.05 StartZ=0 EndX=-28.2 EndY=28.2 EndZ=0
    g19: LineSegment StartX=-28.2 StartY=28.2 StartZ=0 EndX=-19.05 EndY=28.2 EndZ=0
    g20: LineSegment StartX=19.05 StartY=28.2 StartZ=0 EndX=28.2 EndY=28.2 EndZ=0
    g21: LineSegment StartX=28.2 StartY=28.2 StartZ=0 EndX=28.2 EndY=19.05 EndZ=0
    g22: LineSegment StartX=28.2 StartY=-19.05 StartZ=0 EndX=28.2 EndY=-28.2 EndZ=0
    g23: LineSegment StartX=28.2 StartY=-28.2 StartZ=0 EndX=19.05 EndY=-28.2 EndZ=0
    g24: LineSegment StartX=-19.05 StartY=-28.2 StartZ=0 EndX=-28.2 EndY=-28.2 EndZ=0
    g25: LineSegment StartX=-28.2 StartY=-28.2 StartZ=0 EndX=-28.2 EndY=-19.05 EndZ=0
  constraints (68):
    c: Coincident(g0,g-1)
    c: Diameter(g0) = 38.1
    c: Diameter(g1) = 5
    c: Equal(g1,g4)
    c: Equal(g1,g2)
    c: Equal(g1,g3)
    c: DistanceY(g4,g1) = 47.14
    c: DistanceX(g4,g3) = 47.14
    c: Horizontal(g3,g4)
    c: Vertical(g4,g1)
    c: Symmetric(g2,g1,g-2)
    c: Symmetric(g2,g3,g-1)
    c: Coincident(g5,g0)
    c: Diameter(g5) = 8.001
    c: Coincident(g7,g6)
    c: Coincident(g9,g8)
    c: Coincident(g13,g12)
    c: Vertical(g6)
    c: Vertical(g9)
    c: Vertical(g10)
    c: Vertical(g12)
    c: Horizontal(g7)
    c: Horizontal(g13)
    c: Horizontal(g11)
    c: Horizontal(g8)
    c: Coincident(g11,g10)
    c: Equal(g12,g6)
    c: Equal(g6,g7)
    c: Equal(g7,g13)
    c: Equal(g13,g11)
    c: Equal(g11,g10)
    c: Equal(g10,g9)
    c: Equal(g9,g8)
    c: Distance(g13,g13) = 9.15
    c: Coincident(g14,g7)
    c: Coincident(g14,g8)
    c: Vertical(g14)
    c: Coincident(g15,g9)
    c: Coincident(g15,g10)
    c: Horizontal(g15)
    c: Coincident(g16,g11)
    c: Coincident(g16,g13)
    c: Vertical(g16)
    c: Coincident(g17,g12)
    c: Coincident(g17,g6)
    c: Horizontal(g17)
    c: Coincident(g18,g7)
    c: Coincident(g19,g18)
    c: Coincident(g19,g6)
    c: Coincident(g20,g12)
    c: Coincident(g21,g20)
    c: Coincident(g21,g13)
    c: Coincident(g22,g11)
    c: Coincident(g23,g22)
    c: Coincident(g23,g10)
    c: Coincident(g24,g9)
    c: Horizontal(g24)
    c: Coincident(g25,g24)
    c: Coincident(g25,g8)
    c: Horizontal(g19)
    c: Horizontal(g23)
    c: Vertical(g25)
    c: Vertical(g21)
    c: Vertical(g22)
    c: Distance(g16,g14) = 56.4
    c: Equal(g14,g17)
    c: Symmetric(g18,g24,g-1)
    c: Symmetric(g18,g20,g-2)
FEATURE [PartDesign::Pad] Pad029  label="faceplate"
  Direction = (0,0,1)
  Length = 1.6
  Length2 = 10
  Profile = -> Sketch037 [Edge1]
  ReferenceAxis = -> Sketch037 [N_Axis]
  Refine = true
  Suppressed = false
  Type = 0
  expr: Length = <<nema spreadsheet>>.face_thickness
FEATURE [PartDesign::Pad] Pad030  label="shaft"
  BaseFeature = -> Pad029
  Direction = (0,0,1)
  Length = 21
  Length2 = 10
  Profile = -> Sketch037 [Edge6]
  ReferenceAxis = -> Sketch037 [N_Axis]
  Refine = true
  Suppressed = false
  Type = 0
  expr: Length = <<nema spreadsheet>>.shaft_length
FEATURE [PartDesign::Pad] Pad028  label="mounting_plate"
  BaseFeature = -> Pad030
  Direction = (0,0,1)
  Length = 4.699
  Length2 = 10
  Profile = -> Sketch037 [Edge22,Edge26,Edge25,Edge7,Edge2,Edge9,Edge8,Edge12,Edge14,Edge13,Edge5,Edge17,Edge20,Edge21,Edge4,Edge3]
  ReferenceAxis = -> Sketch037 [N_Axis]
  Refine = true
  Reversed = true
  Suppressed = false
  Type = 0
  expr: Length = <<nema spreadsheet>>.plate_thickness
FEATURE [PartDesign::Pad] Pad031  label="body"
  BaseFeature = -> Pad028
  Direction = (0,0,1)
  Length = 75
  Length2 = 10
  Profile = -> Sketch037 [Edge22,Edge19,Edge18,Edge17,Edge16,Edge15,Edge12,Edge11,Edge10,Edge7,Edge24,Edge23]
  ReferenceAxis = -> Sketch037 [N_Axis]
  Refine = true
  Reversed = true
  Suppressed = false
  Type = 0
  expr: Length = <<nema spreadsheet>>.depth
FEATURE [PartDesign::Body] Body060  label="nema23"
  AllowCompound = false
  Group = -> [Sketch037,Pad029,Pad030,Pad028,Pad031]
  Origin = -> Origin066
  Tip = -> Pad031
FEATURE [Spreadsheet::Sheet] Spreadsheet  label="nema spreadsheet"
  cells = A1='width; B1(width)==56.4 mm; A2='attachment hole gap; B2(hole_gap)==47.14 mm; A3='body depth; B3(depth)==75 mm; A4='shaft length (from main body, not circle); B4(shaft_length)==21 mm; A5='face circle diameter; B5(face_diameter)==1.5 in; A6='face circle thickness; B6(face_thickness)==1.6 mm; A7='shaft diameter; B7(shaft_diameter)==0.315 in; A8='mounting hole diameter; B8(mounting_hole_diameter)==5 mm; A9='mounting plate thickness; B9(plate_thickness)==0.185 in; A10='cross body arm thickness; B10(arm_thickness)==1.5 in
FEATURE [PartDesign::FeatureBase] Clone034
  BaseFeature = -> Body060
  Suppressed = false
FEATURE [PartDesign::Body] Body061  label="nema23_01"
  AllowCompound = false
  Group = -> [Clone034]
  Origin = -> Origin067
  Placement = pos=(-285,-75,48.2) rot=(1,0,0;1.5708rad)
  Tip = -> Clone034
FEATURE [Sketcher::SketchObject] Sketch038
  ArcFitTolerance = 1e-06
  AttachmentSupport = -> [XZ_Plane068]
  FullyConstrained = true
  MakeInternals = false
  MapMode = 5
  Placement = pos=(0,0,0) rot=(1,0,0;1.5708rad)
  sketch-geometry (2):
    g0: Circle CenterX=0 CenterY=0 CenterZ=0 NormalX=0 NormalY=0 NormalZ=1 AngleXU=0 Radius=9.3853
    g1: Circle CenterX=0 CenterY=0 CenterZ=0 NormalX=0 NormalY=0 NormalZ=1 AngleXU=0 Radius=4
  constraints (4):
    c: Coincident(g0,g-1)
    c: Diameter(g0) = 18.7706
    c: Coincident(g1,g0)
    c: Diameter(g1) = 8
FEATURE [PartDesign::Pad] Pad032
  Direction = (0,-1,2e-16)
  Length = 24.69
  Length2 = 10
  Placement = pos=(0,0,0) rot=(1,0,0;1.5708rad)
  Profile = -> Sketch038
  ReferenceAxis = -> Sketch038 [N_Axis]
  Refine = true
  Suppressed = false
  Type = 0
FEATURE [PartDesign::Body] Body062  label="sfu12 coupler"
  AllowCompound = false
  Group = -> [Sketch038,Pad032]
  Origin = -> Origin068
  Tip = -> Pad032
FEATURE [PartDesign::FeatureBase] Clone035
  BaseFeature = -> Body062
  Suppressed = false
FEATURE [PartDesign::Body] Body063  label="sfu12 coupler001"
  AllowCompound = false
  Group = -> [Clone035]
  Origin = -> Origin069
  Placement = pos=(-285,-75,48.2) rot=(0,0,1;0rad)
  Tip = -> Clone035
FEATURE [PartDesign::FeatureBase] Clone036
  BaseFeature = -> Body020
  Suppressed = false
FEATURE [PartDesign::Body] Body064  label="sfu12 500mm"
  AllowCompound = false
  Group = -> [Clone036]
  Origin = -> Origin070
  Placement = pos=(-285,-75,48.2) rot=(0,0,1;-1.5708rad)
  Tip = -> Clone036
FEATURE [Sketcher::SketchObject] Sketch039
  ArcFitTolerance = 1e-06
  AttachmentSupport = -> [XY_Plane071]
  FullyConstrained = true
  MakeInternals = false
  MapMode = 5
  sketch-geometry (10):
    g0: LineSegment StartX=-10 StartY=0 StartZ=0 EndX=10 EndY=0 EndZ=0
    g1: LineSegment StartX=10 StartY=0 StartZ=0 EndX=10 EndY=8.5 EndZ=0
    g2: LineSegment StartX=-10 StartY=0 StartZ=0 EndX=-10 EndY=8.5 EndZ=0
    g3: LineSegment StartX=-10 StartY=14.5 StartZ=0 EndX=-10 EndY=17.7218 EndZ=0
    g4: LineSegment StartX=-10 StartY=17.7218 StartZ=0 EndX=-7.72183 EndY=20 EndZ=0
    g5: LineSegment StartX=-7.72183 StartY=20 StartZ=0 EndX=7.72183 EndY=20 EndZ=0
    g6: LineSegment StartX=7.72183 StartY=20 StartZ=0 EndX=10 EndY=17.7218 EndZ=0
    g7: LineSegment StartX=10 StartY=17.7218 StartZ=0 EndX=10 EndY=14.5 EndZ=0
    g8: ArcOfCircle CenterX=-10 CenterY=11.5 CenterZ=0 NormalX=0 NormalY=0 NormalZ=1 AngleXU=0 Radius=3 StartAngle=4.71239 EndAngle=7.85398
    g9: ArcOfCircle CenterX=9.99998 CenterY=11.5 CenterZ=0 NormalX=0 NormalY=0 NormalZ=1 AngleXU=0 Radius=3 StartAngle=1.57079 EndAngle=4.7124
  constraints (30):
    c: Coincident(g1,g0)
    c: Coincident(g2,g0)
    c: Coincident(g4,g3)
    c: Coincident(g5,g4)
    c: Horizontal(g5)
    c: Coincident(g6,g5)
    c: Coincident(g7,g6)
    c: Vertical(g7)
    c: Coincident(g8,g3)
    c: Coincident(g8,g2)
    c: Coincident(g9,g1)
    c: Coincident(g9,g7)
    c: Equal(g8,g9)
    c: Equal(g1,g2)
    c: Equal(g3,g7)
    c: Equal(g6,g4)
    c: Distance(g0,g0) = 20
    c: Symmetric(g0,g0,g-2)
    c: Vertical(g2)
    c: Vertical(g1)
    c: Tangent(g3,g2)
    c: PointOnObject(g7,g1)
    c: Radius(g8) = 3
    c: Angle(g4,g3) = 0.785398
    c: Angle(g6,g7) = 2.35619
    c: Distance(g0,g5) = 20
    c: PointOnObject(g8,g3)
    c: Distance(g8,g5) = 8.5
    c: PointOnObject(g-1,g0)
    c: Equal(g4,g3)
FEATURE [PartDesign::Pad] Pad033
  Direction = (0,0,1)
  Length = 400
  Length2 = 10
  Profile = -> Sketch039
  ReferenceAxis = -> Sketch039 [N_Axis]
  Refine = true
  Suppressed = false
  Type = 0
FEATURE [PartDesign::Body] Body065  label="HGR20x400"
  AllowCompound = false
  Group = -> [Sketch039,Pad033]
  Origin = -> Origin071
  Tip = -> Pad033
FEATURE [Sketcher::SketchObject] Sketch040
  ArcFitTolerance = 1e-06
  AttachmentSupport = -> [XY_Plane072]
  FullyConstrained = true
  MakeInternals = false
  MapMode = 5
  sketch-geometry (8):
    g0: LineSegment StartX=0 StartY=0 StartZ=0 EndX=400 EndY=0 EndZ=0
    g1: LineSegment StartX=0 StartY=0 StartZ=0 EndX=0 EndY=4 EndZ=0
    g2: LineSegment StartX=0 StartY=4 StartZ=0 EndX=54 EndY=4 EndZ=0
    g3: LineSegment StartX=54 StartY=4 StartZ=0 EndX=54 EndY=6 EndZ=0
    g4: LineSegment StartX=400 StartY=0 StartZ=0 EndX=400 EndY=4 EndZ=0
    g5: LineSegment StartX=400 StartY=4 StartZ=0 EndX=389 EndY=4 EndZ=0
    g6: LineSegment StartX=389 StartY=4 StartZ=0 EndX=389 EndY=6 EndZ=0
    g7: LineSegment StartX=389 StartY=6 StartZ=0 EndX=54 EndY=6 EndZ=0
  constraints (23):
    c: Coincident(g0,g-1)
    c: Horizontal(g0)
    c: DistanceX(g0,g0) = 400
    c: Coincident(g1,g0)
    c: PointOnObject(g1,g-2)
    c: Distance(g1,g1) = 4
    c: Coincident(g2,g1)
    c: Horizontal(g2)
    c: DistanceX(g2,g2) = 54
    c: Coincident(g3,g2)
    c: Vertical(g3)
    c: Distance(g3,g3) = 2
    c: Coincident(g4,g0)
    c: Vertical(g4)
    c: DistanceY(g4,g4) = 4
    c: Coincident(g5,g4)
    c: Horizontal(g5)
    c: DistanceX(g5,g5) = 11
    c: Coincident(g6,g5)
    c: Vertical(g6)
    c: DistanceY(g6,g6) = 2
    c: Coincident(g7,g6)
    c: Coincident(g7,g3)
FEATURE [PartDesign::Revolution] Revolution001
  Angle = 360
  Angle2 = 60
  Axis = (1,0,0)
  Base = (0,0,0)
  Profile = -> Sketch040
  ReferenceAxis = -> Sketch040 [H_Axis]
  Refine = true
  Suppressed = false
  Type = 0
FEATURE [PartDesign::Body] Body066  label="sfu1204x400mm"
  AllowCompound = false
  Group = -> [Sketch040,Revolution001]
  Origin = -> Origin072
  Tip = -> Revolution001
FEATURE [Sketcher::SketchObject] Sketch041
  ArcFitTolerance = 1e-06
  AttachmentSupport = -> [XY_Plane073]
  FullyConstrained = true
  MakeInternals = false
  MapMode = 5
  sketch-geometry (10):
    g0: LineSegment StartX=-10 StartY=0 StartZ=0 EndX=10 EndY=0 EndZ=0
    g1: LineSegment StartX=10 StartY=0 StartZ=0 EndX=10 EndY=8.5 EndZ=0
    g2: LineSegment StartX=-10 StartY=0 StartZ=0 EndX=-10 EndY=8.5 EndZ=0
    g3: LineSegment StartX=-10 StartY=14.5 StartZ=0 EndX=-10 EndY=17.7218 EndZ=0
    g4: LineSegment StartX=-10 StartY=17.7218 StartZ=0 EndX=-7.72183 EndY=20 EndZ=0
    g5: LineSegment StartX=-7.72183 StartY=20 StartZ=0 EndX=7.72183 EndY=20 EndZ=0
    g6: LineSegment StartX=7.72183 StartY=20 StartZ=0 EndX=10 EndY=17.7218 EndZ=0
    g7: LineSegment StartX=10 StartY=17.7218 StartZ=0 EndX=10 EndY=14.5 EndZ=0
    g8: ArcOfCircle CenterX=-10 CenterY=11.5 CenterZ=0 NormalX=0 NormalY=0 NormalZ=1 AngleXU=0 Radius=3 StartAngle=4.71239 EndAngle=7.85398
    g9: ArcOfCircle CenterX=9.99998 CenterY=11.5 CenterZ=0 NormalX=0 NormalY=0 NormalZ=1 AngleXU=0 Radius=3 StartAngle=1.57079 EndAngle=4.7124
  constraints (30):
    c: Coincident(g1,g0)
    c: Coincident(g2,g0)
    c: Coincident(g4,g3)
    c: Coincident(g5,g4)
    c: Horizontal(g5)
    c: Coincident(g6,g5)
    c: Coincident(g7,g6)
    c: Vertical(g7)
    c: Coincident(g8,g3)
    c: Coincident(g8,g2)
    c: Coincident(g9,g1)
    c: Coincident(g9,g7)
    c: Equal(g8,g9)
    c: Equal(g1,g2)
    c: Equal(g3,g7)
    c: Equal(g6,g4)
    c: Distance(g0,g0) = 20
    c: Symmetric(g0,g0,g-2)
    c: Vertical(g2)
    c: Vertical(g1)
    c: Tangent(g3,g2)
    c: PointOnObject(g7,g1)
    c: Radius(g8) = 3
    c: Angle(g4,g3) = 0.785398
    c: Angle(g6,g7) = 2.35619
    c: Distance(g0,g5) = 20
    c: PointOnObject(g8,g3)
    c: Distance(g8,g5) = 8.5
    c: PointOnObject(g-1,g0)
    c: Equal(g4,g3)
FEATURE [PartDesign::Pad] Pad034
  Direction = (0,0,1)
  Length = 200
  Length2 = 10
  Profile = -> Sketch041
  ReferenceAxis = -> Sketch041 [N_Axis]
  Refine = true
  Suppressed = false
  Type = 0
FEATURE [PartDesign::Body] Body067  label="HGR20x200"
  AllowCompound = false
  Group = -> [Sketch041,Pad034]
  Origin = -> Origin073
  Tip = -> Pad034
FEATURE [Sketcher::SketchObject] Sketch042
  ArcFitTolerance = 1e-06
  AttachmentSupport = -> [XY_Plane074]
  FullyConstrained = true
  MakeInternals = false
  MapMode = 5
  sketch-geometry (8):
    g0: LineSegment StartX=0 StartY=0 StartZ=0 EndX=200 EndY=0 EndZ=0
    g1: LineSegment StartX=0 StartY=0 StartZ=0 EndX=0 EndY=4 EndZ=0
    g2: LineSegment StartX=0 StartY=4 StartZ=0 EndX=54 EndY=4 EndZ=0
    g3: LineSegment StartX=54 StartY=4 StartZ=0 EndX=54 EndY=6 EndZ=0
    g4: LineSegment StartX=200 StartY=0 StartZ=0 EndX=200 EndY=4 EndZ=0
    g5: LineSegment StartX=200 StartY=4 StartZ=0 EndX=189 EndY=4 EndZ=0
    g6: LineSegment StartX=189 StartY=4 StartZ=0 EndX=189 EndY=6 EndZ=0
    g7: LineSegment StartX=189 StartY=6 StartZ=0 EndX=54 EndY=6 EndZ=0
  constraints (23):
    c: Coincident(g0,g-1)
    c: Horizontal(g0)
    c: DistanceX(g0,g0) = 200
    c: Coincident(g1,g0)
    c: PointOnObject(g1,g-2)
    c: Distance(g1,g1) = 4
    c: Coincident(g2,g1)
    c: Horizontal(g2)
    c: DistanceX(g2,g2) = 54
    c: Coincident(g3,g2)
    c: Vertical(g3)
    c: Distance(g3,g3) = 2
    c: Coincident(g4,g0)
    c: Vertical(g4)
    c: DistanceY(g4,g4) = 4
    c: Coincident(g5,g4)
    c: Horizontal(g5)
    c: DistanceX(g5,g5) = 11
    c: Coincident(g6,g5)
    c: Vertical(g6)
    c: DistanceY(g6,g6) = 2
    c: Coincident(g7,g6)
    c: Coincident(g7,g3)
FEATURE [PartDesign::Revolution] Revolution002
  Angle = 360
  Angle2 = 60
  Axis = (1,0,0)
  Base = (0,0,0)
  Profile = -> Sketch042
  ReferenceAxis = -> Sketch042 [H_Axis]
  Refine = true
  Suppressed = false
  Type = 0
FEATURE [PartDesign::Body] Body068  label="sfu1204x200mm"
  AllowCompound = false
  Group = -> [Sketch042,Revolution002]
  Origin = -> Origin074
  Tip = -> Revolution002
FEATURE [PartDesign::FeatureBase] Clone037
  BaseFeature = -> Body065
  Suppressed = false
FEATURE [PartDesign::Body] Body069  label="HGR20x400_01"
  AllowCompound = false
  Group = -> [Clone037]
  Origin = -> Origin075
  Placement = pos=(-485,-205,92.7) rot=(0.57735,0.57735,0.57735;2.0944rad)
  Tip = -> Clone037
  expr: .Placement.Base.y = -205 mm + Group001.Base_x_coord
FEATURE [PartDesign::FeatureBase] Clone038
  BaseFeature = -> Body065
  Suppressed = false
FEATURE [PartDesign::Body] Body070  label="HGR20x400_02"
  AllowCompound = false
  Group = -> [Clone038]
  Origin = -> Origin076
  Placement = pos=(-485,-405,92.7) rot=(0.57735,0.57735,0.57735;2.0944rad)
  Tip = -> Clone038
  expr: .Placement.Base.y = -405 mm + Group001.Base_x_coord
FEATURE [PartDesign::FeatureBase] Clone039
  BaseFeature = -> Body007
  Suppressed = false
FEATURE [PartDesign::Body] Body071  label="HGR20 carriage001"
  AllowCompound = false
  Group = -> [Clone039]
  Origin = -> Origin077
  Placement = pos=(-241.5,-205,97.3) rot=(0.57735,0.57735,0.57735;2.0944rad)
  Tip = -> Clone039
  expr: .Placement.Base.x = -241.5 mm + Group001.Base_y_coord
  expr: .Placement.Base.y = -205 mm + Group001.Base_x_coord
FEATURE [PartDesign::FeatureBase] Clone040
  BaseFeature = -> Body007
  Suppressed = false
FEATURE [PartDesign::Body] Body072  label="HGR20 carriage002"
  AllowCompound = false
  Group = -> [Clone040]
  Origin = -> Origin078
  Placement = pos=(-401.5,-205,97.3) rot=(0.57735,0.57735,0.57735;2.0944rad)
  Tip = -> Clone040
  expr: .Placement.Base.x = -401.5 mm + Group001.Base_y_coord
  expr: .Placement.Base.y = -205 mm + Group001.Base_x_coord
FEATURE [PartDesign::FeatureBase] Clone041
  BaseFeature = -> Body007
  Suppressed = false
FEATURE [PartDesign::Body] Body073  label="HGR20 carriage003"
  AllowCompound = false
  Group = -> [Clone041]
  Origin = -> Origin079
  Placement = pos=(-241.5,-405,97.3) rot=(0.57735,0.57735,0.57735;2.0944rad)
  Tip = -> Clone041
  expr: .Placement.Base.x = -241.5 mm + Group001.Base_y_coord
  expr: .Placement.Base.y = -405 mm + Group001.Base_x_coord
FEATURE [PartDesign::FeatureBase] Clone042
  BaseFeature = -> Body007
  Suppressed = false
FEATURE [PartDesign::Body] Body074  label="HGR20 carriage004"
  AllowCompound = false
  Group = -> [Clone042]
  Origin = -> Origin080
  Placement = pos=(-401.5,-405,97.3) rot=(0.57735,0.57735,0.57735;2.0944rad)
  Tip = -> Clone042
  expr: .Placement.Base.x = -401.5 mm + Group001.Base_y_coord
  expr: .Placement.Base.y = -405 mm + Group001.Base_x_coord
FEATURE [PartDesign::FeatureBase] Clone043
  BaseFeature = -> Body019
  Suppressed = false
FEATURE [PartDesign::Body] Body075  label="hgr20 spacer"
  AllowCompound = false
  Group = -> [Clone043]
  Origin = -> Origin081
  Placement = pos=(-241.5,-180,122.7) rot=(0,0,1;-1.5708rad)
  Tip = -> Clone043
  expr: .Placement.Base.x = -241.5 mm + Group001.Base_y_coord
  expr: .Placement.Base.y = -180 mm + Group001.Base_x_coord
FEATURE [PartDesign::FeatureBase] Clone044
  BaseFeature = -> Body019
  Suppressed = false
FEATURE [PartDesign::Body] Body076  label="hgr20 spacer001"
  AllowCompound = false
  Group = -> [Clone044]
  Origin = -> Origin082
  Placement = pos=(-401.5,-180,122.7) rot=(0,0,1;-1.5708rad)
  Tip = -> Clone044
  expr: .Placement.Base.x = -401.5 mm + Group001.Base_y_coord
  expr: .Placement.Base.y = -180 mm + Group001.Base_x_coord
FEATURE [PartDesign::FeatureBase] Clone045
  BaseFeature = -> Body019
  Suppressed = false
FEATURE [PartDesign::Body] Body077  label="hgr20 spacer002"
  AllowCompound = false
  Group = -> [Clone045]
  Origin = -> Origin083
  Placement = pos=(-241.5,-380,122.7) rot=(0,0,1;-1.5708rad)
  Tip = -> Clone045
  expr: .Placement.Base.x = -241.5 mm + Group001.Base_y_coord
  expr: .Placement.Base.y = -380 mm + Group001.Base_x_coord
FEATURE [PartDesign::FeatureBase] Clone046
  BaseFeature = -> Body019
  Suppressed = false
FEATURE [PartDesign::Body] Body078  label="hgr20 spacer003"
  AllowCompound = false
  Group = -> [Clone046]
  Origin = -> Origin084
  Placement = pos=(-401.5,-380,122.7) rot=(0,0,1;-1.5708rad)
  Tip = -> Clone046
  expr: .Placement.Base.x = -401.5 mm + Group001.Base_y_coord
  expr: .Placement.Base.y = -380 mm + Group001.Base_x_coord
FEATURE [Sketcher::SketchObject] Sketch043
  ArcFitTolerance = 1e-06
  AttachmentSupport = -> [XZ_Plane086]
  FullyConstrained = true
  MakeInternals = false
  MapMode = 5
  Placement = pos=(0,0,0) rot=(1,0,0;1.5708rad)
  sketch-geometry (18):
    g0: LineSegment StartX=-101.6 StartY=127 StartZ=0 EndX=-101.6 EndY=-127 EndZ=0
    g1: LineSegment StartX=-101.6 StartY=-127 StartZ=0 EndX=101.6 EndY=-127 EndZ=0
    g2: LineSegment StartX=101.6 StartY=-127 StartZ=0 EndX=101.6 EndY=127 EndZ=0
    g3: LineSegment StartX=101.6 StartY=127 StartZ=0 EndX=-101.6 EndY=127 EndZ=0
    g4: Circle CenterX=-41.275 CenterY=57.15 CenterZ=0 NormalX=0 NormalY=0 NormalZ=1 AngleXU=0 Radius=3.175
    g5: Circle CenterX=-41.275 CenterY=19.05 CenterZ=0 NormalX=0 NormalY=0 NormalZ=1 AngleXU=0 Radius=3.175
    g6: Circle CenterX=-41.275 CenterY=-19.05 CenterZ=0 NormalX=0 NormalY=0 NormalZ=1 AngleXU=0 Radius=3.175
    g7: Circle CenterX=-41.275 CenterY=-57.15 CenterZ=0 NormalX=0 NormalY=0 NormalZ=1 AngleXU=0 Radius=3.175
    g8: Circle CenterX=41.275 CenterY=57.15 CenterZ=0 NormalX=0 NormalY=0 NormalZ=1 AngleXU=0 Radius=3.175
    g9: Circle CenterX=41.275 CenterY=19.05 CenterZ=0 NormalX=0 NormalY=0 NormalZ=1 AngleXU=0 Radius=3.175
    g10: Circle CenterX=41.275 CenterY=-19.05 CenterZ=0 NormalX=0 NormalY=0 NormalZ=1 AngleXU=0 Radius=3.175
    g11: Circle CenterX=41.275 CenterY=-57.15 CenterZ=0 NormalX=0 NormalY=0 NormalZ=1 AngleXU=0 Radius=3.175
    g12: LineSegment [constr] StartX=-41.275 StartY=57.15 StartZ=0 EndX=-41.275 EndY=-57.15 EndZ=0
    g13: LineSegment [constr] StartX=41.275 StartY=57.15 StartZ=0 EndX=41.275 EndY=-57.15 EndZ=0
    g14: LineSegment [constr] StartX=-41.275 StartY=-19.05 StartZ=0 EndX=41.275 EndY=-19.05 EndZ=0
    g15: LineSegment [constr] StartX=-41.275 StartY=19.05 StartZ=0 EndX=41.275 EndY=19.05 EndZ=0
    g16: LineSegment [constr] StartX=-41.275 StartY=57.15 StartZ=0 EndX=41.275 EndY=57.15 EndZ=0
    g17: LineSegment [constr] StartX=-41.275 StartY=-57.15 StartZ=0 EndX=41.275 EndY=-57.15 EndZ=0
  constraints (44):
    c: Coincident(g0,g1)
    c: Coincident(g1,g2)
    c: Coincident(g2,g3)
    c: Coincident(g3,g0)
    c: Vertical(g2)
    c: Horizontal(g1)
    c: Symmetric(g0,g0,g-1)
    c: Symmetric(g0,g2,g-2)
    c: DistanceY(g0,g0) = 254
    c: DistanceX(g3,g3) = 203.2
    c: Coincident(g12,g4)
    c: Coincident(g12,g7)
    c: Coincident(g13,g8)
    c: Coincident(g13,g11)
    c: Vertical(g13)
    c: PointOnObject(g10,g13)
    c: PointOnObject(g5,g12)
    c: Horizontal(g7,g11)
    c: PointOnObject(g6,g12)
    c: Horizontal(g6,g10)
    c: Horizontal(g5,g9)
    c: Equal(g8,g4)
    c: Equal(g4,g5)
    c: Equal(g5,g6)
    c: Equal(g6,g9)
    c: Equal(g9,g10)
    c: Equal(g10,g11)
    c: Equal(g11,g7)
    c: Vertical(g12)
    c: Distance(g13,g12) = 82.55
    c: Diameter(g8) = 6.35
    c: Coincident(g14,g6)
    c: Coincident(g14,g10)
    c: Coincident(g15,g5)
    c: Coincident(g15,g9)
    c: Coincident(g16,g4)
    c: Coincident(g16,g8)
    c: Coincident(g17,g7)
    c: Coincident(g17,g11)
    c: Distance(g15,g16) = 38.1
    c: Distance(g14,g15) = 38.1
    c: Distance(g14,g17) = 38.1
    c: Symmetric(g4,g8,g-2)
    c: Symmetric(g9,g10,g-1)
FEATURE [PartDesign::Pad] Pad035
  Direction = (0,-1,2e-16)
  Length = 6.35
  Length2 = 10
  Placement = pos=(0,0,0) rot=(1,0,0;1.5708rad)
  Profile = -> Sketch043
  ReferenceAxis = -> Sketch043 [N_Axis]
  Refine = true
  Suppressed = false
  Type = 0
FEATURE [PartDesign::Body] Body080  label="Z-axis plate"
  AllowCompound = false
  Group = -> [Sketch043,Pad035]
  Origin = -> Origin086
  Tip = -> Pad035
FEATURE [PartDesign::FeatureBase] Clone048
  BaseFeature = -> Body080
  Suppressed = false
FEATURE [PartDesign::Body] Body081  label="Z axis mount"
  AllowCompound = false
  Group = -> [Clone048]
  Origin = -> Origin087
  Placement = pos=(-285,-342.79,340) rot=(0,0,1;0rad)
  Tip = -> Clone048
  expr: .Placement.Base.y = 92.7 mm + 0.25 in - Group001.Base_Z_gantry_depth
FEATURE [PartDesign::FeatureBase] Clone049
  BaseFeature = -> Body043
  Suppressed = false
FEATURE [PartDesign::Body] Body082  label="z mount plate"
  AllowCompound = false
  Group = -> [Clone049]
  Origin = -> Origin088
  Placement = pos=(-285,-409.14,340) rot=(0,0,1;0rad)
  Tip = -> Clone049
  expr: .Placement.Base.y = 20 mm + 0.5 in - Group001.Base_Z_gantry_depth
FEATURE [App::DocumentObjectGroup] Group  label="frame"
  Group = -> [Body042,Body037,Body036,Body039,Body035,Body038,Body034,Body022,Body033,Body041,Body032,Body025,Body021,Body024,Body023,Body026,Body027,Body028,Body029,Body030,Body040,Body031,Body082]
FEATURE [PartDesign::FeatureBase] Clone050
  BaseFeature = -> Body067
  Suppressed = false
FEATURE [PartDesign::Body] Body083  label="hgr20x200"
  AllowCompound = false
  Group = -> [Clone050]
  Origin = -> Origin089
  Placement = pos=(-355,-409.14,240) rot=(0,0,1;0rad)
  Tip = -> Clone050
  expr: .Placement.Base.y = 20 mm + 0.5 in - Group001.Base_Z_gantry_depth
FEATURE [PartDesign::FeatureBase] Clone051
  BaseFeature = -> Body067
  Suppressed = false
FEATURE [PartDesign::Body] Body084  label="hgr20x200b"
  AllowCompound = false
  Group = -> [Clone051]
  Origin = -> Origin090
  Placement = pos=(-210,-409.14,240) rot=(0,0,1;0rad)
  Tip = -> Clone051
  expr: .Placement.Base.y = 20 mm + 0.5 in - Group001.Base_Z_gantry_depth
FEATURE [PartDesign::FeatureBase] Clone053
  BaseFeature = -> Body007
  Suppressed = false
FEATURE [PartDesign::Body] Body086  label="hgr20 carriage001"
  AllowCompound = false
  Group = -> [Clone053]
  Origin = -> Origin092
  Placement = pos=(-355,-404.54,300) rot=(0,0,1;0rad)
  Tip = -> Clone053
  expr: .Placement.Base.y = 24.6 mm + 0.5 in - Group001.Base_Z_gantry_depth
FEATURE [PartDesign::FeatureBase] Clone055
  BaseFeature = -> Body007
  Suppressed = false
FEATURE [PartDesign::Body] Body088  label="hgr20 carriage003"
  AllowCompound = false
  Group = -> [Clone055]
  Origin = -> Origin094
  Placement = pos=(-210,-404.54,300) rot=(0,0,1;0rad)
  Tip = -> Clone055
  expr: .Placement.Base.y = 24.6 mm + 0.5 in - Group001.Base_Z_gantry_depth
FEATURE [PartDesign::FeatureBase] Clone057
  BaseFeature = -> Body019
  Suppressed = false
FEATURE [PartDesign::Body] Body090  label="hgr spacer001"
  AllowCompound = false
  Group = -> [Clone057]
  Origin = -> Origin096
  Placement = pos=(-235,-349.14,300) rot=(1,0,0;1.5708rad)
  Tip = -> Clone057
  expr: .Placement.Base.y = -Group001.Base_Z_gantry_depth + 92.7 mm
FEATURE [PartDesign::FeatureBase] Clone059
  BaseFeature = -> Body019
  Suppressed = false
FEATURE [PartDesign::Body] Body092  label="hgr spacer003"
  AllowCompound = false
  Group = -> [Clone059]
  Origin = -> Origin098
  Placement = pos=(-380,-349.14,300) rot=(1,0,0;1.5708rad)
  Tip = -> Clone059
  expr: .Placement.Base.y = -Group001.Base_Z_gantry_depth + 92.7 mm
FEATURE [Sketcher::SketchObject] Sketch044
  ArcFitTolerance = 1e-06
  AttachmentSupport = -> [XY_Plane099]
  FullyConstrained = true
  MakeInternals = false
  MapMode = 5
  sketch-geometry (20):
    g0: LineSegment StartX=30 StartY=-35.75 StartZ=0 EndX=-30 EndY=-35.75 EndZ=0
    g1: LineSegment StartX=-30 StartY=-35.75 StartZ=0 EndX=-30 EndY=-3.25 EndZ=0
    g2: LineSegment StartX=-30 StartY=-3.25 StartZ=0 EndX=-18 EndY=-3.25 EndZ=0
    g3: LineSegment StartX=-18 StartY=-3.25 StartZ=0 EndX=-18 EndY=3.25 EndZ=0
    g4: LineSegment StartX=-18 StartY=3.25 StartZ=0 EndX=18 EndY=3.25 EndZ=0
    g5: LineSegment StartX=18 StartY=3.25 StartZ=0 EndX=18 EndY=-3.25 EndZ=0
    g6: LineSegment StartX=18 StartY=-3.25 StartZ=0 EndX=30 EndY=-3.25 EndZ=0
    g7: LineSegment StartX=30 StartY=-3.25 StartZ=0 EndX=30 EndY=-35.75 EndZ=0
    g8: Circle CenterX=-23 CenterY=-28.75 CenterZ=0 NormalX=0 NormalY=0 NormalZ=1 AngleXU=0 Radius=2.75
    g9: Circle CenterX=-23 CenterY=-13.75 CenterZ=0 NormalX=0 NormalY=0 NormalZ=1 AngleXU=0 Radius=2.75
    g10: Circle CenterX=23 CenterY=-13.75 CenterZ=0 NormalX=0 NormalY=0 NormalZ=1 AngleXU=0 Radius=2.75
    g11: Circle CenterX=23 CenterY=-28.75 CenterZ=0 NormalX=0 NormalY=0 NormalZ=1 AngleXU=0 Radius=2.75
    g12: LineSegment [constr] StartX=-23 StartY=-13.75 StartZ=0 EndX=23 EndY=-13.75 EndZ=0
    g13: LineSegment [constr] StartX=-23 StartY=-28.75 StartZ=0 EndX=23 EndY=-28.75 EndZ=0
    g14: LineSegment [constr] StartX=-23 StartY=-13.75 StartZ=0 EndX=-23 EndY=-28.75 EndZ=0
    g15: LineSegment [constr] StartX=23 StartY=-13.75 StartZ=0 EndX=23 EndY=-28.75 EndZ=0
    g16: Circle CenterX=-3e-16 CenterY=-13.75 CenterZ=0 NormalX=0 NormalY=0 NormalZ=1 AngleXU=0 Radius=5
    g17: LineSegment StartX=-18 StartY=-3.25 StartZ=0 EndX=-18 EndY=-30.75 EndZ=0
    g18: LineSegment StartX=-18 StartY=-30.75 StartZ=0 EndX=18 EndY=-30.75 EndZ=0
    g19: LineSegment StartX=18 StartY=-30.75 StartZ=0 EndX=18 EndY=-3.25 EndZ=0
  constraints (49):
    c: Horizontal(g0)
    c: Coincident(g1,g0)
    c: Coincident(g2,g1)
    c: Coincident(g3,g2)
    c: Vertical(g3)
    c: Coincident(g4,g3)
    c: Coincident(g5,g4)
    c: Coincident(g7,g0)
    c: Coincident(g6,g7)
    c: Coincident(g5,g6)
    c: Horizontal(g6)
    c: Vertical(g1)
    c: Vertical(g7)
    c: Tangent(g2,g6)
    c: Equal(g2,g6)
    c: DistanceX(g0,g0) = 60
    c: Symmetric(g3,g4,g-2)
    c: Symmetric(g5,g4,g-1)
    c: DistanceY(g7,g7) = 32.5
    c: Distance(g0,g4) = 39
    c: DistanceX(g2,g2) = 12
    c: Equal(g11,g10)
    c: Equal(g10,g9)
    c: Equal(g9,g8)
    c: Diameter(g8) = 5.5
    c: DistanceY(g8,g9) = 15
    c: Coincident(g12,g9)
    c: Coincident(g12,g10)
    c: Coincident(g13,g8)
    c: Coincident(g13,g11)
    c: Symmetric(g9,g10,g-2)
    c: Symmetric(g8,g11,g-2)
    c: Coincident(g14,g9)
    c: Coincident(g14,g8)
    c: Vertical(g14)
    c: Coincident(g15,g10)
    c: Coincident(g15,g11)
    c: Distance(g15,g14) = 46
    c: Symmetric(g12,g12,g16)
    c: Diameter(g16) = 10
    c: Distance(g0,g12) = 22
    c: Coincident(g17,g2)
    c: Vertical(g17)
    c: Coincident(g18,g17)
    c: Horizontal(g18)
    c: Coincident(g19,g18)
    c: Coincident(g19,g5)
    c: Vertical(g19)
    c: Distance(g18,g4) = 34
FEATURE [Sketcher::SketchObject] Sketch045
  ArcFitTolerance = 1e-06
  FullyConstrained = true
  MakeInternals = false
  MapMode = 5
  Placement = pos=(-1e-16,-3.25,0) rot=(0,0.707107,0.707107;3.14159rad)
  sketch-geometry (7):
    g0: Circle CenterX=-23 CenterY=6 CenterZ=0 NormalX=0 NormalY=0 NormalZ=1 AngleXU=0 Radius=3.3
    g1: Circle CenterX=23 CenterY=6 CenterZ=0 NormalX=0 NormalY=0 NormalZ=1 AngleXU=0 Radius=3.3
    g2: Circle CenterX=23 CenterY=19 CenterZ=0 NormalX=0 NormalY=0 NormalZ=1 AngleXU=0 Radius=3.3
    g3: Circle CenterX=-23 CenterY=19 CenterZ=0 NormalX=0 NormalY=0 NormalZ=1 AngleXU=0 Radius=3.3
    g4: LineSegment [constr] StartX=-23 StartY=6 StartZ=0 EndX=-23 EndY=19 EndZ=0
    g5: LineSegment [constr] StartX=23 StartY=19 StartZ=0 EndX=23 EndY=6 EndZ=0
    g6: LineSegment [constr] StartX=-23 StartY=19 StartZ=0 EndX=23 EndY=19 EndZ=0
  constraints (17):
    c: Equal(g1,g0)
    c: Diameter(g0) = 6.6
    c: Symmetric(g0,g1,g-2)
    c: Distance(g0,g-1) = 6
    c: DistanceX(g0,g1) = 46
    c: Equal(g3,g0)
    c: Equal(g0,g2)
    c: Coincident(g4,g0)
    c: Coincident(g4,g3)
    c: Vertical(g4)
    c: Coincident(g5,g2)
    c: Coincident(g5,g1)
    c: Vertical(g5)
    c: Coincident(g6,g3)
    c: Coincident(g6,g2)
    c: Horizontal(g6)
    c: DistanceY(g0,g3) = 13
FEATURE [PartDesign::Pad] Pad036
  Direction = (0,0,1)
  Length = 25
  Length2 = 10
  Profile = -> Sketch044 [Edge8,Edge7,Edge6,Edge5,Edge4,Edge3,Edge2,Edge1,Edge15,Vertex13,Edge14,Edge13,Edge12,Edge16]
  ReferenceAxis = -> Sketch044 [N_Axis]
  Refine = true
  Suppressed = false
  Type = 0
FEATURE [PartDesign::Pocket] Pocket005
  BaseFeature = -> Pad036
  Direction = (0,-1,2e-16)
  Length = 5
  Length2 = 5
  Profile = -> Sketch045
  ReferenceAxis = -> Sketch045 [N_Axis]
  Refine = true
  Suppressed = false
  Type = 1
FEATURE [PartDesign::Pad] Pad037
  BaseFeature = -> Pocket005
  Direction = (0,0,1)
  Length = 5
  Length2 = 10
  Profile = -> Sketch044 [Edge9,Edge11,Edge16,Edge10,Edge4,Edge5,Edge6]
  ReferenceAxis = -> Sketch044 [N_Axis]
  Refine = true
  Reversed = true
  Suppressed = false
  Type = 0
FEATURE [PartDesign::Body] Body093  label="BK10"
  AllowCompound = false
  Group = -> [Sketch044,Sketch045,Pad036,Pocket005,Pad037]
  Origin = -> Origin099
  Tip = -> Pad037
FEATURE [PartDesign::FeatureBase] Clone060
  BaseFeature = -> Body093
  Suppressed = false
FEATURE [PartDesign::Body] Body094  label="bk10"
  AllowCompound = false
  Group = -> [Clone060]
  Origin = -> Origin100
  Placement = pos=(-285,-104.7,62.22) rot=(1,0,0;1.5708rad)
  Tip = -> Clone060
FEATURE [PartDesign::FeatureBase] Clone061
  BaseFeature = -> Body018
  Suppressed = false
FEATURE [PartDesign::Body] Body095  label="bf10"
  AllowCompound = false
  Group = -> [Clone061]
  Origin = -> Origin101
  Placement = pos=(-285,-580,62.22) rot=(1,0,0;1.5708rad)
  Tip = -> Clone061
FEATURE [Sketcher::SketchObject] Sketch046
  ArcFitTolerance = 1e-06
  AttachmentSupport = -> [XZ_Plane102]
  FullyConstrained = true
  MakeInternals = false
  MapMode = 5
  Placement = pos=(0,0,0) rot=(1,0,0;1.5708rad)
  sketch-geometry (14):
    g0: LineSegment StartX=-25 StartY=-15 StartZ=0 EndX=25 EndY=-15 EndZ=0
    g1: LineSegment StartX=25 StartY=-15 StartZ=0 EndX=25 EndY=15 EndZ=0
    g2: LineSegment StartX=25 StartY=15 StartZ=0 EndX=-25 EndY=15 EndZ=0
    g3: LineSegment StartX=-25 StartY=15 StartZ=0 EndX=-25 EndY=-15 EndZ=0
    g4: Circle CenterX=0 CenterY=0 CenterZ=0 NormalX=0 NormalY=0 NormalZ=1 AngleXU=0 Radius=11
    g5: Circle [constr] CenterX=0 CenterY=0 CenterZ=0 NormalX=0 NormalY=0 NormalZ=1 AngleXU=0 Radius=16
    g6: Circle CenterX=16 CenterY=0 CenterZ=0 NormalX=0 NormalY=0 NormalZ=1 AngleXU=0 Radius=2
    g7: Circle CenterX=11.3137 CenterY=11.3137 CenterZ=0 NormalX=0 NormalY=0 NormalZ=1 AngleXU=0 Radius=2
    g8: Circle CenterX=11.3137 CenterY=-11.3137 CenterZ=0 NormalX=0 NormalY=0 NormalZ=1 AngleXU=0 Radius=2
    g9: Circle CenterX=-11.3137 CenterY=11.3137 CenterZ=0 NormalX=0 NormalY=0 NormalZ=1 AngleXU=0 Radius=2
    g10: Circle CenterX=-16 CenterY=0 CenterZ=0 NormalX=0 NormalY=0 NormalZ=1 AngleXU=0 Radius=2
    g11: Circle CenterX=-11.3137 CenterY=-11.3137 CenterZ=0 NormalX=0 NormalY=0 NormalZ=1 AngleXU=0 Radius=2
    g12: LineSegment [constr] StartX=-11.3137 StartY=11.3137 StartZ=0 EndX=11.3137 EndY=-11.3137 EndZ=0
    g13: LineSegment [constr] StartX=-11.3137 StartY=-11.3137 StartZ=0 EndX=11.3137 EndY=11.3137 EndZ=0
  constraints (36):
    c: Coincident(g0,g1)
    c: Coincident(g1,g2)
    c: Coincident(g2,g3)
    c: Coincident(g3,g0)
    c: Horizontal(g0)
    c: Vertical(g3)
    c: DistanceY(g1,g1) = 30
    c: DistanceX(g2,g2) = 50
    c: Symmetric(g2,g1,g-2)
    c: Symmetric(g1,g0,g-1)
    c: Coincident(g4,g-1)
    c: Diameter(g4) = 22
    c: Coincident(g5,g4)
    c: Diameter(g5) = 32
    c: PointOnObject(g6,g5)
    c: PointOnObject(g7,g5)
    c: PointOnObject(g8,g5)
    c: PointOnObject(g9,g5)
    c: PointOnObject(g11,g5)
    c: Equal(g11,g10)
    c: Equal(g10,g9)
    c: Equal(g9,g7)
    c: Equal(g7,g6)
    c: Equal(g6,g8)
    c: PointOnObject(g6,g-1)
    c: PointOnObject(g10,g-1)
    c: Coincident(g12,g9)
    c: Coincident(g12,g8)
    c: Coincident(g13,g11)
    c: Coincident(g13,g7)
    c: Angle(g13,g12) = 1.5708
    c: Angle(g12,g-1) = 0.785398
    c: PointOnObject(g4,g13)
    c: PointOnObject(g4,g12)
    c: Diameter(g9) = 4
    c: PointOnObject(g10,g5)
FEATURE [PartDesign::Pad] Pad038
  Direction = (0,-1,2e-16)
  Length = 36
  Length2 = 10
  Placement = pos=(0,0,0) rot=(1,0,0;1.5708rad)
  Profile = -> Sketch046 [Edge3,Edge4,Edge1,Edge2,Edge5]
  ReferenceAxis = -> Sketch046 [N_Axis]
  Refine = true
  Suppressed = false
  Type = 0
FEATURE [PartDesign::Pocket] Pocket006
  BaseFeature = -> Pad038
  Direction = (0,1,-2e-16)
  Length = 12
  Length2 = 5
  Placement = pos=(0,0,0) rot=(1,0,0;1.5708rad)
  Profile = -> Sketch046 [Edge9,Edge10,Edge11,Edge8,Vertex6,Edge7,Edge6]
  ReferenceAxis = -> Sketch046 [N_Axis]
  Refine = true
  Reversed = true
  Suppressed = false
  Type = 0
FEATURE [Sketcher::SketchObject] Sketch047
  ArcFitTolerance = 1e-06
  AttachmentSupport = -> [Pocket006]
  FullyConstrained = true
  MakeInternals = false
  MapMode = 5
  Placement = pos=(0,6.6e-15,15) rot=(0,0,1;3.14159rad)
  sketch-geometry (8):
    g0: LineSegment [constr] StartX=-17.5 StartY=30 StartZ=0 EndX=-17.5 EndY=6 EndZ=0
    g1: LineSegment [constr] StartX=-17.5 StartY=6 StartZ=0 EndX=17.5 EndY=6 EndZ=0
    g2: LineSegment [constr] StartX=17.5 StartY=6 StartZ=0 EndX=17.5 EndY=30 EndZ=0
    g3: LineSegment [constr] StartX=17.5 StartY=30 StartZ=0 EndX=-17.5 EndY=30 EndZ=0
    g4: Circle CenterX=17.5 CenterY=30 CenterZ=0 NormalX=0 NormalY=0 NormalZ=1 AngleXU=0 Radius=2.5
    g5: Circle CenterX=17.5 CenterY=6 CenterZ=0 NormalX=0 NormalY=0 NormalZ=1 AngleXU=0 Radius=2.5
    g6: Circle CenterX=-17.5 CenterY=6 CenterZ=0 NormalX=0 NormalY=0 NormalZ=1 AngleXU=0 Radius=2.5
    g7: Circle CenterX=-17.5 CenterY=30 CenterZ=0 NormalX=0 NormalY=0 NormalZ=1 AngleXU=0 Radius=2.5
  constraints (19):
    c: Coincident(g0,g1)
    c: Coincident(g1,g2)
    c: Coincident(g2,g3)
    c: Coincident(g3,g0)
    c: Vertical(g0)
    c: Vertical(g2)
    c: Horizontal(g3)
    c: Symmetric(g0,g1,g-2)
    c: DistanceY(g0,g0) = 24
    c: DistanceX(g1,g1) = 35
    c: Coincident(g4,g2)
    c: Coincident(g5,g1)
    c: Coincident(g6,g0)
    c: Coincident(g7,g0)
    c: Equal(g7,g4)
    c: Equal(g4,g5)
    c: Equal(g5,g6)
    c: Diameter(g7) = 5
    c: Distance(g-1,g1) = 6
FEATURE [PartDesign::Pocket] Pocket007
  BaseFeature = -> Pocket006
  Direction = (0,0,-1)
  Length = 12
  Length2 = 5
  Placement = pos=(0,0,0) rot=(1,0,0;1.5708rad)
  Profile = -> Sketch047
  ReferenceAxis = -> Sketch047 [N_Axis]
  Refine = true
  Suppressed = false
  Type = 0
FEATURE [PartDesign::Body] Body096  label="dsg12h"
  AllowCompound = false
  Group = -> [Sketch046,Pad038,Pocket006,Sketch047,Pocket007]
  Origin = -> Origin102
  Tip = -> Pocket007
FEATURE [PartDesign::FeatureBase] Clone062
  BaseFeature = -> Body096
  Suppressed = false
FEATURE [PartDesign::Body] Body097  label="dsg12h001"
  AllowCompound = false
  Group = -> [Clone062]
  Origin = -> Origin103
  Placement = pos=(-285,-287,48.2) rot=(0,0,1;0rad)
  Tip = -> Clone062
FEATURE [PartDesign::Pad] Pad039
  Direction = (0,0,1)
  Length = 12.7
  Length2 = 10
  Profile = -> Sketch032 [Edge14,Edge16,Edge4,Edge3,Edge1,Edge2,Edge31,Edge27,Edge28,Edge30,Edge29,Edge26,Edge25,Edge38,Edge37,Edge36,Edge35,Edge34,Edge33,Edge32,Edge20,Edge18,Edge17,Edge19,Edge13,Edge15,Edge6,Edge5,Edge7,Edge8,Edge21,Edge22,Edge23,Edge24,Edge9,Edge10,Edge12,Edge11]
  ReferenceAxis = -> Sketch032 [N_Axis]
  Refine = true
  Reversed = true
  Suppressed = false
  Type = 0
FEATURE [PartDesign::Pocket] Pocket008
  BaseFeature = -> Pad039
  Direction = (0,0,-1)
  Length = 8.7
  Length2 = 5
  Profile = -> Sketch032 [Edge52,Edge51,Edge53,Edge54,Edge50,Edge49,Edge47,Edge48,Edge44,Edge43,Edge45,Edge46,Edge41,Vertex40,Edge39,Edge42,Edge40]
  ReferenceAxis = -> Sketch032 [N_Axis]
  Refine = true
  Suppressed = false
  Type = 0
FEATURE [PartDesign::Pocket] Pocket009
  BaseFeature = -> Pocket008
  Direction = (0,0,-1)
  Length = 7.5
  Length2 = 5
  Profile = -> Sketch032 [Edge56,Edge57,Edge55,Edge58]
  ReferenceAxis = -> Sketch032 [N_Axis]
  Refine = true
  Suppressed = false
  Type = 0
FEATURE [PartDesign::Body] Body044  label="X gantry plate"
  AllowCompound = false
  Group = -> [Sketch032,Pad039,Pocket008,Pocket009]
  Origin = -> Origin049
  Tip = -> Pocket009
FEATURE [PartDesign::FeatureBase] Clone022
  BaseFeature = -> Body044
  Suppressed = false
FEATURE [PartDesign::Body] Body045  label="X gantry plate001"
  AllowCompound = false
  Group = -> [Clone022]
  Origin = -> Origin050
  Placement = pos=(-285,-305,92.7) rot=(0,0,1;1.5708rad)
  Tip = -> Clone022
  expr: .Placement.Base.y = -305 mm + Group001.Base_x_coord
FEATURE [TechDraw::DrawProjGroupItem] View001  label="EDGEWISE"
  CoarseView = false
  Direction = (0,1,0)
  Focus = 100
  HardHidden = false
  IsoCount = 0
  IsoHidden = false
  IsoVisible = false
  LockPosition = false
  Perspective = false
  Rotation = 0
  RotationVector = (1,0,0)
  Scale = 0.33
  ScaleType = 0
  ScrubCount = 1
  SeamHidden = false
  SeamVisible = false
  SmoothHidden = false
  SmoothVisible = true
  Source = -> [Body044]
  Type = 0
  X = 61.2691
  XDirection = (1e-16,0,1)
  Y = 135.222
FEATURE [TechDraw::DrawViewDimension] Dimension006
  AngleOverride = false
  Arbitrary = false
  ArbitraryTolerances = false
  BoxCorners = (2) [(-2.0955,-50.292,0),(2.0955,50.292,0)]
  EqualTolerance = true
  ExtensionAngle = 0
  FormatSpec = %.2w
  FormatSpecOverTolerance = %+.2w
  FormatSpecUnderTolerance = %+.2w
  Inverted = false
  LineAngle = 0
  LockPosition = false
  MeasureType = 1
  OverTolerance = 0
  References2D = -> [View001]
  Rotation = 0
  Scale = 0.33
  ScaleType = 0
  TheoreticalExact = false
  Type = 0
  UnderTolerance = 0
  X = -8.0927
  Y = 45.1758
FEATURE [TechDraw::DrawProjGroupItem] View004  label="ISOMETRIC"
  Caption = ISOMETRIC
  CoarseView = false
  Direction = (0.409575,-0.709407,0.573577)
  Focus = 100
  HardHidden = false
  IsoCount = 0
  IsoHidden = false
  IsoVisible = false
  LockPosition = false
  Perspective = false
  Rotation = 0
  RotationVector = (1,0,0)
  Scale = 0.5
  ScaleType = 2
  ScrubCount = 1
  SeamHidden = false
  SeamVisible = false
  SmoothHidden = false
  SmoothVisible = true
  Source = -> [Pad019]
  Type = 0
  X = 63.348
  XDirection = (0.866026,0.499999,4.05816e-07)
  Y = 171.722
FEATURE [TechDraw::DrawProjGroupItem] View003  label=" EDGEWISE "
  Caption = EDGEWISE
  CoarseView = false
  Direction = (0,-1,0)
  Focus = 100
  HardHidden = false
  IsoCount = 0
  IsoHidden = false
  IsoVisible = false
  LockPosition = false
  Perspective = false
  Rotation = 0
  RotationVector = (1,0,0)
  ScaleType = 0
  ScrubCount = 1
  SeamHidden = false
  SeamVisible = false
  SmoothHidden = false
  SmoothVisible = true
  Source = -> [Body019]
  Type = 0
  X = 120.349
  XDirection = (1e-16,0,-1)
  Y = 132.736
FEATURE [PartDesign::Pad] Pad008
  Direction = (0,0,1)
  Length = 12.7
  Length2 = 10
  Profile = -> Sketch013 [Edge13,Edge4,Edge3,Edge14,Edge16,Edge15,Edge6,Edge5,Edge7,Edge8,Edge1,Edge2,Edge12,Edge10,Edge9,Edge11,Edge17,Edge19,Edge20,Edge18,Edge24,Edge21,Edge23,Edge22]
  ReferenceAxis = -> Sketch013 [N_Axis]
  Refine = true
  Reversed = true
  Suppressed = false
  Type = 0
FEATURE [PartDesign::Pocket] Pocket010
  BaseFeature = -> Pad008
  Direction = (0,0,-1)
  Length = 8.7
  Length2 = 5
  Profile = -> Sketch013 [Edge25,Edge28,Edge27,Edge26,Edge40,Edge39,Edge37,Edge38,Edge36,Edge33,Edge34,Edge35,Edge31,Edge32,Edge30,Edge29]
  ReferenceAxis = -> Sketch013 [N_Axis]
  Refine = true
  Suppressed = false
  Type = 0
FEATURE [PartDesign::Pocket] Pocket011
  BaseFeature = -> Pocket010
  Direction = (0,0,-1)
  Length = 7.5
  Length2 = 5
  Profile = -> Sketch013 [Edge44,Edge43,Edge41,Edge42]
  ReferenceAxis = -> Sketch013 [N_Axis]
  Refine = true
  Suppressed = false
  Type = 0
FEATURE [PartDesign::Body] Body008  label="XY gantry plate"
  AllowCompound = false
  Group = -> [Sketch013,Pad008,Pocket010,Pocket011]
  Origin = -> Origin010
  Tip = -> Pocket011
FEATURE [PartDesign::FeatureBase] Clone047
  BaseFeature = -> Body008
  Suppressed = false
FEATURE [PartDesign::Body] Body079  label="y gantry plate"
  AllowCompound = false
  Group = -> [Clone047]
  Origin = -> Origin085
  Placement = pos=(-285,-305,165.4) rot=(0,0,1;0rad)
  Tip = -> Clone047
  expr: .Placement.Base.x = -285 mm + Group001.Base_y_coord
  expr: .Placement.Base.y = -305 mm + Group001.Base_x_coord
FEATURE [TechDraw::DrawSVGTemplate] Template003
  EditableTexts = approval_person=A.F.; creator=MATTHEW DIPALMA; date_of_issue=11/30/2024; document_status=RELEASED; document_type=DETAIL DRAWING; drawing_number=00001-003; general_tolerances=ISO 2768-c; language_code=EN; legal_owner_1=MARIAN; legal_owner_2=ELECTROMAGNETICS; legal_owner_3=BRIDGEPORT, CT; legal_owner_4=06606; part_material=ALUMINUM 6061; responsible_department=MECH ENG; revision_index=AAA; sheet_number=1 / 1; sheet_scale=1 : 3; supplementary_title_1=Y LINEAR MOTION ASSEMBLY; supplementary_title_2=CNC; title=Y GANTRY PLATE
  Height = 210
  Orientation = 1
  Template = <path>
  Width = 297
FEATURE [TechDraw::DrawViewAnnotation] Annotation002
  Font = osifont
  LineSpace = 100
  LockPosition = false
  MaxWidth = -1
  Rotation = 0
  ScaleType = 0
  Text = 1. PART INTENDED TO BE PRODUCED FROM | 12x12x0.5" ALUMINUM PLATE STOCK. | 2. DEBURR ALL SHARP EDGES. | 3. ALL DIMENSIONS TYPICAL. | 4. HOLE REPROCESSING PERMITTED FOR | FUNCTION AT NEXT HIGHER ASSEMBLY.
  TextSize = 3
  TextStyle = 0
  X = 63.5776
  Y = 36.5833
FEATURE [TechDraw::DrawProjGroupItem] View005  label="Front"
  CoarseView = false
  Direction = (0,0,1)
  Focus = 100
  HardHidden = false
  IsoCount = 0
  IsoHidden = false
  IsoVisible = false
  LockPosition = true
  Perspective = false
  Rotation = 0
  RotationVector = (1,0,0)
  Scale = 0.333333
  ScaleType = 2
  ScrubCount = 1
  SeamHidden = false
  SeamVisible = false
  SmoothHidden = false
  SmoothVisible = true
  Source = -> [Body008]
  Type = 0
  X = 0
  XDirection = (1,0,0)
  Y = 0
FEATURE [TechDraw::DrawProjGroupItem] ProjItem  label="Right"
  CoarseView = false
  Direction = (1,0,1e-16)
  Focus = 100
  HardHidden = false
  IsoCount = 0
  IsoHidden = false
  IsoVisible = false
  LockPosition = false
  Perspective = false
  Rotation = 0
  RotationVector = (1,0,0)
  ScaleType = 0
  ScrubCount = 1
  SeamHidden = false
  SeamVisible = false
  SmoothHidden = false
  SmoothVisible = true
  Source = -> [Body008]
  Type = 2
  X = -67.9166
  XDirection = (1e-16,0,-1)
  Y = 0
FEATURE [TechDraw::DrawProjGroup] ProjGroup
  Anchor = -> View005
  AutoDistribute = true
  LockPosition = false
  ProjectionType = 0
  Rotation = 0
  Scale = 0.333333
  ScaleType = 2
  Source = -> [Body008]
  Views = -> [View005,ProjItem]
  X = 206.222
  Y = 135.934
  spacingX = 15
  spacingY = 15
FEATURE [TechDraw::DrawProjGroupItem] View006  label="View"
  CoarseView = false
  Direction = (0.57735,-0.57735,0.57735)
  Focus = 100
  HardHidden = false
  IsoCount = 0
  IsoHidden = false
  IsoVisible = false
  LockPosition = false
  Perspective = false
  Rotation = 0
  RotationVector = (0.707107,0.707107,0)
  Scale = 0.2
  ScaleType = 2
  ScrubCount = 1
  SeamHidden = false
  SeamVisible = false
  SmoothHidden = false
  SmoothVisible = true
  Source = -> [Body008]
  Type = 0
  X = 73.3561
  XDirection = (0.707107,0.707107,0)
  Y = 163.237
FEATURE [TechDraw::DrawViewBalloon] Balloon007
  BubbleShape = 1
  EndType = 0
  EndTypeScale = 1
  KinkLength = 5
  LockPosition = false
  OriginX = 1.04144
  OriginY = -172.399
  Rotation = 0
  ScaleType = 0
  ShapeScale = 1
  SourceView = -> View005
  Text = PLANFORM
  TextWrapLen = -1
  X = 1.03205
  Y = -174.644
FEATURE [TechDraw::DrawViewBalloon] Balloon008
  BubbleShape = 1
  EndType = 0
  EndTypeScale = 1
  KinkLength = 5
  LockPosition = false
  OriginX = -4.89994
  OriginY = -176.065
  Rotation = 0
  ScaleType = 0
  ShapeScale = 1
  SourceView = -> ProjItem
  Text = EDGEWISE
  TextWrapLen = -1
  X = 2.53862
  Y = -175.916
FEATURE [TechDraw::DrawViewBalloon] Balloon009
  BubbleShape = 1
  EndType = 0
  EndTypeScale = 1
  KinkLength = 5
  LockPosition = false
  OriginX = 4.70067
  OriginY = -172.205
  Rotation = 0
  ScaleType = 0
  ShapeScale = 1
  SourceView = -> View006
  Text = ISOMETRIC
  TextWrapLen = -1
  X = 1.36222
  Y = -165.075
FEATURE [TechDraw::DrawViewDimension] Dimension038
  AngleOverride = false
  Arbitrary = false
  ArbitraryTolerances = false
  BoxCorners = (2) [(-50.7999,-50.7999,0),(50.7999,50.7999,0)]
  EqualTolerance = true
  ExtensionAngle = 0
  FormatSpec = %.2w
  FormatSpecOverTolerance = %+.2w
  FormatSpecUnderTolerance = %+.2w
  Inverted = false
  LineAngle = 0
  LockPosition = false
  MeasureType = 1
  OverTolerance = 5
  References2D = -> [View005]
  Rotation = 0
  ScaleType = 0
  TheoreticalExact = false
  Type = 1
  UnderTolerance = -5
  X = 0
  Y = 57.3214
FEATURE [TechDraw::DrawViewDimension] Dimension039
  AngleOverride = false
  Arbitrary = false
  ArbitraryTolerances = false
  BoxCorners = (2) [(-2.11666,-50.7999,0),(2.11666,50.7999,0)]
  EqualTolerance = true
  ExtensionAngle = 0
  FormatSpec = %.2w
  FormatSpecOverTolerance = %+.2w
  FormatSpecUnderTolerance = %+.2w
  Inverted = false
  LineAngle = 0
  LockPosition = false
  MeasureType = 1
  OverTolerance = 5
  References2D = -> [ProjItem]
  Rotation = 0
  ScaleType = 0
  TheoreticalExact = false
  Type = 2
  UnderTolerance = -5
  X = -8.91547
  Y = 0
FEATURE [TechDraw::DrawViewDimension] Dimension040
  AngleOverride = false
  Arbitrary = false
  ArbitraryTolerances = false
  BoxCorners = (2) [(-2.11666,-50.7999,0),(2.11666,50.7999,0)]
  EqualTolerance = true
  ExtensionAngle = 0
  FormatSpec = %.2w
  FormatSpecOverTolerance = %+.2w
  FormatSpecUnderTolerance = %+.2w
  Inverted = false
  LineAngle = 0
  LockPosition = false
  MeasureType = 1
  OverTolerance = 0
  References2D = -> [ProjItem]
  Rotation = 0
  ScaleType = 0
  TheoreticalExact = false
  Type = 0
  UnderTolerance = 0
  X = 10.0047
  Y = 37.2041
FEATURE [TechDraw::DrawViewDimension] Dimension041
  AngleOverride = false
  Arbitrary = false
  ArbitraryTolerances = false
  BoxCorners = (2) [(-50.7999,-50.7999,0),(50.7999,50.7999,0)]
  EqualTolerance = true
  ExtensionAngle = 0
  FormatSpec = %.2w
  FormatSpecOverTolerance = %+.2w
  FormatSpecUnderTolerance = %+.2w
  Inverted = false
  LineAngle = 0
  LockPosition = false
  MeasureType = 1
  OverTolerance = 0
  References2D = -> [View005]
  Rotation = 0
  ScaleType = 0
  TheoreticalExact = false
  Type = 0
  UnderTolerance = 0
  X = -12.9472
  Y = 1.96745
FEATURE [TechDraw::DrawViewDimension] Dimension042
  AngleOverride = false
  Arbitrary = false
  ArbitraryTolerances = false
  BoxCorners = (2) [(-50.7999,-50.7999,0),(50.7999,50.7999,0)]
  EqualTolerance = true
  ExtensionAngle = 0
  FormatSpec = %.2w
  FormatSpecOverTolerance = %+.2w
  FormatSpecUnderTolerance = %+.2w
  Inverted = false
  LineAngle = 0
  LockPosition = false
  MeasureType = 1
  OverTolerance = 0
  References2D = -> [View005]
  Rotation = 0
  ScaleType = 0
  TheoreticalExact = false
  Type = 0
  UnderTolerance = 0
  X = -3.99705
  Y = 12.0434
FEATURE [TechDraw::DrawViewDimension] Dimension043
  AngleOverride = false
  Arbitrary = false
  ArbitraryTolerances = false
  BoxCorners = (2) [(-50.7999,-50.7999,0),(50.7999,50.7999,0)]
  EqualTolerance = true
  ExtensionAngle = 0
  FormatSpec = %.2w
  FormatSpecOverTolerance = %+.2w
  FormatSpecUnderTolerance = %+.2w
  Inverted = false
  LineAngle = 0
  LockPosition = false
  MeasureType = 1
  OverTolerance = 0
  References2D = -> [View005]
  Rotation = 0
  ScaleType = 0
  TheoreticalExact = false
  Type = 0
  UnderTolerance = 0
  X = 26.6666
  Y = 47.2233
FEATURE [TechDraw::DrawViewDimension] Dimension044
  AngleOverride = false
  Arbitrary = false
  ArbitraryTolerances = false
  BoxCorners = (2) [(-50.7999,-50.7999,0),(50.7999,50.7999,0)]
  EqualTolerance = true
  ExtensionAngle = 0
  FormatSpec = %.2w
  FormatSpecOverTolerance = %+.2w
  FormatSpecUnderTolerance = %+.2w
  Inverted = false
  LineAngle = 0
  LockPosition = false
  MeasureType = 1
  OverTolerance = 0
  References2D = -> [View005]
  Rotation = 0
  ScaleType = 0
  TheoreticalExact = false
  Type = 0
  UnderTolerance = 0
  X = 39.47
  Y = 33.3333
FEATURE [TechDraw::DrawViewAnnotation] Annotation003
  Font = osifont
  LineSpace = 100
  LockPosition = false
  MaxWidth = -1
  Rotation = 0
  ScaleType = 0
  Text = SCALE 1:5
  TextSize = 4
  TextStyle = 0
  X = 73.3561
  Y = 124.864
FEATURE [TechDraw::DrawViewDimension] Dimension045
  AngleOverride = false
  Arbitrary = false
  ArbitraryTolerances = false
  BoxCorners = (2) [(-50.7999,-50.7999,0),(50.7999,50.7999,0)]
  EqualTolerance = true
  ExtensionAngle = 0
  FormatSpec = %.2w
  FormatSpecOverTolerance = %+.2w
  FormatSpecUnderTolerance = %+.2w
  Inverted = false
  LineAngle = 0
  LockPosition = false
  MeasureType = 1
  OverTolerance = 0
  References2D = -> [View005]
  Rotation = 0
  ScaleType = 0
  TheoreticalExact = false
  Type = 0
  UnderTolerance = 0
  X = -41.7333
  Y = 29.3994
FEATURE [TechDraw::DrawViewDimension] Dimension046
  AngleOverride = false
  Arbitrary = false
  ArbitraryTolerances = false
  BoxCorners = (2) [(-50.7999,-50.7999,0),(50.7999,50.7999,0)]
  EqualTolerance = true
  ExtensionAngle = 0
  FormatSpec = %.2w
  FormatSpecOverTolerance = %+.2w
  FormatSpecUnderTolerance = %+.2w
  Inverted = false
  LineAngle = 0
  LockPosition = false
  MeasureType = 1
  OverTolerance = 0
  References2D = -> [View005]
  Rotation = 0
  ScaleType = 0
  TheoreticalExact = false
  Type = 0
  UnderTolerance = 0
  X = -42.5261
  Y = 44.7333
FEATURE [TechDraw::DrawViewDimension] Dimension047
  AngleOverride = false
  Arbitrary = false
  ArbitraryTolerances = false
  BoxCorners = (2) [(-50.7999,-50.7999,0),(50.7999,50.7999,0)]
  EqualTolerance = true
  ExtensionAngle = 0
  FormatSpec = %.2w
  FormatSpecOverTolerance = %+.2w
  FormatSpecUnderTolerance = %+.2w
  Inverted = false
  LineAngle = 0
  LockPosition = false
  MeasureType = 1
  OverTolerance = 0
  References2D = -> [View005]
  Rotation = 0
  ScaleType = 0
  TheoreticalExact = false
  Type = 0
  UnderTolerance = 0
  X = -29.8962
  Y = 5.33333
FEATURE [TechDraw::DrawSVGTemplate] Template002
  EditableTexts = approval_person=M. REMARK; creator=M. DIPALMA; date_of_issue=11/28/2024; document_status=DRAFT; document_type=DETAIL DRAWING; drawing_number=00001-002; general_tolerances=ISO 2768-c; language_code=EN; legal_owner_1=MARIAN; legal_owner_2=ELECTROMAGNETICS; legal_owner_3=BRIDGEPORT, CT; legal_owner_4=06606; part_material=ALUMINUM 6061; responsible_department=MECH ENG; revision_index=AAA; sheet_number=1 / 1; sheet_scale=1 : 1; supplementary_title_1=PLATE TO HGR20CA; supplementary_title_2=CNC; title=SPACER
  Height = 210
  Orientation = 1
  Template = <path>
  Width = 297
FEATURE [TechDraw::DrawPage] Page002  label="drawing template"
  KeepUpdated = true
  NextBalloonIndex = 1
  ProjectionType = 0
  Template = -> Template002
FEATURE [TechDraw::DrawProjGroupItem] View002  label=" PLANFORM "
  Caption = PLANFORM
  CoarseView = false
  Direction = (0,0,1)
  Focus = 100
  HardHidden = false
  IsoCount = 0
  IsoHidden = false
  IsoVisible = false
  LockPosition = false
  Perspective = false
  Rotation = 0
  RotationVector = (1,0,0)
  ScaleType = 0
  ScrubCount = 1
  SeamHidden = false
  SeamVisible = false
  SmoothHidden = false
  SmoothVisible = true
  Source = -> [Body019]
  Type = 0
  X = 201.155
  XDirection = (1e-16,-1,0)
  Y = 132.736
FEATURE [TechDraw::DrawViewDimension] Dimension030
  AngleOverride = false
  Arbitrary = false
  ArbitraryTolerances = false
  BoxCorners = (2) [(-36.5,-25,0),(36.5,25,0)]
  EqualTolerance = true
  ExtensionAngle = 0
  FormatSpec = %.2w
  FormatSpecOverTolerance = %+.2w
  FormatSpecUnderTolerance = %+.2w
  Inverted = false
  LineAngle = 0
  LockPosition = false
  MeasureType = 1
  OverTolerance = 2
  References2D = -> [View002]
  Rotation = 0
  ScaleType = 0
  TheoreticalExact = false
  Type = 0
  UnderTolerance = -2
  X = 0
  Y = 35.262
FEATURE [TechDraw::DrawViewDimension] Dimension031
  AngleOverride = false
  Arbitrary = false
  ArbitraryTolerances = false
  BoxCorners = (2) [(-36.5,-25,0),(36.5,25,0)]
  EqualTolerance = true
  ExtensionAngle = 0
  FormatSpec = %.2w
  FormatSpecOverTolerance = %+.2w
  FormatSpecUnderTolerance = %+.2w
  Inverted = false
  LineAngle = 0
  LockPosition = false
  MeasureType = 1
  OverTolerance = 2
  References2D = -> [View002]
  Rotation = 0
  ScaleType = 0
  TheoreticalExact = false
  Type = 0
  UnderTolerance = -2
  X = -46.3034
  Y = 0
FEATURE [TechDraw::DrawViewDimension] Dimension032
  AngleOverride = false
  Arbitrary = false
  ArbitraryTolerances = false
  BoxCorners = (2) [(-36.5,-25,0),(36.5,25,0)]
  EqualTolerance = true
  ExtensionAngle = 0
  FormatSpec = 4X ⌀%.2w THRU
  FormatSpecOverTolerance = %+.2w
  FormatSpecUnderTolerance = %+.2w
  Inverted = false
  LineAngle = 0
  LockPosition = false
  MeasureType = 1
  OverTolerance = 0
  References2D = -> [View002]
  Rotation = 0
  ScaleType = 0
  TheoreticalExact = false
  Type = 5
  UnderTolerance = 0
  X = 59.698
  Y = 20.4028
FEATURE [TechDraw::DrawViewDimension] Dimension034
  AngleOverride = false
  Arbitrary = false
  ArbitraryTolerances = false
  BoxCorners = (2) [(-36.5,-25,0),(36.5,25,0)]
  EqualTolerance = true
  ExtensionAngle = 0
  FormatSpec = %.2w
  FormatSpecOverTolerance = %+.2w
  FormatSpecUnderTolerance = %+.2w
  Inverted = false
  LineAngle = 0
  LockPosition = false
  MeasureType = 1
  OverTolerance = 0
  References2D = -> [View002]
  Rotation = 0
  ScaleType = 0
  TheoreticalExact = false
  Type = 0
  UnderTolerance = 0
  X = -27.25
  Y = 7.90411
FEATURE [TechDraw::DrawViewDimension] Dimension035
  AngleOverride = false
  Arbitrary = false
  ArbitraryTolerances = false
  BoxCorners = (2) [(-36.5,-25,0),(36.5,25,0)]
  EqualTolerance = true
  ExtensionAngle = 0
  FormatSpec = %.2w
  FormatSpecOverTolerance = %+.2w
  FormatSpecUnderTolerance = %+.2w
  Inverted = false
  LineAngle = 0
  LockPosition = false
  MeasureType = 1
  OverTolerance = 0
  References2D = -> [View002]
  Rotation = 0
  ScaleType = 0
  TheoreticalExact = false
  Type = 0
  UnderTolerance = 0
  X = -29.7855
  Y = 20.5
FEATURE [TechDraw::DrawViewDimension] Dimension036
  AngleOverride = false
  Arbitrary = false
  ArbitraryTolerances = false
  BoxCorners = (2) [(-36.5,-25,0),(36.5,25,0)]
  EqualTolerance = true
  ExtensionAngle = 0
  FormatSpec = %.2w
  FormatSpecOverTolerance = %+.2w
  FormatSpecUnderTolerance = %+.2w
  Inverted = false
  LineAngle = 0
  LockPosition = false
  MeasureType = 1
  OverTolerance = 0
  References2D = -> [View002]
  Rotation = 0
  ScaleType = 0
  TheoreticalExact = false
  Type = 0
  UnderTolerance = 0
  X = 5.36034
  Y = 5.15099
FEATURE [TechDraw::DrawViewDimension] Dimension037
  AngleOverride = false
  Arbitrary = false
  ArbitraryTolerances = false
  BoxCorners = (2) [(-36.5,-25,0),(36.5,25,0)]
  EqualTolerance = true
  ExtensionAngle = 0
  FormatSpec = %.2w
  FormatSpecOverTolerance = %+.2w
  FormatSpecUnderTolerance = %+.2w
  Inverted = false
  LineAngle = 0
  LockPosition = false
  MeasureType = 1
  OverTolerance = 0
  References2D = -> [View002]
  Rotation = 0
  ScaleType = 0
  TheoreticalExact = false
  Type = 0
  UnderTolerance = 0
  X = 0
  Y = -6.74958
FEATURE [TechDraw::DrawViewAnnotation] Annotation001
  Font = osifont
  LineSpace = 100
  LockPosition = false
  MaxWidth = -1
  Rotation = 0
  ScaleType = 0
  Text = 1. PART INTENDED TO BE PRODUCED FROM | 30MMx2" ALUMINUM BAR STOCK. | 2. DEBURR ALL SHARP EDGES. | 3. ALL DIMENSIONS TYPICAL. | 4. HOLE REPROCESSING PERMITTED FOR | FUNCTION AT NEXT HIGHER ASSEMBLY.
  TextSize = 3
  TextStyle = 0
  X = 63.348
  Y = 36.3537
FEATURE [TechDraw::DrawSVGTemplate] Template001
  EditableTexts = approval_person=A.F.; creator=MATTHEW DIPALMA; date_of_issue=11/28/2024; document_status=RELEASED; document_type=DETAIL DRAWING; drawing_number=00001-002; general_tolerances=ISO 2768-c; language_code=EN; legal_owner_1=MARIAN; legal_owner_2=ELECTROMAGNETICS; legal_owner_3=BRIDGEPORT, CT; legal_owner_4=06606; part_material=ALUMINUM 6061; responsible_department=MECH ENG; revision_index=AAB; sheet_number=1 / 1; sheet_scale=1 : 1; supplementary_title_1=ALL PLATES TO HGR20CA; supplementary_title_2=CNC; title=SPACER
  Height = 210
  Orientation = 1
  Template = <path>
  Width = 297
FEATURE [TechDraw::DrawProjGroupItem] View  label="PLANFORM"
  CoarseView = false
  Direction = (0,0,1)
  Focus = 100
  HardHidden = false
  IsoCount = 0
  IsoHidden = false
  IsoVisible = false
  LockPosition = false
  Perspective = false
  Rotation = 0
  RotationVector = (1,0,0)
  Scale = 0.33
  ScaleType = 0
  ScrubCount = 1
  SeamHidden = false
  SeamVisible = false
  SmoothHidden = false
  SmoothVisible = true
  Source = -> [Body044]
  Type = 0
  X = 169.728
  XDirection = (1e-16,-1,0)
  Y = 135.222
FEATURE [TechDraw::DrawViewDimension] Dimension
  AngleOverride = false
  Arbitrary = false
  ArbitraryTolerances = false
  BoxCorners = (2) [(-75.438,-50.292,0),(75.438,50.292,0)]
  EqualTolerance = true
  ExtensionAngle = 0
  FormatSpec = %.2w
  FormatSpecOverTolerance = %+.2w
  FormatSpecUnderTolerance = %+.2w
  Inverted = false
  LineAngle = 0
  LockPosition = false
  MeasureType = 1
  OverTolerance = 0
  References2D = -> [View]
  Rotation = 0
  Scale = 0.33
  ScaleType = 0
  TheoreticalExact = false
  Type = 0
  UnderTolerance = 0
  X = -67.419
  Y = 27.2628
FEATURE [TechDraw::DrawViewDimension] Dimension007
  AngleOverride = false
  Arbitrary = false
  ArbitraryTolerances = false
  BoxCorners = (2) [(-75.438,-50.292,0),(75.438,50.292,0)]
  EqualTolerance = true
  ExtensionAngle = 0
  FormatSpec = %.2w
  FormatSpecOverTolerance = %+.2w
  FormatSpecUnderTolerance = %+.2w
  Inverted = false
  LineAngle = 0
  LockPosition = false
  MeasureType = 1
  OverTolerance = 0
  References2D = -> [View]
  Rotation = 0
  Scale = 0.33
  ScaleType = 0
  TheoreticalExact = false
  Type = 0
  UnderTolerance = 0
  X = -1.59872
  Y = 0
FEATURE [TechDraw::DrawViewDimension] Dimension008
  AngleOverride = false
  Arbitrary = false
  ArbitraryTolerances = false
  BoxCorners = (2) [(-75.438,-50.292,0),(75.438,50.292,0)]
  EqualTolerance = true
  ExtensionAngle = 0
  FormatSpec = %.2w
  FormatSpecOverTolerance = %+.2w
  FormatSpecUnderTolerance = %+.2w
  Inverted = false
  LineAngle = 0
  LockPosition = false
  MeasureType = 1
  OverTolerance = 0
  References2D = -> [View]
  Rotation = 0
  Scale = 0.33
  ScaleType = 0
  TheoreticalExact = false
  Type = 0
  UnderTolerance = 0
  X = 0
  Y = 10.8083
FEATURE [TechDraw::DrawViewDimension] Dimension010
  AngleOverride = false
  Arbitrary = false
  ArbitraryTolerances = false
  BoxCorners = (2) [(-75.438,-50.292,0),(75.438,50.292,0)]
  EqualTolerance = true
  ExtensionAngle = 0
  FormatSpec = %.2w
  FormatSpecOverTolerance = %+.2w
  FormatSpecUnderTolerance = %+.2w
  Inverted = false
  LineAngle = 0
  LockPosition = false
  MeasureType = 1
  OverTolerance = 0
  References2D = -> [View]
  Rotation = 0
  Scale = 0.33
  ScaleType = 0
  TheoreticalExact = false
  Type = 0
  UnderTolerance = 0
  X = 26.4
  Y = 45.635
FEATURE [TechDraw::DrawViewDimension] Dimension011
  AngleOverride = false
  Arbitrary = false
  ArbitraryTolerances = false
  BoxCorners = (2) [(-75.438,-50.292,0),(75.438,50.292,0)]
  EqualTolerance = true
  ExtensionAngle = 0
  FormatSpec = %.2w
  FormatSpecOverTolerance = %+.2w
  FormatSpecUnderTolerance = %+.2w
  Inverted = false
  LineAngle = 0
  LockPosition = false
  MeasureType = 1
  OverTolerance = 0
  References2D = -> [View]
  Rotation = 0
  Scale = 0.33
  ScaleType = 0
  TheoreticalExact = false
  Type = 0
  UnderTolerance = 0
  X = 24.2921
  Y = 33
FEATURE [TechDraw::DrawViewDimension] Dimension016
  AngleOverride = false
  Arbitrary = false
  ArbitraryTolerances = false
  BoxCorners = (2) [(-75.438,-50.292,0),(75.438,50.292,0)]
  EqualTolerance = true
  ExtensionAngle = 0
  FormatSpec = 20X ⌀%.2w THRU
  FormatSpecOverTolerance = %+.2w
  FormatSpecUnderTolerance = %+.2w
  Inverted = false
  LineAngle = -3
  LockPosition = false
  MeasureType = 1
  OverTolerance = 0
  References2D = -> [View]
  Rotation = 0
  Scale = 0.33
  ScaleType = 0
  TheoreticalExact = false
  Type = 5
  UnderTolerance = 0
  X = 54.0132
  Y = -22.6739
FEATURE [TechDraw::DrawViewDimension] Dimension021
  AngleOverride = false
  Arbitrary = false
  ArbitraryTolerances = false
  BoxCorners = (2) [(-75.438,-50.292,0),(75.438,50.292,0)]
  EqualTolerance = true
  ExtensionAngle = 0
  FormatSpec = %.2w
  FormatSpecOverTolerance = %+.2w
  FormatSpecUnderTolerance = %+.2w
  Inverted = false
  LineAngle = 0
  LockPosition = false
  MeasureType = 1
  OverTolerance = 0
  References2D = -> [View]
  Rotation = 0
  Scale = 0.33
  ScaleType = 0
  TheoreticalExact = false
  Type = 1
  UnderTolerance = 0
  X = -18.7275
  Y = 10.8083
FEATURE [TechDraw::DrawViewDimension] Dimension022
  AngleOverride = false
  Arbitrary = false
  ArbitraryTolerances = false
  BoxCorners = (2) [(-75.438,-50.292,0),(75.438,50.292,0)]
  EqualTolerance = true
  ExtensionAngle = 0
  FormatSpec = %.2w
  FormatSpecOverTolerance = %+.2w
  FormatSpecUnderTolerance = %+.2w
  Inverted = false
  LineAngle = 0
  LockPosition = false
  MeasureType = 1
  OverTolerance = 0
  References2D = -> [View]
  Rotation = 0
  Scale = 0.33
  ScaleType = 0
  TheoreticalExact = false
  Type = 0
  UnderTolerance = 0
  X = -53.559
  Y = 15.2146
FEATURE [TechDraw::DrawViewDimension] Dimension023
  AngleOverride = false
  Arbitrary = false
  ArbitraryTolerances = false
  BoxCorners = (2) [(-75.438,-50.292,0),(75.438,50.292,0)]
  EqualTolerance = true
  ExtensionAngle = 0
  FormatSpec = %.2w
  FormatSpecOverTolerance = %+.2w
  FormatSpecUnderTolerance = %+.2w
  Inverted = false
  LineAngle = 0
  LockPosition = false
  MeasureType = 1
  OverTolerance = 0
  References2D = -> [View]
  Rotation = 0
  Scale = 0.33
  ScaleType = 0
  TheoreticalExact = false
  Type = 0
  UnderTolerance = 0
  X = -5.28
  Y = 45.635
FEATURE [TechDraw::DrawViewDimension] Dimension024
  AngleOverride = false
  Arbitrary = false
  ArbitraryTolerances = false
  BoxCorners = (2) [(-75.438,-50.292,0),(75.438,50.292,0)]
  EqualTolerance = true
  ExtensionAngle = 0
  FormatSpec = %.2w
  FormatSpecOverTolerance = %+.2w
  FormatSpecUnderTolerance = %+.2w
  Inverted = false
  LineAngle = 0
  LockPosition = false
  MeasureType = 1
  OverTolerance = 0
  References2D = -> [View]
  Rotation = 0
  Scale = 0.33
  ScaleType = 0
  TheoreticalExact = false
  Type = 0
  UnderTolerance = 0
  X = -30.1563
  Y = -9.92044
FEATURE [TechDraw::DrawViewDimension] Dimension025
  AngleOverride = false
  Arbitrary = false
  ArbitraryTolerances = false
  BoxCorners = (2) [(-75.438,-50.292,0),(75.438,50.292,0)]
  EqualTolerance = true
  ExtensionAngle = 0
  FormatSpec = %.2w
  FormatSpecOverTolerance = %+.2w
  FormatSpecUnderTolerance = %+.2w
  Inverted = false
  LineAngle = 0
  LockPosition = false
  MeasureType = 1
  OverTolerance = 0
  References2D = -> [View]
  Rotation = 0
  Scale = 0.33
  ScaleType = 0
  TheoreticalExact = false
  Type = 0
  UnderTolerance = 0
  X = -64.0788
  Y = 41.646
FEATURE [TechDraw::DrawViewDimension] Dimension027
  AngleOverride = false
  Arbitrary = false
  ArbitraryTolerances = false
  BoxCorners = (2) [(-75.438,-50.292,0),(75.438,50.292,0)]
  EqualTolerance = true
  ExtensionAngle = 0
  FormatSpec = %.2w
  FormatSpecOverTolerance = %+.2w
  FormatSpecUnderTolerance = %+.2w
  Inverted = false
  LineAngle = 0
  LockPosition = false
  MeasureType = 1
  OverTolerance = 5
  References2D = -> [View]
  Rotation = 0
  Scale = 0.33
  ScaleType = 0
  TheoreticalExact = false
  Type = 1
  UnderTolerance = -5
  X = -3.53844
  Y = 59.3644
FEATURE [TechDraw::DrawViewDimension] Dimension028
  AngleOverride = false
  Arbitrary = false
  ArbitraryTolerances = false
  BoxCorners = (2) [(-75.438,-50.292,0),(75.438,50.292,0)]
  EqualTolerance = true
  ExtensionAngle = 0
  FormatSpec = 12X %.2w
  FormatSpecOverTolerance = %+.2w
  FormatSpecUnderTolerance = %+.2w
  Inverted = false
  LineAngle = 0
  LockPosition = false
  MeasureType = 1
  OverTolerance = 0
  References2D = -> [View]
  Rotation = 0
  Scale = 0.33
  ScaleType = 0
  TheoreticalExact = false
  Type = 0
  UnderTolerance = 0
  X = 49.5
  Y = 38.635
FEATURE [TechDraw::DrawViewDimension] Dimension029
  AngleOverride = false
  Arbitrary = false
  ArbitraryTolerances = false
  BoxCorners = (2) [(-75.438,-50.292,0),(75.438,50.292,0)]
  EqualTolerance = true
  ExtensionAngle = 0
  FormatSpec = %.2w
  FormatSpecOverTolerance = %+.2w
  FormatSpecUnderTolerance = %+.2w
  Inverted = false
  LineAngle = 0
  LockPosition = false
  MeasureType = 1
  OverTolerance = 0
  References2D = -> [View]
  Rotation = 0
  Scale = 0.33
  ScaleType = 0
  TheoreticalExact = false
  Type = 0
  UnderTolerance = 0
  X = -40.2414
  Y = 21.042
FEATURE [TechDraw::DrawViewBalloon] Balloon
  BubbleShape = 1
  EndType = 0
  EndTypeScale = 1
  KinkLength = 5
  LockPosition = false
  OriginX = 0
  OriginY = -101.65
  Rotation = 0
  Scale = 0.33
  ScaleType = 0
  ShapeScale = 1
  SourceView = -> View
  Text = 14X M4x0.7 THRU
  TextWrapLen = -1
  X = 147.282
  Y = -36.8222
FEATURE [TechDraw::DrawViewBalloon] Balloon001
  BubbleShape = 1
  EndType = 0
  EndTypeScale = 1
  KinkLength = 5
  LockPosition = false
  OriginX = 64
  OriginY = -122.5
  Rotation = 0
  Scale = 0.33
  ScaleType = 0
  ShapeScale = 1
  SourceView = -> View
  Text = 16X ⌴⌀9↧8.7
  TextWrapLen = -1
  X = 162.364
  Y = -137.125
FEATURE [TechDraw::DrawViewBalloon] Balloon002
  BubbleShape = 1
  EndType = 0
  EndTypeScale = 1
  KinkLength = 22
  LockPosition = false
  OriginX = 17.5
  OriginY = 7.5
  Rotation = 0
  Scale = 0.33
  ScaleType = 0
  ShapeScale = 1
  SourceView = -> View
  Text = 4X ⌴⌀9↧7.5
  TextWrapLen = -1
  X = 165.388
  Y = -4.08134
FEATURE [TechDraw::DrawViewBalloon] Balloon004
  BubbleShape = 1
  EndType = 0
  EndTypeScale = 1
  KinkLength = 5
  LockPosition = false
  OriginX = -21.6953
  OriginY = -174.068
  Rotation = 0
  Scale = 0.33
  ScaleType = 0
  ShapeScale = 1
  SourceView = -> View
  Text = PLANFORM
  TextWrapLen = -1
  X = 0.541712
  Y = -174.442
FEATURE [TechDraw::DrawViewAnnotation] Annotation
  Font = osifont
  LineSpace = 100
  LockPosition = false
  MaxWidth = -1
  Rotation = 0
  Scale = 0.33
  ScaleType = 0
  Text = 1. PART INTENDED TO BE PRODUCED FROM | 18x12x0.5" ALUMINUM PLATE STOCK. | 2. DEBURR ALL SHARP EDGES. | 3. ALL DIMENSIONS TYPICAL. | 4. HOLE REPROCESSING PERMITTED FOR | FUNCTION AT NEXT HIGHER ASSEMBLY.
  TextSize = 3
  TextStyle = 0
  X = 63.348
  Y = 36.3537
FEATURE [TechDraw::DrawSVGTemplate] Template
  EditableTexts = approval_person=A.F.; creator=MATTHEW DIPALMA; date_of_issue=11/28/2024; document_status=RELEASED; document_type=DETAIL DRAWING; drawing_number=00001-001; general_tolerances=ISO 2768-c; language_code=EN; legal_owner_1=MARIAN; legal_owner_2=ELECTROMAGNETICS; legal_owner_3=BRIDGEPORT, CT; legal_owner_4=06606; part_material=ALUMINUM 6061; responsible_department=MECH ENG; revision_index=AAB; sheet_number=1 / 1; sheet_scale=1 : 3; supplementary_title_1=X LINEAR MOTION ASSEMBLY; supplementary_title_2=CNC; title=X GANTRY PLATE
  Height = 210
  Orientation = 1
  Template = <path>
  Width = 297
FEATURE [TechDraw::DrawPage] Page  label="00001-001"
  KeepUpdated = true
  NextBalloonIndex = 11
  ProjectionType = 0
  Scale = 0.33
  Template = -> Template
  Views = -> [View,View001,Dimension,Dimension006,Dimension007,Dimension008,Dimension010,Dimension011,Annotation,Dimension016,Dimension021,Dimension022,Dimension023,Balloon,Dimension024,Balloon001,Dimension025,Dimension027,Balloon002,Dimension028,Dimension029,Balloon004]
FEATURE [TechDraw::DrawViewDimension] Dimension049
  AngleOverride = false
  Arbitrary = false
  ArbitraryTolerances = false
  BoxCorners = (2) [(-50.7999,-50.7999,0),(50.7999,50.7999,0)]
  EqualTolerance = true
  ExtensionAngle = 0
  FormatSpec = 20X⌀%.2w THRU
  FormatSpecOverTolerance = %+.2w
  FormatSpecUnderTolerance = %+.2w
  Inverted = false
  LineAngle = 0
  LockPosition = false
  MeasureType = 1
  OverTolerance = 0
  References2D = -> [View005]
  Rotation = 0
  ScaleType = 0
  TheoreticalExact = false
  Type = 5
  UnderTolerance = 0
  X = -1.06936
  Y = -23.5045
FEATURE [TechDraw::DrawViewBalloon] Balloon010
  BubbleShape = 1
  EndType = 0
  EndTypeScale = 1
  KinkLength = 5
  LockPosition = false
  OriginX = 57.5
  OriginY = 84
  Rotation = 0
  ScaleType = 0
  ShapeScale = 1
  SourceView = -> View005
  Text = 16X ⌴⌀9↧8.7
  TextWrapLen = -1
  X = 90.2963
  Y = 50.0094
FEATURE [TechDraw::DrawViewBalloon] Balloon011
  BubbleShape = 1
  EndType = 0
  EndTypeScale = 1
  KinkLength = 5
  LockPosition = false
  OriginX = 7.5
  OriginY = 17.5
  Rotation = 0
  ScaleType = 0
  ShapeScale = 1
  SourceView = -> View005
  Text = 4X ⌴⌀9↧7.5
  TextWrapLen = -1
  X = 93.7857
  Y = 5.64536
FEATURE [PartDesign::FeatureBase] Clone063
  BaseFeature = -> Body060
  Suppressed = false
FEATURE [PartDesign::Body] Body098  label="nema23_b"
  AllowCompound = false
  Group = -> [Clone063]
  Origin = -> Origin104
  Placement = pos=(-98.4,-305,120.9) rot=(0,1,0;4.71239rad)
  Tip = -> Clone063
  expr: .Placement.Base.y = -305 mm + Group001.Base_x_coord
FEATURE [TechDraw::DrawViewDimension] Dimension050
  AngleOverride = false
  Arbitrary = false
  ArbitraryTolerances = false
  BoxCorners = (2) [(-15,-25,0),(15,25,0)]
  EqualTolerance = true
  ExtensionAngle = 0
  FormatSpec = %.2w
  FormatSpecOverTolerance = %+.2w
  FormatSpecUnderTolerance = %+.2w
  Inverted = false
  LineAngle = 0
  LockPosition = false
  MeasureType = 1
  OverTolerance = 0
  References2D = -> [View003]
  Rotation = 0
  ScaleType = 0
  TheoreticalExact = false
  Type = 1
  UnderTolerance = 0
  X = 0
  Y = 4.34819
FEATURE [TechDraw::DrawViewAnnotation] Annotation004
  Font = osifont
  LineSpace = 100
  LockPosition = false
  MaxWidth = -1
  Rotation = 0
  ScaleType = 0
  Text = SCALE 1:2
  TextSize = 4
  TextStyle = 0
  X = 63.348
  Y = 139.787
FEATURE [TechDraw::DrawPage] Page001  label="00001-002"
  KeepUpdated = true
  NextBalloonIndex = 3
  ProjectionType = 0
  Template = -> Template001
  Views = -> [View002,Dimension030,Dimension031,Dimension032,View003,Dimension034,Dimension035,Dimension036,Dimension037,View004,Annotation001,Dimension050,Annotation004]
FEATURE [TechDraw::DrawViewDimension] Dimension051
  AngleOverride = false
  Arbitrary = false
  ArbitraryTolerances = false
  BoxCorners = (2) [(-50.7999,-50.7999,0),(50.7999,50.7999,0)]
  EqualTolerance = true
  ExtensionAngle = 0
  FormatSpec = %.2w
  FormatSpecOverTolerance = %+.2w
  FormatSpecUnderTolerance = %+.2w
  Inverted = false
  LineAngle = 0
  LockPosition = false
  MeasureType = 1
  OverTolerance = 0
  References2D = -> [View005]
  Rotation = 0
  ScaleType = 0
  TheoreticalExact = false
  Type = 0
  UnderTolerance = 0
  X = -5.99999
  Y = 36.3994
FEATURE [TechDraw::DrawPage] Page003  label="00001-003"
  KeepUpdated = true
  NextBalloonIndex = 7
  ProjectionType = 0
  Template = -> Template003
  Views = -> [Annotation002,ProjGroup,View006,Balloon007,Balloon008,Balloon009,Dimension038,Dimension039,Dimension040,Dimension041,Dimension042,Dimension043,Dimension044,Annotation003,Dimension045,Dimension046,Dimension047,Dimension049,Balloon010,Balloon011,Dimension051]
FEATURE [Sketcher::SketchObject] Sketch048
  ArcFitTolerance = 1e-06
  AttachmentSupport = -> [XY_Plane105]
  FullyConstrained = true
  MakeInternals = false
  MapMode = 5
  sketch-geometry (4):
    g0: LineSegment StartX=-304.8 StartY=275 StartZ=0 EndX=-304.8 EndY=-275 EndZ=0
    g1: LineSegment StartX=-304.8 StartY=-275 StartZ=0 EndX=304.8 EndY=-275 EndZ=0
    g2: LineSegment StartX=304.8 StartY=-275 StartZ=0 EndX=304.8 EndY=275 EndZ=0
    g3: LineSegment StartX=304.8 StartY=275 StartZ=0 EndX=-304.8 EndY=275 EndZ=0
  constraints (10):
    c: Coincident(g0,g1)
    c: Coincident(g1,g2)
    c: Coincident(g2,g3)
    c: Coincident(g3,g0)
    c: Vertical(g0)
    c: Horizontal(g1)
    c: DistanceX(g3,g3) = 609.6
    c: DistanceY(g0,g0) = 550
    c: Symmetric(g0,g2,g-2)
    c: Symmetric(g2,g1,g-1)
FEATURE [PartDesign::Pad] Pad040
  Direction = (0,0,1)
  Length = 19.05
  Length2 = 10
  Profile = -> Sketch048
  ReferenceAxis = -> Sketch048 [N_Axis]
  Refine = true
  Suppressed = false
  Type = 0
FEATURE [PartDesign::Body] Body099  label="case side panel"
  AllowCompound = false
  Group = -> [Sketch048,Pad040]
  Origin = -> Origin105
  Tip = -> Pad040
FEATURE [PartDesign::FeatureBase] Clone065
  BaseFeature = -> Body099
  Suppressed = false
FEATURE [PartDesign::Body] Body101  label="back panel"
  AllowCompound = false
  Group = -> [Clone065]
  Origin = -> Origin107
  Placement = pos=(-285.2,-610,256) rot=(1,0,0;1.5708rad)
  Tip = -> Clone065
FEATURE [PartDesign::FeatureBase] Clone066
  BaseFeature = -> Body099
  Suppressed = false
FEATURE [PartDesign::Body] Body102  label="left panel"
  AllowCompound = false
  Group = -> [Clone066]
  Origin = -> Origin108
  Placement = pos=(20,-305,255) rot=(0.57735,0.57735,0.57735;2.0944rad)
  Tip = -> Clone066
FEATURE [PartDesign::FeatureBase] Clone067
  BaseFeature = -> Body099
  Suppressed = false
FEATURE [PartDesign::Body] Body103  label="right panel"
  AllowCompound = false
  Group = -> [Clone067]
  Origin = -> Origin109
  Placement = pos=(-609.05,-305,255) rot=(0.57735,0.57735,0.57735;2.0944rad)
  Tip = -> Clone067
FEATURE [Sketcher::SketchObject] Sketch049
  ArcFitTolerance = 1e-06
  AttachmentSupport = -> [XY_Plane110]
  FullyConstrained = true
  MakeInternals = false
  MapMode = 5
  sketch-geometry (4):
    g0: LineSegment StartX=-304.8 StartY=304.8 StartZ=0 EndX=-304.8 EndY=-304.8 EndZ=0
    g1: LineSegment StartX=-304.8 StartY=-304.8 StartZ=0 EndX=304.8 EndY=-304.8 EndZ=0
    g2: LineSegment StartX=304.8 StartY=-304.8 StartZ=0 EndX=304.8 EndY=304.8 EndZ=0
    g3: LineSegment StartX=304.8 StartY=304.8 StartZ=0 EndX=-304.8 EndY=304.8 EndZ=0
  constraints (10):
    c: Coincident(g0,g1)
    c: Coincident(g1,g2)
    c: Coincident(g2,g3)
    c: Coincident(g3,g0)
    c: Vertical(g0)
    c: Horizontal(g1)
    c: DistanceX(g3,g3) = 609.6
    c: DistanceY(g0,g0) = 609.6
    c: Symmetric(g0,g2,g-2)
    c: Symmetric(g2,g1,g-1)
FEATURE [PartDesign::Pad] Pad041
  Direction = (0,0,1)
  Length = 19.05
  Length2 = 10
  Profile = -> Sketch049
  ReferenceAxis = -> Sketch049 [N_Axis]
  Refine = true
  Suppressed = false
  Type = 0
FEATURE [PartDesign::Body] Body104  label="case top/bottom panel"
  AllowCompound = false
  Group = -> [Sketch049,Pad041]
  Origin = -> Origin110
  Tip = -> Pad041
FEATURE [PartDesign::FeatureBase] Clone068
  BaseFeature = -> Body104
  Suppressed = false
FEATURE [PartDesign::Body] Body105  label="top panel"
  AllowCompound = false
  Group = -> [Clone068]
  Origin = -> Origin111
  Placement = pos=(-285.2,-304.8,530) rot=(0,0,1;0rad)
  Tip = -> Clone068
FEATURE [PartDesign::FeatureBase] Clone069
  BaseFeature = -> Body104
  Suppressed = false
FEATURE [PartDesign::Body] Body106  label="bottom panel"
  AllowCompound = false
  Group = -> [Clone069]
  Origin = -> Origin112
  Placement = pos=(-285.2,-304.8,-39.05) rot=(0,0,1;0rad)
  Tip = -> Clone069
FEATURE [Sketcher::SketchObject] Sketch050
  ArcFitTolerance = 1e-06
  AttachmentSupport = -> [XY_Plane113]
  FullyConstrained = true
  MakeInternals = false
  MapMode = 5
  sketch-geometry (4):
    g0: LineSegment StartX=-304.8 StartY=275 StartZ=0 EndX=-304.8 EndY=-275 EndZ=0
    g1: LineSegment StartX=-304.8 StartY=-275 StartZ=0 EndX=304.8 EndY=-275 EndZ=0
    g2: LineSegment StartX=304.8 StartY=-275 StartZ=0 EndX=304.8 EndY=275 EndZ=0
    g3: LineSegment StartX=304.8 StartY=275 StartZ=0 EndX=-304.8 EndY=275 EndZ=0
  constraints (10):
    c: Coincident(g0,g1)
    c: Coincident(g1,g2)
    c: Coincident(g2,g3)
    c: Coincident(g3,g0)
    c: Vertical(g0)
    c: Horizontal(g1)
    c: DistanceX(g3,g3) = 609.6
    c: DistanceY(g0,g0) = 550
    c: Symmetric(g0,g2,g-2)
    c: Symmetric(g2,g1,g-1)
FEATURE [PartDesign::Pad] Pad042
  Direction = (0,0,1)
  Length = 12.7
  Length2 = 10
  Profile = -> Sketch050
  ReferenceAxis = -> Sketch050 [N_Axis]
  Refine = true
  Suppressed = false
  Type = 0
FEATURE [PartDesign::Body] Body107  label="case front panel"
  AllowCompound = false
  Group = -> [Sketch050,Pad042]
  Origin = -> Origin113
  Tip = -> Pad042
FEATURE [PartDesign::FeatureBase] Clone070
  BaseFeature = -> Body107
  Suppressed = false
FEATURE [PartDesign::Body] Body108  label="front panel"
  AllowCompound = false
  Group = -> [Clone070]
  Origin = -> Origin114
  Placement = pos=(-285.2,12.7,255) rot=(1,0,0;1.5708rad)
  Tip = -> Clone070
FEATURE [Sketcher::SketchObject] Sketch051
  ArcFitTolerance = 1e-06
  AttachmentSupport = -> [XY_Plane115]
  FullyConstrained = true
  MakeInternals = false
  MapMode = 5
  sketch-geometry (4):
    g0: LineSegment StartX=-304.8 StartY=304.8 StartZ=0 EndX=-304.8 EndY=-304.8 EndZ=0
    g1: LineSegment StartX=-304.8 StartY=-304.8 StartZ=0 EndX=304.8 EndY=-304.8 EndZ=0
    g2: LineSegment StartX=304.8 StartY=-304.8 StartZ=0 EndX=304.8 EndY=304.8 EndZ=0
    g3: LineSegment StartX=304.8 StartY=304.8 StartZ=0 EndX=-304.8 EndY=304.8 EndZ=0
  constraints (10):
    c: Coincident(g0,g1)
    c: Coincident(g1,g2)
    c: Coincident(g2,g3)
    c: Coincident(g3,g0)
    c: Vertical(g0)
    c: Horizontal(g1)
    c: DistanceX(g3,g3) = 609.6
    c: DistanceY(g0,g0) = 609.6
    c: Symmetric(g0,g2,g-2)
    c: Symmetric(g2,g1,g-1)
FEATURE [PartDesign::Pad] Pad043
  Direction = (0,0,1)
  Length = 19.05
  Length2 = 10
  Profile = -> Sketch051
  ReferenceAxis = -> Sketch051 [N_Axis]
  Refine = true
  Suppressed = false
  Type = 0
FEATURE [PartDesign::Body] Body109  label="rubber pad"
  AllowCompound = false
  Group = -> [Sketch051,Pad043]
  Origin = -> Origin115
  Tip = -> Pad043
FEATURE [Sketcher::SketchObject] Sketch052
  ArcFitTolerance = 1e-06
  AttachmentSupport = -> [XY_Plane116]
  FullyConstrained = true
  MakeInternals = false
  MapMode = 5
  sketch-geometry (4):
    g0: LineSegment StartX=-25.4 StartY=25.4 StartZ=0 EndX=-25.4 EndY=-25.4 EndZ=0
    g1: LineSegment StartX=-25.4 StartY=-25.4 StartZ=0 EndX=25.4 EndY=-25.4 EndZ=0
    g2: LineSegment StartX=25.4 StartY=-25.4 StartZ=0 EndX=25.4 EndY=25.4 EndZ=0
    g3: LineSegment StartX=25.4 StartY=25.4 StartZ=0 EndX=-25.4 EndY=25.4 EndZ=0
  constraints (10):
    c: Coincident(g0,g1)
    c: Coincident(g1,g2)
    c: Coincident(g2,g3)
    c: Coincident(g3,g0)
    c: Vertical(g0)
    c: Horizontal(g1)
    c: DistanceX(g3,g3) = 50.8
    c: DistanceY(g0,g0) = 50.8
    c: Symmetric(g0,g2,g-2)
    c: Symmetric(g2,g1,g-1)
FEATURE [PartDesign::Pad] Pad044
  Direction = (0,0,1)
  Length = 22.225
  Length2 = 10
  Profile = -> Sketch052
  ReferenceAxis = -> Sketch052 [N_Axis]
  Refine = true
  Suppressed = false
  Type = 0
FEATURE [PartDesign::Body] Body110  label="rubber pad foot"
  AllowCompound = false
  Group = -> [Sketch052,Pad044]
  Origin = -> Origin116
  Tip = -> Pad044
FEATURE [PartDesign::FeatureBase] Clone071
  BaseFeature = -> Body110
  Suppressed = false
FEATURE [PartDesign::Body] Body111  label="foot1"
  AllowCompound = false
  Group = -> [Clone071]
  Origin = -> Origin117
  Placement = pos=(-5.8,-25.4,-61.27) rot=(0,0,1;0rad)
  Tip = -> Clone071
FEATURE [PartDesign::FeatureBase] Clone072
  BaseFeature = -> Body110
  Suppressed = false
FEATURE [PartDesign::Body] Body112  label="foot2"
  AllowCompound = false
  Group = -> [Clone072]
  Origin = -> Origin118
  Placement = pos=(-285.2,-25.4,-61.27) rot=(0,0,1;0rad)
  Tip = -> Clone072
FEATURE [PartDesign::FeatureBase] Clone073
  BaseFeature = -> Body110
  Suppressed = false
FEATURE [PartDesign::Body] Body113  label="foot3"
  AllowCompound = false
  Group = -> [Clone073]
  Origin = -> Origin119
  Placement = pos=(-564.6,-25.4,-61.27) rot=(0,0,1;0rad)
  Tip = -> Clone073
FEATURE [PartDesign::FeatureBase] Clone074
  BaseFeature = -> Body110
  Suppressed = false
FEATURE [PartDesign::Body] Body114  label="foot4"
  AllowCompound = false
  Group = -> [Clone074]
  Origin = -> Origin120
  Placement = pos=(-5.8,-304.8,-61.27) rot=(0,0,1;0rad)
  Tip = -> Clone074
FEATURE [PartDesign::FeatureBase] Clone075
  BaseFeature = -> Body110
  Suppressed = false
FEATURE [PartDesign::Body] Body115  label="foot5"
  AllowCompound = false
  Group = -> [Clone075]
  Origin = -> Origin121
  Placement = pos=(-564.6,-304.8,-61.27) rot=(0,0,1;0rad)
  Tip = -> Clone075
FEATURE [PartDesign::FeatureBase] Clone076
  BaseFeature = -> Body110
  Suppressed = false
FEATURE [PartDesign::Body] Body116  label="foot6"
  AllowCompound = false
  Group = -> [Clone076]
  Origin = -> Origin122
  Placement = pos=(-5.8,-584.2,-61.27) rot=(0,0,1;0rad)
  Tip = -> Clone076
FEATURE [PartDesign::FeatureBase] Clone077
  BaseFeature = -> Body110
  Suppressed = false
FEATURE [PartDesign::Body] Body117  label="foot7"
  AllowCompound = false
  Group = -> [Clone077]
  Origin = -> Origin123
  Placement = pos=(-285.2,-584.2,-61.27) rot=(0,0,1;0rad)
  Tip = -> Clone077
FEATURE [PartDesign::FeatureBase] Clone078
  BaseFeature = -> Body110
  Suppressed = false
FEATURE [PartDesign::Body] Body118  label="foot8"
  AllowCompound = false
  Group = -> [Clone078]
  Origin = -> Origin124
  Placement = pos=(-564.6,-584.2,-61.27) rot=(0,0,1;0rad)
  Tip = -> Clone078
FEATURE [PartDesign::FeatureBase] Clone079
  BaseFeature = -> Body110
  Suppressed = false
FEATURE [PartDesign::Body] Body119  label="foot9"
  AllowCompound = false
  Group = -> [Clone079]
  Origin = -> Origin125
  Placement = pos=(-145.5,-165.1,-61.27) rot=(0,0,1;0rad)
  Tip = -> Clone079
FEATURE [PartDesign::FeatureBase] Clone080
  BaseFeature = -> Body110
  Suppressed = false
FEATURE [PartDesign::Body] Body120  label="foot10"
  AllowCompound = false
  Group = -> [Clone080]
  Origin = -> Origin126
  Placement = pos=(-145.5,-444.5,-61.27) rot=(0,0,1;0rad)
  Tip = -> Clone080
FEATURE [PartDesign::FeatureBase] Clone081
  BaseFeature = -> Body110
  Suppressed = false
FEATURE [PartDesign::Body] Body121  label="foot11"
  AllowCompound = false
  Group = -> [Clone081]
  Origin = -> Origin127
  Placement = pos=(-424.9,-165.1,-61.27) rot=(0,0,1;0rad)
  Tip = -> Clone081
FEATURE [PartDesign::FeatureBase] Clone082
  BaseFeature = -> Body110
  Suppressed = false
FEATURE [PartDesign::Body] Body122  label="foot12"
  AllowCompound = false
  Group = -> [Clone082]
  Origin = -> Origin128
  Placement = pos=(-424.9,-444.5,-61.27) rot=(0,0,1;0rad)
  Tip = -> Clone082
FEATURE [App::DocumentObjectGroup] Group005  label="case"
  Group = -> [Body101,Body102,Body103,Body105,Body106,Body108,Body111,Body112,Body113,Body114,Body115,Body116,Body117,Body118,Body119,Body120,Body121,Body122]
FEATURE [Sketcher::SketchObject] Sketch053
  ArcFitTolerance = 1e-06
  AttachmentSupport = -> [XY_Plane129]
  FullyConstrained = true
  MakeInternals = false
  MapMode = 5
  sketch-geometry (6):
    g0: LineSegment StartX=-35 StartY=12.7 StartZ=0 EndX=-35 EndY=-12.7 EndZ=0
    g1: LineSegment StartX=-35 StartY=-12.7 StartZ=0 EndX=35 EndY=-12.7 EndZ=0
    g2: LineSegment StartX=35 StartY=-12.7 StartZ=0 EndX=35 EndY=12.7 EndZ=0
    g3: LineSegment StartX=35 StartY=12.7 StartZ=0 EndX=-35 EndY=12.7 EndZ=0
    g4: Circle CenterX=-23 CenterY=0 CenterZ=0 NormalX=0 NormalY=0 NormalZ=1 AngleXU=0 Radius=3
    g5: Circle CenterX=23 CenterY=0 CenterZ=0 NormalX=0 NormalY=0 NormalZ=1 AngleXU=0 Radius=3
  constraints (16):
    c: Coincident(g0,g1)
    c: Coincident(g1,g2)
    c: Coincident(g2,g3)
    c: Coincident(g3,g0)
    c: Vertical(g2)
    c: Horizontal(g1)
    c: Symmetric(g0,g0,g-1)
    c: Symmetric(g0,g2,g-2)
    c: DistanceX(g3,g3) = 70
    c: DistanceY(g0,g0) = 25.4
    c: PointOnObject(g4,g-1)
    c: PointOnObject(g5,g-1)
    c: Equal(g4,g5)
    c: Diameter(g4) = 6
    c: DistanceX(g4,g5) = 46
    c: Distance(g4,g0) = 12
FEATURE [PartDesign::Pad] Pad045
  Direction = (0,0,1)
  Length = 6.35
  Length2 = 10
  Profile = -> Sketch053
  ReferenceAxis = -> Sketch053 [N_Axis]
  Refine = true
  Suppressed = false
  Type = 0
FEATURE [PartDesign::Body] Body123  label="bf10 spacer"
  AllowCompound = false
  Group = -> [Sketch053,Pad045]
  Origin = -> Origin129
  Tip = -> Pad045
FEATURE [PartDesign::FeatureBase] Clone083
  BaseFeature = -> Body123
  Suppressed = false
FEATURE [PartDesign::Body] Body124  label="bf12 spacer001"
  AllowCompound = false
  Group = -> [Clone083]
  Origin = -> Origin130
  Placement = pos=(-285,-590,20.12) rot=(0,0,1;0rad)
  Tip = -> Clone083
FEATURE [Sketcher::SketchObject] Sketch054
  ArcFitTolerance = 1e-06
  AttachmentSupport = -> [XY_Plane131]
  FullyConstrained = true
  MakeInternals = false
  MapMode = 5
  sketch-geometry (12):
    g0: LineSegment StartX=-50 StartY=12.7 StartZ=0 EndX=-50 EndY=-12.7 EndZ=0
    g1: LineSegment StartX=-50 StartY=-12.7 StartZ=0 EndX=50 EndY=-12.7 EndZ=0
    g2: LineSegment StartX=50 StartY=-12.7 StartZ=0 EndX=50 EndY=12.7 EndZ=0
    g3: LineSegment StartX=50 StartY=12.7 StartZ=0 EndX=-50 EndY=12.7 EndZ=0
    g4: Circle CenterX=-23 CenterY=6.5 CenterZ=0 NormalX=0 NormalY=0 NormalZ=1 AngleXU=0 Radius=2.1
    g5: Circle CenterX=23 CenterY=6.5 CenterZ=0 NormalX=0 NormalY=0 NormalZ=1 AngleXU=0 Radius=2.1
    g6: Circle CenterX=-23 CenterY=-6.5 CenterZ=0 NormalX=0 NormalY=0 NormalZ=1 AngleXU=0 Radius=2.1
    g7: Circle CenterX=23 CenterY=-6.5 CenterZ=0 NormalX=0 NormalY=0 NormalZ=1 AngleXU=0 Radius=2.1
    g8: Circle CenterX=-40 CenterY=6 CenterZ=0 NormalX=0 NormalY=0 NormalZ=1 AngleXU=0 Radius=2.75
    g9: Circle CenterX=-40 CenterY=-6 CenterZ=0 NormalX=0 NormalY=0 NormalZ=1 AngleXU=0 Radius=2.75
    g10: Circle CenterX=40 CenterY=6 CenterZ=0 NormalX=0 NormalY=0 NormalZ=1 AngleXU=0 Radius=2.75
    g11: Circle CenterX=40 CenterY=-6 CenterZ=0 NormalX=0 NormalY=0 NormalZ=1 AngleXU=0 Radius=2.75
  constraints (30):
    c: Coincident(g0,g1)
    c: Coincident(g1,g2)
    c: Coincident(g2,g3)
    c: Coincident(g3,g0)
    c: Vertical(g2)
    c: Horizontal(g1)
    c: Symmetric(g0,g0,g-1)
    c: Symmetric(g0,g2,g-2)
    c: DistanceX(g3,g3) = 100
    c: DistanceY(g0,g0) = 25.4
    c: Equal(g4,g5)
    c: Diameter(g4) = 4.2
    c: DistanceX(g4,g5) = 46
    c: Symmetric(g4,g5,g-2)
    c: Vertical(g7,g5)
    c: Horizontal(g7,g6)
    c: Symmetric(g4,g6,g-1)
    c: Equal(g6,g7)
    c: Equal(g7,g5)
    c: Distance(g4,g6) = 13
    c: Vertical(g8,g9)
    c: Horizontal(g9,g11)
    c: DistanceY(g11,g10) = 12
    c: Equal(g10,g11)
    c: Equal(g11,g9)
    c: Equal(g9,g8)
    c: Diameter(g8) = 5.5
    c: DistanceX(g9,g11) = 80
    c: Symmetric(g8,g10,g-2)
    c: Symmetric(g10,g11,g-1)
FEATURE [PartDesign::Pad] Pad046
  Direction = (0,0,1)
  Length = 6.35
  Length2 = 10
  Profile = -> Sketch054
  ReferenceAxis = -> Sketch054 [N_Axis]
  Refine = true
  Suppressed = false
  Type = 0
FEATURE [PartDesign::Body] Body125  label="bk10 spacer"
  AllowCompound = false
  Group = -> [Sketch054,Pad046]
  Origin = -> Origin131
  Tip = -> Pad046
FEATURE [PartDesign::FeatureBase] Clone084
  BaseFeature = -> Body125
  Suppressed = false
FEATURE [PartDesign::Body] Body126  label="bk10 spacer001"
  AllowCompound = false
  Group = -> [Clone084]
  Origin = -> Origin132
  Placement = pos=(-285,-117.2,20.12) rot=(0,0,1;0rad)
  Tip = -> Clone084
FEATURE [PartDesign::FeatureBase] Clone085
  BaseFeature = -> Body096
  Suppressed = false
FEATURE [PartDesign::Body] Body127  label="dsg12h002"
  AllowCompound = false
  Group = -> [Clone085]
  Origin = -> Origin133
  Placement = pos=(-267,-305,120.9) rot=(0,0,1;-1.5708rad)
  Tip = -> Clone085
  expr: .Placement.Base.x = -267 mm + Group001.Base_y_coord
  expr: .Placement.Base.y = -305 mm + Group001.Base_x_coord
FEATURE [PartDesign::FeatureBase] Clone086
  BaseFeature = -> Body066
  Suppressed = false
FEATURE [PartDesign::Body] Body128  label="sfu1204x400"
  AllowCompound = false
  Group = -> [Clone086]
  Origin = -> Origin134
  Placement = pos=(-119.4,-305,120.9) rot=(0,0,1;3.14159rad)
  Tip = -> Clone086
  expr: .Placement.Base.x = -119.4 mm
  expr: .Placement.Base.y = -305 mm + Group001.Base_x_coord
FEATURE [App::DocumentObjectGroup] Group004  label="Y-axis motion"
  Group = -> [Body069,Body070,Body071,Body072,Body073,Body074,Body075,Body076,Body077,Body078,Body079,Body098,Body127,Body128]
FEATURE [Sketcher::SketchObject] Sketch055
  ArcFitTolerance = 1e-06
  AttachmentSupport = -> [XY_Plane135]
  FullyConstrained = true
  MakeInternals = false
  MapMode = 5
  sketch-geometry (8):
    g0: LineSegment StartX=-20 StartY=-32.5 StartZ=0 EndX=20 EndY=-32.5 EndZ=0
    g1: LineSegment StartX=20 StartY=-32.5 StartZ=0 EndX=20 EndY=32.5 EndZ=0
    g2: LineSegment StartX=20 StartY=32.5 StartZ=0 EndX=-20 EndY=32.5 EndZ=0
    g3: LineSegment StartX=-20 StartY=32.5 StartZ=0 EndX=-20 EndY=-32.5 EndZ=0
    g4: Circle CenterX=10 CenterY=-12.5 CenterZ=0 NormalX=0 NormalY=0 NormalZ=1 AngleXU=0 Radius=4.1
    g5: Circle CenterX=10.5 CenterY=25 CenterZ=0 NormalX=0 NormalY=0 NormalZ=1 AngleXU=0 Radius=1.25
    g6: Circle CenterX=10.5 CenterY=15.5 CenterZ=0 NormalX=0 NormalY=0 NormalZ=1 AngleXU=0 Radius=1.25
    g7: Circle CenterX=-10 CenterY=-12.5 CenterZ=0 NormalX=0 NormalY=0 NormalZ=1 AngleXU=0 Radius=4.1
  constraints (21):
    c: Coincident(g0,g1)
    c: Coincident(g1,g2)
    c: Coincident(g2,g3)
    c: Coincident(g3,g0)
    c: Horizontal(g2)
    c: Vertical(g1)
    c: DistanceX(g0,g0) = 40
    c: DistanceY(g1,g1) = 65
    c: Symmetric(g0,g0,g-2)
    c: Symmetric(g2,g0,g-1)
    c: Diameter(g4) = 8.2
    c: Distance(g4,g0) = 20
    c: Equal(g5,g6)
    c: Diameter(g5) = 2.5
    c: Vertical(g5,g6)
    c: DistanceY(g6,g5) = 9.5
    c: Distance(g5,g2) = 7.5
    c: Distance(g5,g1) = 9.5
    c: Equal(g7,g4)
    c: Symmetric(g7,g4,g-2)
    c: DistanceX(g7,g4) = 20
FEATURE [PartDesign::Pad] Pad047
  Direction = (0,0,1)
  Length = 2
  Length2 = 10
  Profile = -> Sketch055
  ReferenceAxis = -> Sketch055 [N_Axis]
  Refine = true
  Suppressed = false
  Type = 0
FEATURE [PartDesign::Body] Body129  label="x axis limit switch post"
  AllowCompound = false
  Group = -> [Sketch055,Pad047]
  Origin = -> Origin135
  Tip = -> Pad047
FEATURE [App::DocumentObjectGroup] Parts  label="Part Library"
  Group = -> [Body001,Body002,Body003,Body004,Body005,Body006,Body,Body007,Body008,Cut007,Body019,Body018,Body020,Body043,Body044,Body058,Body060,Spreadsheet,Body062,Body066,Body065,Body067,Body068,Body080,Body093,Body096,Body099,Body104,Body107,Body109,Body110,Body123,Body125,Body129]
FEATURE [PartDesign::FeatureBase] Clone087
  BaseFeature = -> Body129
  Suppressed = false
FEATURE [PartDesign::Body] Body130  label="x+ limit switch mount plate"
  AllowCompound = false
  Group = -> [Clone087]
  Origin = -> Origin136
  Placement = pos=(-385,-120,12.5) rot=(-0.57735,0.57735,0.57735;4.18879rad)
  Tip = -> Clone087
FEATURE [PartDesign::FeatureBase] Clone088
  BaseFeature = -> Body129
  Suppressed = false
FEATURE [PartDesign::Body] Body131  label="x- limit switch mount plate"
  AllowCompound = false
  Group = -> [Clone088]
  Origin = -> Origin137
  Placement = pos=(-387,-500,12.5) rot=(0.57735,0.57735,0.57735;2.0944rad)
  Tip = -> Clone088
FEATURE [PartDesign::FeatureBase] Clone089
  BaseFeature = -> Body131
  Placement = pos=(-387,-500,12.5) rot=(0.57735,0.57735,0.57735;2.0944rad)
  Suppressed = false
FEATURE [PartDesign::Body] Body132  label="x homing switch"
  AllowCompound = false
  Group = -> [Clone089]
  Origin = -> Origin138
  Placement = pos=(202,0,0) rot=(0,0,1;0rad)
  Tip = -> Clone089
FEATURE [App::DocumentObjectGroup] Group002  label="X-axis motion"
  Group = -> [Body045,Body046,Body047,Body048,Body049,Body050,Body051,Body052,Body053,Body054,Body055,Body061,Body063,Body064,Body094,Body095,Body097,Body124,Body126,Body130,Body131,Body132]
FEATURE [PartDesign::FeatureBase] Clone090
  BaseFeature = -> Body068
  Placement = pos=(0,0,0) rot=(0,1,0;1.5708rad)
  Suppressed = false
FEATURE [PartDesign::Body] Body133  label="sfu1204x200mm001"
  AllowCompound = false
  Group = -> [Clone090]
  Origin = -> Origin139
  Placement = pos=(-280.5,-400,440) rot=(0,0,1;0rad)
  Tip = -> Clone090
FEATURE [App::DocumentObjectGroup] Group003  label="Z-axis motion"
  Group = -> [Body059,Body081,Body083,Body084,Body086,Body088,Body090,Body092,Body133]
note: 4 file-system paths scrubbed to <path> (originals preserved in the JSON sidecar)
